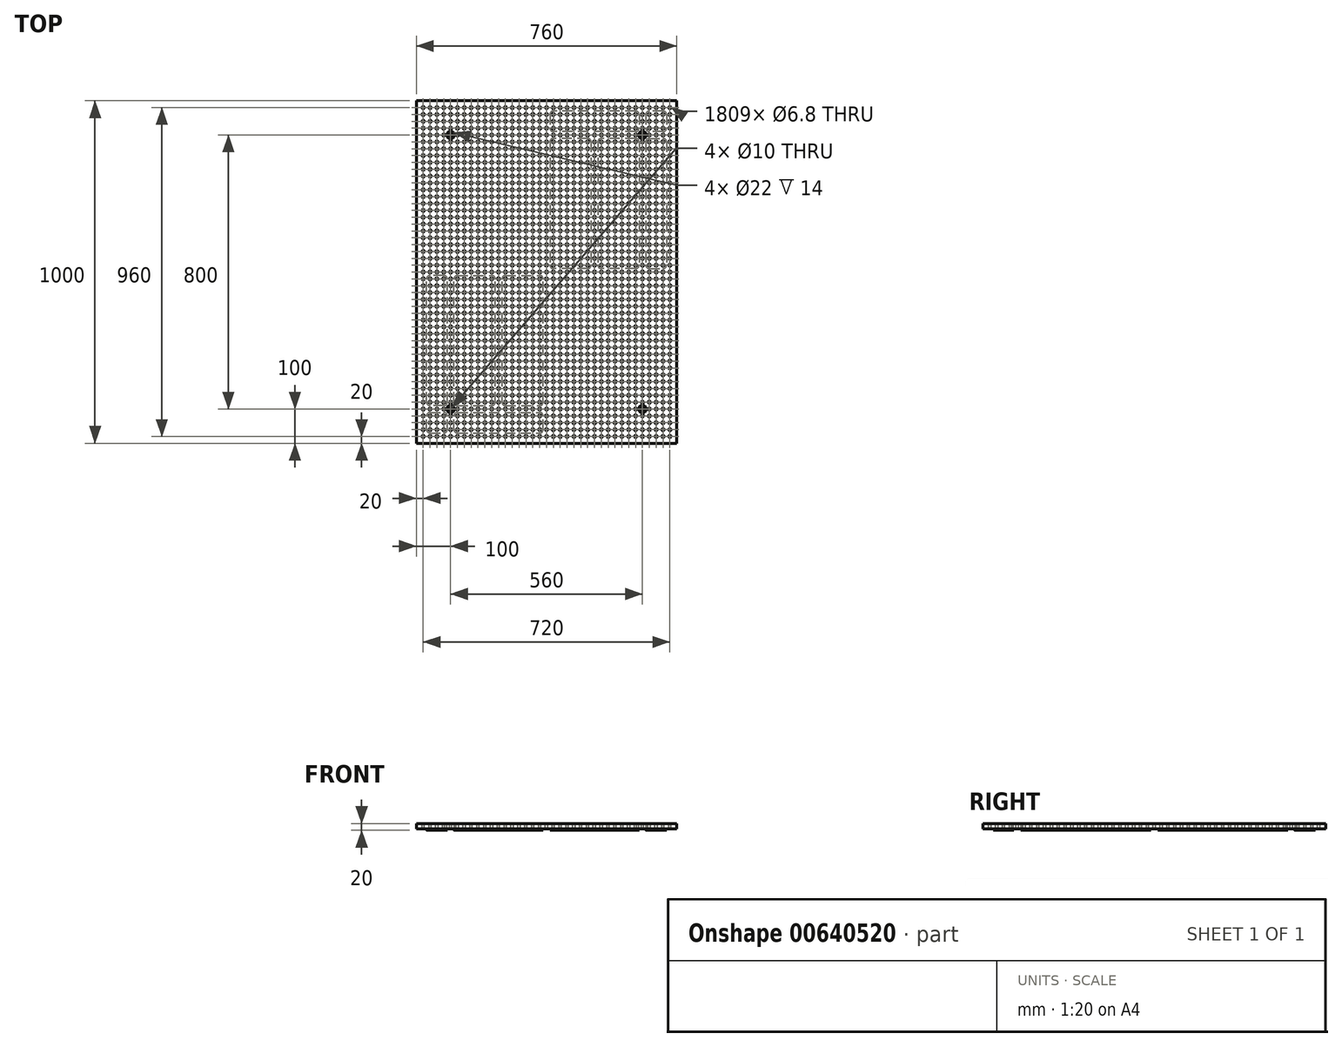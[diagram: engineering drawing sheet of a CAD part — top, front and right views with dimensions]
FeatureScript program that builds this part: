
annotation { "Feature Type Name" : "Feature", "Feature Type Description" : "" }
export const myFeature = defineFeature(function(context is Context, id is Id, definition is map)
    precondition{}
    {
        {
            var Q0;
            Q0=qCreatedBy(makeId("Top.planeOp"),FACE);
            var sketch = newSketch(context, id + "F0", { "sketchPlane" : qUnion([Q0])});
            skLineSegment(sketch, "E0.bottom", {"start": v(0, 0) * mm, "end": v(760, 0) * mm});
            skLineSegment(sketch, "E0.top", {"start": v(0, 1000) * mm, "end": v(760, 1000) * mm});
            skLineSegment(sketch, "E0.left", {"start": v(0, 0) * mm, "end": v(0, 1000) * mm});
            skLineSegment(sketch, "E0.right", {"start": v(760, 0) * mm, "end": v(760, 1000) * mm});
            skSolve(sketch);
        }
        {
            var Q0;
            Q0=qSketchRegion(id+"F0",true);
            extrude(context, id + "F1", {"entities" : qUnion([Q0]), "depth" : 20 * mm});
        }
        {
            var Q0;
            Q0=makeQuery(id+"F1.opExtrude","SWEPT_FACE",FACE,{"disambiguationData":[OSD([sQuery(id+"F0.wireOp",EDGE,"E0.left")])]});
            cPlane(context, id + "F2", {"entities" : qUnion([Q0]), "cplaneType" : CPlaneType.OFFSET, "offset" : 380 * mm, "oppositeDirection" : true, "width" : 150 * mm, "height" : 150 * mm});
        }
        {
            var Q0;
            Q0=makeQuery(id+"F1.opExtrude","SWEPT_FACE",FACE,{"disambiguationData":[OSD([sQuery(id+"F0.wireOp",EDGE,"E0.bottom")])]});
            cPlane(context, id + "F3", {"entities" : qUnion([Q0]), "cplaneType" : CPlaneType.OFFSET, "offset" : 500 * mm, "oppositeDirection" : true, "width" : 150 * mm, "height" : 150 * mm});
        }
        {
            var Q0;
            Q0=makeQuery(id+"F1.opExtrude","CAP_FACE",FACE,{"disambiguationData":[OSD([sQuery(id+"F0.wireOp",EDGE,"E0.bottom"),sQuery(id+"F0.wireOp",EDGE,"E0.top"),sQuery(id+"F0.wireOp",EDGE,"E0.left"),sQuery(id+"F0.wireOp",EDGE,"E0.right")])],"isStart":false});
            var sketch = newSketch(context, id + "F4", { "sketchPlane" : qUnion([Q0])});
            skCircle(sketch, "E1", {"center": v(20, 20) * mm, "radius": 3.4 * mm});
            skCircle(sketch, "E2.0.1.0", {"center": v(20, 40) * mm, "radius": 3.4 * mm});
            skCircle(sketch, "E2.0.2.0", {"center": v(20, 60) * mm, "radius": 3.4 * mm});
            skCircle(sketch, "E2.0.3.0", {"center": v(20, 80) * mm, "radius": 3.4 * mm});
            skCircle(sketch, "E2.0.4.0", {"center": v(20, 100) * mm, "radius": 3.4 * mm});
            skCircle(sketch, "E2.0.5.0", {"center": v(20, 120) * mm, "radius": 3.4 * mm});
            skCircle(sketch, "E2.0.6.0", {"center": v(20, 140) * mm, "radius": 3.4 * mm});
            skCircle(sketch, "E2.0.7.0", {"center": v(20, 160) * mm, "radius": 3.4 * mm});
            skCircle(sketch, "E2.0.8.0", {"center": v(20, 180) * mm, "radius": 3.4 * mm});
            skCircle(sketch, "E2.0.9.0", {"center": v(20, 200) * mm, "radius": 3.4 * mm});
            skCircle(sketch, "E2.0.10.0", {"center": v(20, 220) * mm, "radius": 3.4 * mm});
            skCircle(sketch, "E2.0.11.0", {"center": v(20, 240) * mm, "radius": 3.4 * mm});
            skCircle(sketch, "E2.0.12.0", {"center": v(20, 260) * mm, "radius": 3.4 * mm});
            skCircle(sketch, "E2.0.13.0", {"center": v(20, 280) * mm, "radius": 3.4 * mm});
            skCircle(sketch, "E2.0.14.0", {"center": v(20, 300) * mm, "radius": 3.4 * mm});
            skCircle(sketch, "E2.0.15.0", {"center": v(20, 320) * mm, "radius": 3.4 * mm});
            skCircle(sketch, "E2.0.16.0", {"center": v(20, 340) * mm, "radius": 3.4 * mm});
            skCircle(sketch, "E2.0.17.0", {"center": v(20, 360) * mm, "radius": 3.4 * mm});
            skCircle(sketch, "E2.0.18.0", {"center": v(20, 380) * mm, "radius": 3.4 * mm});
            skCircle(sketch, "E2.0.19.0", {"center": v(20, 400) * mm, "radius": 3.4 * mm});
            skCircle(sketch, "E2.0.20.0", {"center": v(20, 420) * mm, "radius": 3.4 * mm});
            skCircle(sketch, "E2.0.21.0", {"center": v(20, 440) * mm, "radius": 3.4 * mm});
            skCircle(sketch, "E2.0.22.0", {"center": v(20, 460) * mm, "radius": 3.4 * mm});
            skCircle(sketch, "E2.0.23.0", {"center": v(20, 480) * mm, "radius": 3.4 * mm});
            skCircle(sketch, "E2.0.24.0", {"center": v(20, 500) * mm, "radius": 3.4 * mm});
            skCircle(sketch, "E2.0.25.0", {"center": v(20, 520) * mm, "radius": 3.4 * mm});
            skCircle(sketch, "E2.0.26.0", {"center": v(20, 540) * mm, "radius": 3.4 * mm});
            skCircle(sketch, "E2.0.27.0", {"center": v(20, 560) * mm, "radius": 3.4 * mm});
            skCircle(sketch, "E2.0.28.0", {"center": v(20, 580) * mm, "radius": 3.4 * mm});
            skCircle(sketch, "E2.0.29.0", {"center": v(20, 600) * mm, "radius": 3.4 * mm});
            skCircle(sketch, "E2.0.30.0", {"center": v(20, 620) * mm, "radius": 3.4 * mm});
            skCircle(sketch, "E2.0.31.0", {"center": v(20, 640) * mm, "radius": 3.4 * mm});
            skCircle(sketch, "E2.0.32.0", {"center": v(20, 660) * mm, "radius": 3.4 * mm});
            skCircle(sketch, "E2.0.33.0", {"center": v(20, 680) * mm, "radius": 3.4 * mm});
            skCircle(sketch, "E2.0.34.0", {"center": v(20, 700) * mm, "radius": 3.4 * mm});
            skCircle(sketch, "E2.0.35.0", {"center": v(20, 720) * mm, "radius": 3.4 * mm});
            skCircle(sketch, "E2.0.36.0", {"center": v(20, 740) * mm, "radius": 3.4 * mm});
            skCircle(sketch, "E2.0.37.0", {"center": v(20, 760) * mm, "radius": 3.4 * mm});
            skCircle(sketch, "E2.0.38.0", {"center": v(20, 780) * mm, "radius": 3.4 * mm});
            skCircle(sketch, "E2.0.39.0", {"center": v(20, 800) * mm, "radius": 3.4 * mm});
            skCircle(sketch, "E2.0.40.0", {"center": v(20, 820) * mm, "radius": 3.4 * mm});
            skCircle(sketch, "E2.0.41.0", {"center": v(20, 840) * mm, "radius": 3.4 * mm});
            skCircle(sketch, "E2.0.42.0", {"center": v(20, 860) * mm, "radius": 3.4 * mm});
            skCircle(sketch, "E2.0.43.0", {"center": v(20, 880) * mm, "radius": 3.4 * mm});
            skCircle(sketch, "E2.0.44.0", {"center": v(20, 900) * mm, "radius": 3.4 * mm});
            skCircle(sketch, "E2.0.45.0", {"center": v(20, 920) * mm, "radius": 3.4 * mm});
            skCircle(sketch, "E2.0.46.0", {"center": v(20, 940) * mm, "radius": 3.4 * mm});
            skCircle(sketch, "E2.0.47.0", {"center": v(20, 960) * mm, "radius": 3.4 * mm});
            skCircle(sketch, "E2.0.48.0", {"center": v(20, 980) * mm, "radius": 3.4 * mm});
            skCircle(sketch, "E2.1.0.0", {"center": v(40, 20) * mm, "radius": 3.4 * mm});
            skCircle(sketch, "E2.1.1.0", {"center": v(40, 40) * mm, "radius": 3.4 * mm});
            skCircle(sketch, "E2.1.2.0", {"center": v(40, 60) * mm, "radius": 3.4 * mm});
            skCircle(sketch, "E2.1.3.0", {"center": v(40, 80) * mm, "radius": 3.4 * mm});
            skCircle(sketch, "E2.1.4.0", {"center": v(40, 100) * mm, "radius": 3.4 * mm});
            skCircle(sketch, "E2.1.5.0", {"center": v(40, 120) * mm, "radius": 3.4 * mm});
            skCircle(sketch, "E2.1.6.0", {"center": v(40, 140) * mm, "radius": 3.4 * mm});
            skCircle(sketch, "E2.1.7.0", {"center": v(40, 160) * mm, "radius": 3.4 * mm});
            skCircle(sketch, "E2.1.8.0", {"center": v(40, 180) * mm, "radius": 3.4 * mm});
            skCircle(sketch, "E2.1.9.0", {"center": v(40, 200) * mm, "radius": 3.4 * mm});
            skCircle(sketch, "E2.1.10.0", {"center": v(40, 220) * mm, "radius": 3.4 * mm});
            skCircle(sketch, "E2.1.11.0", {"center": v(40, 240) * mm, "radius": 3.4 * mm});
            skCircle(sketch, "E2.1.12.0", {"center": v(40, 260) * mm, "radius": 3.4 * mm});
            skCircle(sketch, "E2.1.13.0", {"center": v(40, 280) * mm, "radius": 3.4 * mm});
            skCircle(sketch, "E2.1.14.0", {"center": v(40, 300) * mm, "radius": 3.4 * mm});
            skCircle(sketch, "E2.1.15.0", {"center": v(40, 320) * mm, "radius": 3.4 * mm});
            skCircle(sketch, "E2.1.16.0", {"center": v(40, 340) * mm, "radius": 3.4 * mm});
            skCircle(sketch, "E2.1.17.0", {"center": v(40, 360) * mm, "radius": 3.4 * mm});
            skCircle(sketch, "E2.1.18.0", {"center": v(40, 380) * mm, "radius": 3.4 * mm});
            skCircle(sketch, "E2.1.19.0", {"center": v(40, 400) * mm, "radius": 3.4 * mm});
            skCircle(sketch, "E2.1.20.0", {"center": v(40, 420) * mm, "radius": 3.4 * mm});
            skCircle(sketch, "E2.1.21.0", {"center": v(40, 440) * mm, "radius": 3.4 * mm});
            skCircle(sketch, "E2.1.22.0", {"center": v(40, 460) * mm, "radius": 3.4 * mm});
            skCircle(sketch, "E2.1.23.0", {"center": v(40, 480) * mm, "radius": 3.4 * mm});
            skCircle(sketch, "E2.1.24.0", {"center": v(40, 500) * mm, "radius": 3.4 * mm});
            skCircle(sketch, "E2.1.25.0", {"center": v(40, 520) * mm, "radius": 3.4 * mm});
            skCircle(sketch, "E2.1.26.0", {"center": v(40, 540) * mm, "radius": 3.4 * mm});
            skCircle(sketch, "E2.1.27.0", {"center": v(40, 560) * mm, "radius": 3.4 * mm});
            skCircle(sketch, "E2.1.28.0", {"center": v(40, 580) * mm, "radius": 3.4 * mm});
            skCircle(sketch, "E2.1.29.0", {"center": v(40, 600) * mm, "radius": 3.4 * mm});
            skCircle(sketch, "E2.1.30.0", {"center": v(40, 620) * mm, "radius": 3.4 * mm});
            skCircle(sketch, "E2.1.31.0", {"center": v(40, 640) * mm, "radius": 3.4 * mm});
            skCircle(sketch, "E2.1.32.0", {"center": v(40, 660) * mm, "radius": 3.4 * mm});
            skCircle(sketch, "E2.1.33.0", {"center": v(40, 680) * mm, "radius": 3.4 * mm});
            skCircle(sketch, "E2.1.34.0", {"center": v(40, 700) * mm, "radius": 3.4 * mm});
            skCircle(sketch, "E2.1.35.0", {"center": v(40, 720) * mm, "radius": 3.4 * mm});
            skCircle(sketch, "E2.1.36.0", {"center": v(40, 740) * mm, "radius": 3.4 * mm});
            skCircle(sketch, "E2.1.37.0", {"center": v(40, 760) * mm, "radius": 3.4 * mm});
            skCircle(sketch, "E2.1.38.0", {"center": v(40, 780) * mm, "radius": 3.4 * mm});
            skCircle(sketch, "E2.1.39.0", {"center": v(40, 800) * mm, "radius": 3.4 * mm});
            skCircle(sketch, "E2.1.40.0", {"center": v(40, 820) * mm, "radius": 3.4 * mm});
            skCircle(sketch, "E2.1.41.0", {"center": v(40, 840) * mm, "radius": 3.4 * mm});
            skCircle(sketch, "E2.1.42.0", {"center": v(40, 860) * mm, "radius": 3.4 * mm});
            skCircle(sketch, "E2.1.43.0", {"center": v(40, 880) * mm, "radius": 3.4 * mm});
            skCircle(sketch, "E2.1.44.0", {"center": v(40, 900) * mm, "radius": 3.4 * mm});
            skCircle(sketch, "E2.1.45.0", {"center": v(40, 920) * mm, "radius": 3.4 * mm});
            skCircle(sketch, "E2.1.46.0", {"center": v(40, 940) * mm, "radius": 3.4 * mm});
            skCircle(sketch, "E2.1.47.0", {"center": v(40, 960) * mm, "radius": 3.4 * mm});
            skCircle(sketch, "E2.1.48.0", {"center": v(40, 980) * mm, "radius": 3.4 * mm});
            skCircle(sketch, "E2.2.0.0", {"center": v(60, 20) * mm, "radius": 3.4 * mm});
            skCircle(sketch, "E2.2.1.0", {"center": v(60, 40) * mm, "radius": 3.4 * mm});
            skCircle(sketch, "E2.2.2.0", {"center": v(60, 60) * mm, "radius": 3.4 * mm});
            skCircle(sketch, "E2.2.3.0", {"center": v(60, 80) * mm, "radius": 3.4 * mm});
            skCircle(sketch, "E2.2.4.0", {"center": v(60, 100) * mm, "radius": 3.4 * mm});
            skCircle(sketch, "E2.2.5.0", {"center": v(60, 120) * mm, "radius": 3.4 * mm});
            skCircle(sketch, "E2.2.6.0", {"center": v(60, 140) * mm, "radius": 3.4 * mm});
            skCircle(sketch, "E2.2.7.0", {"center": v(60, 160) * mm, "radius": 3.4 * mm});
            skCircle(sketch, "E2.2.8.0", {"center": v(60, 180) * mm, "radius": 3.4 * mm});
            skCircle(sketch, "E2.2.9.0", {"center": v(60, 200) * mm, "radius": 3.4 * mm});
            skCircle(sketch, "E2.2.10.0", {"center": v(60, 220) * mm, "radius": 3.4 * mm});
            skCircle(sketch, "E2.2.11.0", {"center": v(60, 240) * mm, "radius": 3.4 * mm});
            skCircle(sketch, "E2.2.12.0", {"center": v(60, 260) * mm, "radius": 3.4 * mm});
            skCircle(sketch, "E2.2.13.0", {"center": v(60, 280) * mm, "radius": 3.4 * mm});
            skCircle(sketch, "E2.2.14.0", {"center": v(60, 300) * mm, "radius": 3.4 * mm});
            skCircle(sketch, "E2.2.15.0", {"center": v(60, 320) * mm, "radius": 3.4 * mm});
            skCircle(sketch, "E2.2.16.0", {"center": v(60, 340) * mm, "radius": 3.4 * mm});
            skCircle(sketch, "E2.2.17.0", {"center": v(60, 360) * mm, "radius": 3.4 * mm});
            skCircle(sketch, "E2.2.18.0", {"center": v(60, 380) * mm, "radius": 3.4 * mm});
            skCircle(sketch, "E2.2.19.0", {"center": v(60, 400) * mm, "radius": 3.4 * mm});
            skCircle(sketch, "E2.2.20.0", {"center": v(60, 420) * mm, "radius": 3.4 * mm});
            skCircle(sketch, "E2.2.21.0", {"center": v(60, 440) * mm, "radius": 3.4 * mm});
            skCircle(sketch, "E2.2.22.0", {"center": v(60, 460) * mm, "radius": 3.4 * mm});
            skCircle(sketch, "E2.2.23.0", {"center": v(60, 480) * mm, "radius": 3.4 * mm});
            skCircle(sketch, "E2.2.24.0", {"center": v(60, 500) * mm, "radius": 3.4 * mm});
            skCircle(sketch, "E2.2.25.0", {"center": v(60, 520) * mm, "radius": 3.4 * mm});
            skCircle(sketch, "E2.2.26.0", {"center": v(60, 540) * mm, "radius": 3.4 * mm});
            skCircle(sketch, "E2.2.27.0", {"center": v(60, 560) * mm, "radius": 3.4 * mm});
            skCircle(sketch, "E2.2.28.0", {"center": v(60, 580) * mm, "radius": 3.4 * mm});
            skCircle(sketch, "E2.2.29.0", {"center": v(60, 600) * mm, "radius": 3.4 * mm});
            skCircle(sketch, "E2.2.30.0", {"center": v(60, 620) * mm, "radius": 3.4 * mm});
            skCircle(sketch, "E2.2.31.0", {"center": v(60, 640) * mm, "radius": 3.4 * mm});
            skCircle(sketch, "E2.2.32.0", {"center": v(60, 660) * mm, "radius": 3.4 * mm});
            skCircle(sketch, "E2.2.33.0", {"center": v(60, 680) * mm, "radius": 3.4 * mm});
            skCircle(sketch, "E2.2.34.0", {"center": v(60, 700) * mm, "radius": 3.4 * mm});
            skCircle(sketch, "E2.2.35.0", {"center": v(60, 720) * mm, "radius": 3.4 * mm});
            skCircle(sketch, "E2.2.36.0", {"center": v(60, 740) * mm, "radius": 3.4 * mm});
            skCircle(sketch, "E2.2.37.0", {"center": v(60, 760) * mm, "radius": 3.4 * mm});
            skCircle(sketch, "E2.2.38.0", {"center": v(60, 780) * mm, "radius": 3.4 * mm});
            skCircle(sketch, "E2.2.39.0", {"center": v(60, 800) * mm, "radius": 3.4 * mm});
            skCircle(sketch, "E2.2.40.0", {"center": v(60, 820) * mm, "radius": 3.4 * mm});
            skCircle(sketch, "E2.2.41.0", {"center": v(60, 840) * mm, "radius": 3.4 * mm});
            skCircle(sketch, "E2.2.42.0", {"center": v(60, 860) * mm, "radius": 3.4 * mm});
            skCircle(sketch, "E2.2.43.0", {"center": v(60, 880) * mm, "radius": 3.4 * mm});
            skCircle(sketch, "E2.2.44.0", {"center": v(60, 900) * mm, "radius": 3.4 * mm});
            skCircle(sketch, "E2.2.45.0", {"center": v(60, 920) * mm, "radius": 3.4 * mm});
            skCircle(sketch, "E2.2.46.0", {"center": v(60, 940) * mm, "radius": 3.4 * mm});
            skCircle(sketch, "E2.2.47.0", {"center": v(60, 960) * mm, "radius": 3.4 * mm});
            skCircle(sketch, "E2.2.48.0", {"center": v(60, 980) * mm, "radius": 3.4 * mm});
            skCircle(sketch, "E2.3.0.0", {"center": v(80, 20) * mm, "radius": 3.4 * mm});
            skCircle(sketch, "E2.3.1.0", {"center": v(80, 40) * mm, "radius": 3.4 * mm});
            skCircle(sketch, "E2.3.2.0", {"center": v(80, 60) * mm, "radius": 3.4 * mm});
            skCircle(sketch, "E2.3.3.0", {"center": v(80, 80) * mm, "radius": 3.4 * mm});
            skCircle(sketch, "E2.3.4.0", {"center": v(80, 100) * mm, "radius": 3.4 * mm});
            skCircle(sketch, "E2.3.5.0", {"center": v(80, 120) * mm, "radius": 3.4 * mm});
            skCircle(sketch, "E2.3.6.0", {"center": v(80, 140) * mm, "radius": 3.4 * mm});
            skCircle(sketch, "E2.3.7.0", {"center": v(80, 160) * mm, "radius": 3.4 * mm});
            skCircle(sketch, "E2.3.8.0", {"center": v(80, 180) * mm, "radius": 3.4 * mm});
            skCircle(sketch, "E2.3.9.0", {"center": v(80, 200) * mm, "radius": 3.4 * mm});
            skCircle(sketch, "E2.3.10.0", {"center": v(80, 220) * mm, "radius": 3.4 * mm});
            skCircle(sketch, "E2.3.11.0", {"center": v(80, 240) * mm, "radius": 3.4 * mm});
            skCircle(sketch, "E2.3.12.0", {"center": v(80, 260) * mm, "radius": 3.4 * mm});
            skCircle(sketch, "E2.3.13.0", {"center": v(80, 280) * mm, "radius": 3.4 * mm});
            skCircle(sketch, "E2.3.14.0", {"center": v(80, 300) * mm, "radius": 3.4 * mm});
            skCircle(sketch, "E2.3.15.0", {"center": v(80, 320) * mm, "radius": 3.4 * mm});
            skCircle(sketch, "E2.3.16.0", {"center": v(80, 340) * mm, "radius": 3.4 * mm});
            skCircle(sketch, "E2.3.17.0", {"center": v(80, 360) * mm, "radius": 3.4 * mm});
            skCircle(sketch, "E2.3.18.0", {"center": v(80, 380) * mm, "radius": 3.4 * mm});
            skCircle(sketch, "E2.3.19.0", {"center": v(80, 400) * mm, "radius": 3.4 * mm});
            skCircle(sketch, "E2.3.20.0", {"center": v(80, 420) * mm, "radius": 3.4 * mm});
            skCircle(sketch, "E2.3.21.0", {"center": v(80, 440) * mm, "radius": 3.4 * mm});
            skCircle(sketch, "E2.3.22.0", {"center": v(80, 460) * mm, "radius": 3.4 * mm});
            skCircle(sketch, "E2.3.23.0", {"center": v(80, 480) * mm, "radius": 3.4 * mm});
            skCircle(sketch, "E2.3.24.0", {"center": v(80, 500) * mm, "radius": 3.4 * mm});
            skCircle(sketch, "E2.3.25.0", {"center": v(80, 520) * mm, "radius": 3.4 * mm});
            skCircle(sketch, "E2.3.26.0", {"center": v(80, 540) * mm, "radius": 3.4 * mm});
            skCircle(sketch, "E2.3.27.0", {"center": v(80, 560) * mm, "radius": 3.4 * mm});
            skCircle(sketch, "E2.3.28.0", {"center": v(80, 580) * mm, "radius": 3.4 * mm});
            skCircle(sketch, "E2.3.29.0", {"center": v(80, 600) * mm, "radius": 3.4 * mm});
            skCircle(sketch, "E2.3.30.0", {"center": v(80, 620) * mm, "radius": 3.4 * mm});
            skCircle(sketch, "E2.3.31.0", {"center": v(80, 640) * mm, "radius": 3.4 * mm});
            skCircle(sketch, "E2.3.32.0", {"center": v(80, 660) * mm, "radius": 3.4 * mm});
            skCircle(sketch, "E2.3.33.0", {"center": v(80, 680) * mm, "radius": 3.4 * mm});
            skCircle(sketch, "E2.3.34.0", {"center": v(80, 700) * mm, "radius": 3.4 * mm});
            skCircle(sketch, "E2.3.35.0", {"center": v(80, 720) * mm, "radius": 3.4 * mm});
            skCircle(sketch, "E2.3.36.0", {"center": v(80, 740) * mm, "radius": 3.4 * mm});
            skCircle(sketch, "E2.3.37.0", {"center": v(80, 760) * mm, "radius": 3.4 * mm});
            skCircle(sketch, "E2.3.38.0", {"center": v(80, 780) * mm, "radius": 3.4 * mm});
            skCircle(sketch, "E2.3.39.0", {"center": v(80, 800) * mm, "radius": 3.4 * mm});
            skCircle(sketch, "E2.3.40.0", {"center": v(80, 820) * mm, "radius": 3.4 * mm});
            skCircle(sketch, "E2.3.41.0", {"center": v(80, 840) * mm, "radius": 3.4 * mm});
            skCircle(sketch, "E2.3.42.0", {"center": v(80, 860) * mm, "radius": 3.4 * mm});
            skCircle(sketch, "E2.3.43.0", {"center": v(80, 880) * mm, "radius": 3.4 * mm});
            skCircle(sketch, "E2.3.44.0", {"center": v(80, 900) * mm, "radius": 3.4 * mm});
            skCircle(sketch, "E2.3.45.0", {"center": v(80, 920) * mm, "radius": 3.4 * mm});
            skCircle(sketch, "E2.3.46.0", {"center": v(80, 940) * mm, "radius": 3.4 * mm});
            skCircle(sketch, "E2.3.47.0", {"center": v(80, 960) * mm, "radius": 3.4 * mm});
            skCircle(sketch, "E2.3.48.0", {"center": v(80, 980) * mm, "radius": 3.4 * mm});
            skCircle(sketch, "E2.4.0.0", {"center": v(100, 20) * mm, "radius": 3.4 * mm});
            skCircle(sketch, "E2.4.1.0", {"center": v(100, 40) * mm, "radius": 3.4 * mm});
            skCircle(sketch, "E2.4.2.0", {"center": v(100, 60) * mm, "radius": 3.4 * mm});
            skCircle(sketch, "E2.4.3.0", {"center": v(100, 80) * mm, "radius": 3.4 * mm});
            skCircle(sketch, "E2.4.4.0", {"center": v(100, 100) * mm, "radius": 3.4 * mm});
            skCircle(sketch, "E2.4.5.0", {"center": v(100, 120) * mm, "radius": 3.4 * mm});
            skCircle(sketch, "E2.4.6.0", {"center": v(100, 140) * mm, "radius": 3.4 * mm});
            skCircle(sketch, "E2.4.7.0", {"center": v(100, 160) * mm, "radius": 3.4 * mm});
            skCircle(sketch, "E2.4.8.0", {"center": v(100, 180) * mm, "radius": 3.4 * mm});
            skCircle(sketch, "E2.4.9.0", {"center": v(100, 200) * mm, "radius": 3.4 * mm});
            skCircle(sketch, "E2.4.10.0", {"center": v(100, 220) * mm, "radius": 3.4 * mm});
            skCircle(sketch, "E2.4.11.0", {"center": v(100, 240) * mm, "radius": 3.4 * mm});
            skCircle(sketch, "E2.4.12.0", {"center": v(100, 260) * mm, "radius": 3.4 * mm});
            skCircle(sketch, "E2.4.13.0", {"center": v(100, 280) * mm, "radius": 3.4 * mm});
            skCircle(sketch, "E2.4.14.0", {"center": v(100, 300) * mm, "radius": 3.4 * mm});
            skCircle(sketch, "E2.4.15.0", {"center": v(100, 320) * mm, "radius": 3.4 * mm});
            skCircle(sketch, "E2.4.16.0", {"center": v(100, 340) * mm, "radius": 3.4 * mm});
            skCircle(sketch, "E2.4.17.0", {"center": v(100, 360) * mm, "radius": 3.4 * mm});
            skCircle(sketch, "E2.4.18.0", {"center": v(100, 380) * mm, "radius": 3.4 * mm});
            skCircle(sketch, "E2.4.19.0", {"center": v(100, 400) * mm, "radius": 3.4 * mm});
            skCircle(sketch, "E2.4.20.0", {"center": v(100, 420) * mm, "radius": 3.4 * mm});
            skCircle(sketch, "E2.4.21.0", {"center": v(100, 440) * mm, "radius": 3.4 * mm});
            skCircle(sketch, "E2.4.22.0", {"center": v(100, 460) * mm, "radius": 3.4 * mm});
            skCircle(sketch, "E2.4.23.0", {"center": v(100, 480) * mm, "radius": 3.4 * mm});
            skCircle(sketch, "E2.4.24.0", {"center": v(100, 500) * mm, "radius": 3.4 * mm});
            skCircle(sketch, "E2.4.25.0", {"center": v(100, 520) * mm, "radius": 3.4 * mm});
            skCircle(sketch, "E2.4.26.0", {"center": v(100, 540) * mm, "radius": 3.4 * mm});
            skCircle(sketch, "E2.4.27.0", {"center": v(100, 560) * mm, "radius": 3.4 * mm});
            skCircle(sketch, "E2.4.28.0", {"center": v(100, 580) * mm, "radius": 3.4 * mm});
            skCircle(sketch, "E2.4.29.0", {"center": v(100, 600) * mm, "radius": 3.4 * mm});
            skCircle(sketch, "E2.4.30.0", {"center": v(100, 620) * mm, "radius": 3.4 * mm});
            skCircle(sketch, "E2.4.31.0", {"center": v(100, 640) * mm, "radius": 3.4 * mm});
            skCircle(sketch, "E2.4.32.0", {"center": v(100, 660) * mm, "radius": 3.4 * mm});
            skCircle(sketch, "E2.4.33.0", {"center": v(100, 680) * mm, "radius": 3.4 * mm});
            skCircle(sketch, "E2.4.34.0", {"center": v(100, 700) * mm, "radius": 3.4 * mm});
            skCircle(sketch, "E2.4.35.0", {"center": v(100, 720) * mm, "radius": 3.4 * mm});
            skCircle(sketch, "E2.4.36.0", {"center": v(100, 740) * mm, "radius": 3.4 * mm});
            skCircle(sketch, "E2.4.37.0", {"center": v(100, 760) * mm, "radius": 3.4 * mm});
            skCircle(sketch, "E2.4.38.0", {"center": v(100, 780) * mm, "radius": 3.4 * mm});
            skCircle(sketch, "E2.4.39.0", {"center": v(100, 800) * mm, "radius": 3.4 * mm});
            skCircle(sketch, "E2.4.40.0", {"center": v(100, 820) * mm, "radius": 3.4 * mm});
            skCircle(sketch, "E2.4.41.0", {"center": v(100, 840) * mm, "radius": 3.4 * mm});
            skCircle(sketch, "E2.4.42.0", {"center": v(100, 860) * mm, "radius": 3.4 * mm});
            skCircle(sketch, "E2.4.43.0", {"center": v(100, 880) * mm, "radius": 3.4 * mm});
            skCircle(sketch, "E2.4.44.0", {"center": v(100, 900) * mm, "radius": 3.4 * mm});
            skCircle(sketch, "E2.4.45.0", {"center": v(100, 920) * mm, "radius": 3.4 * mm});
            skCircle(sketch, "E2.4.46.0", {"center": v(100, 940) * mm, "radius": 3.4 * mm});
            skCircle(sketch, "E2.4.47.0", {"center": v(100, 960) * mm, "radius": 3.4 * mm});
            skCircle(sketch, "E2.4.48.0", {"center": v(100, 980) * mm, "radius": 3.4 * mm});
            skCircle(sketch, "E2.5.0.0", {"center": v(120, 20) * mm, "radius": 3.4 * mm});
            skCircle(sketch, "E2.5.1.0", {"center": v(120, 40) * mm, "radius": 3.4 * mm});
            skCircle(sketch, "E2.5.2.0", {"center": v(120, 60) * mm, "radius": 3.4 * mm});
            skCircle(sketch, "E2.5.3.0", {"center": v(120, 80) * mm, "radius": 3.4 * mm});
            skCircle(sketch, "E2.5.4.0", {"center": v(120, 100) * mm, "radius": 3.4 * mm});
            skCircle(sketch, "E2.5.5.0", {"center": v(120, 120) * mm, "radius": 3.4 * mm});
            skCircle(sketch, "E2.5.6.0", {"center": v(120, 140) * mm, "radius": 3.4 * mm});
            skCircle(sketch, "E2.5.7.0", {"center": v(120, 160) * mm, "radius": 3.4 * mm});
            skCircle(sketch, "E2.5.8.0", {"center": v(120, 180) * mm, "radius": 3.4 * mm});
            skCircle(sketch, "E2.5.9.0", {"center": v(120, 200) * mm, "radius": 3.4 * mm});
            skCircle(sketch, "E2.5.10.0", {"center": v(120, 220) * mm, "radius": 3.4 * mm});
            skCircle(sketch, "E2.5.11.0", {"center": v(120, 240) * mm, "radius": 3.4 * mm});
            skCircle(sketch, "E2.5.12.0", {"center": v(120, 260) * mm, "radius": 3.4 * mm});
            skCircle(sketch, "E2.5.13.0", {"center": v(120, 280) * mm, "radius": 3.4 * mm});
            skCircle(sketch, "E2.5.14.0", {"center": v(120, 300) * mm, "radius": 3.4 * mm});
            skCircle(sketch, "E2.5.15.0", {"center": v(120, 320) * mm, "radius": 3.4 * mm});
            skCircle(sketch, "E2.5.16.0", {"center": v(120, 340) * mm, "radius": 3.4 * mm});
            skCircle(sketch, "E2.5.17.0", {"center": v(120, 360) * mm, "radius": 3.4 * mm});
            skCircle(sketch, "E2.5.18.0", {"center": v(120, 380) * mm, "radius": 3.4 * mm});
            skCircle(sketch, "E2.5.19.0", {"center": v(120, 400) * mm, "radius": 3.4 * mm});
            skCircle(sketch, "E2.5.20.0", {"center": v(120, 420) * mm, "radius": 3.4 * mm});
            skCircle(sketch, "E2.5.21.0", {"center": v(120, 440) * mm, "radius": 3.4 * mm});
            skCircle(sketch, "E2.5.22.0", {"center": v(120, 460) * mm, "radius": 3.4 * mm});
            skCircle(sketch, "E2.5.23.0", {"center": v(120, 480) * mm, "radius": 3.4 * mm});
            skCircle(sketch, "E2.5.24.0", {"center": v(120, 500) * mm, "radius": 3.4 * mm});
            skCircle(sketch, "E2.5.25.0", {"center": v(120, 520) * mm, "radius": 3.4 * mm});
            skCircle(sketch, "E2.5.26.0", {"center": v(120, 540) * mm, "radius": 3.4 * mm});
            skCircle(sketch, "E2.5.27.0", {"center": v(120, 560) * mm, "radius": 3.4 * mm});
            skCircle(sketch, "E2.5.28.0", {"center": v(120, 580) * mm, "radius": 3.4 * mm});
            skCircle(sketch, "E2.5.29.0", {"center": v(120, 600) * mm, "radius": 3.4 * mm});
            skCircle(sketch, "E2.5.30.0", {"center": v(120, 620) * mm, "radius": 3.4 * mm});
            skCircle(sketch, "E2.5.31.0", {"center": v(120, 640) * mm, "radius": 3.4 * mm});
            skCircle(sketch, "E2.5.32.0", {"center": v(120, 660) * mm, "radius": 3.4 * mm});
            skCircle(sketch, "E2.5.33.0", {"center": v(120, 680) * mm, "radius": 3.4 * mm});
            skCircle(sketch, "E2.5.34.0", {"center": v(120, 700) * mm, "radius": 3.4 * mm});
            skCircle(sketch, "E2.5.35.0", {"center": v(120, 720) * mm, "radius": 3.4 * mm});
            skCircle(sketch, "E2.5.36.0", {"center": v(120, 740) * mm, "radius": 3.4 * mm});
            skCircle(sketch, "E2.5.37.0", {"center": v(120, 760) * mm, "radius": 3.4 * mm});
            skCircle(sketch, "E2.5.38.0", {"center": v(120, 780) * mm, "radius": 3.4 * mm});
            skCircle(sketch, "E2.5.39.0", {"center": v(120, 800) * mm, "radius": 3.4 * mm});
            skCircle(sketch, "E2.5.40.0", {"center": v(120, 820) * mm, "radius": 3.4 * mm});
            skCircle(sketch, "E2.5.41.0", {"center": v(120, 840) * mm, "radius": 3.4 * mm});
            skCircle(sketch, "E2.5.42.0", {"center": v(120, 860) * mm, "radius": 3.4 * mm});
            skCircle(sketch, "E2.5.43.0", {"center": v(120, 880) * mm, "radius": 3.4 * mm});
            skCircle(sketch, "E2.5.44.0", {"center": v(120, 900) * mm, "radius": 3.4 * mm});
            skCircle(sketch, "E2.5.45.0", {"center": v(120, 920) * mm, "radius": 3.4 * mm});
            skCircle(sketch, "E2.5.46.0", {"center": v(120, 940) * mm, "radius": 3.4 * mm});
            skCircle(sketch, "E2.5.47.0", {"center": v(120, 960) * mm, "radius": 3.4 * mm});
            skCircle(sketch, "E2.5.48.0", {"center": v(120, 980) * mm, "radius": 3.4 * mm});
            skCircle(sketch, "E2.6.0.0", {"center": v(140, 20) * mm, "radius": 3.4 * mm});
            skCircle(sketch, "E2.6.1.0", {"center": v(140, 40) * mm, "radius": 3.4 * mm});
            skCircle(sketch, "E2.6.2.0", {"center": v(140, 60) * mm, "radius": 3.4 * mm});
            skCircle(sketch, "E2.6.3.0", {"center": v(140, 80) * mm, "radius": 3.4 * mm});
            skCircle(sketch, "E2.6.4.0", {"center": v(140, 100) * mm, "radius": 3.4 * mm});
            skCircle(sketch, "E2.6.5.0", {"center": v(140, 120) * mm, "radius": 3.4 * mm});
            skCircle(sketch, "E2.6.6.0", {"center": v(140, 140) * mm, "radius": 3.4 * mm});
            skCircle(sketch, "E2.6.7.0", {"center": v(140, 160) * mm, "radius": 3.4 * mm});
            skCircle(sketch, "E2.6.8.0", {"center": v(140, 180) * mm, "radius": 3.4 * mm});
            skCircle(sketch, "E2.6.9.0", {"center": v(140, 200) * mm, "radius": 3.4 * mm});
            skCircle(sketch, "E2.6.10.0", {"center": v(140, 220) * mm, "radius": 3.4 * mm});
            skCircle(sketch, "E2.6.11.0", {"center": v(140, 240) * mm, "radius": 3.4 * mm});
            skCircle(sketch, "E2.6.12.0", {"center": v(140, 260) * mm, "radius": 3.4 * mm});
            skCircle(sketch, "E2.6.13.0", {"center": v(140, 280) * mm, "radius": 3.4 * mm});
            skCircle(sketch, "E2.6.14.0", {"center": v(140, 300) * mm, "radius": 3.4 * mm});
            skCircle(sketch, "E2.6.15.0", {"center": v(140, 320) * mm, "radius": 3.4 * mm});
            skCircle(sketch, "E2.6.16.0", {"center": v(140, 340) * mm, "radius": 3.4 * mm});
            skCircle(sketch, "E2.6.17.0", {"center": v(140, 360) * mm, "radius": 3.4 * mm});
            skCircle(sketch, "E2.6.18.0", {"center": v(140, 380) * mm, "radius": 3.4 * mm});
            skCircle(sketch, "E2.6.19.0", {"center": v(140, 400) * mm, "radius": 3.4 * mm});
            skCircle(sketch, "E2.6.20.0", {"center": v(140, 420) * mm, "radius": 3.4 * mm});
            skCircle(sketch, "E2.6.21.0", {"center": v(140, 440) * mm, "radius": 3.4 * mm});
            skCircle(sketch, "E2.6.22.0", {"center": v(140, 460) * mm, "radius": 3.4 * mm});
            skCircle(sketch, "E2.6.23.0", {"center": v(140, 480) * mm, "radius": 3.4 * mm});
            skCircle(sketch, "E2.6.24.0", {"center": v(140, 500) * mm, "radius": 3.4 * mm});
            skCircle(sketch, "E2.6.25.0", {"center": v(140, 520) * mm, "radius": 3.4 * mm});
            skCircle(sketch, "E2.6.26.0", {"center": v(140, 540) * mm, "radius": 3.4 * mm});
            skCircle(sketch, "E2.6.27.0", {"center": v(140, 560) * mm, "radius": 3.4 * mm});
            skCircle(sketch, "E2.6.28.0", {"center": v(140, 580) * mm, "radius": 3.4 * mm});
            skCircle(sketch, "E2.6.29.0", {"center": v(140, 600) * mm, "radius": 3.4 * mm});
            skCircle(sketch, "E2.6.30.0", {"center": v(140, 620) * mm, "radius": 3.4 * mm});
            skCircle(sketch, "E2.6.31.0", {"center": v(140, 640) * mm, "radius": 3.4 * mm});
            skCircle(sketch, "E2.6.32.0", {"center": v(140, 660) * mm, "radius": 3.4 * mm});
            skCircle(sketch, "E2.6.33.0", {"center": v(140, 680) * mm, "radius": 3.4 * mm});
            skCircle(sketch, "E2.6.34.0", {"center": v(140, 700) * mm, "radius": 3.4 * mm});
            skCircle(sketch, "E2.6.35.0", {"center": v(140, 720) * mm, "radius": 3.4 * mm});
            skCircle(sketch, "E2.6.36.0", {"center": v(140, 740) * mm, "radius": 3.4 * mm});
            skCircle(sketch, "E2.6.37.0", {"center": v(140, 760) * mm, "radius": 3.4 * mm});
            skCircle(sketch, "E2.6.38.0", {"center": v(140, 780) * mm, "radius": 3.4 * mm});
            skCircle(sketch, "E2.6.39.0", {"center": v(140, 800) * mm, "radius": 3.4 * mm});
            skCircle(sketch, "E2.6.40.0", {"center": v(140, 820) * mm, "radius": 3.4 * mm});
            skCircle(sketch, "E2.6.41.0", {"center": v(140, 840) * mm, "radius": 3.4 * mm});
            skCircle(sketch, "E2.6.42.0", {"center": v(140, 860) * mm, "radius": 3.4 * mm});
            skCircle(sketch, "E2.6.43.0", {"center": v(140, 880) * mm, "radius": 3.4 * mm});
            skCircle(sketch, "E2.6.44.0", {"center": v(140, 900) * mm, "radius": 3.4 * mm});
            skCircle(sketch, "E2.6.45.0", {"center": v(140, 920) * mm, "radius": 3.4 * mm});
            skCircle(sketch, "E2.6.46.0", {"center": v(140, 940) * mm, "radius": 3.4 * mm});
            skCircle(sketch, "E2.6.47.0", {"center": v(140, 960) * mm, "radius": 3.4 * mm});
            skCircle(sketch, "E2.6.48.0", {"center": v(140, 980) * mm, "radius": 3.4 * mm});
            skCircle(sketch, "E2.7.0.0", {"center": v(160, 20) * mm, "radius": 3.4 * mm});
            skCircle(sketch, "E2.7.1.0", {"center": v(160, 40) * mm, "radius": 3.4 * mm});
            skCircle(sketch, "E2.7.2.0", {"center": v(160, 60) * mm, "radius": 3.4 * mm});
            skCircle(sketch, "E2.7.3.0", {"center": v(160, 80) * mm, "radius": 3.4 * mm});
            skCircle(sketch, "E2.7.4.0", {"center": v(160, 100) * mm, "radius": 3.4 * mm});
            skCircle(sketch, "E2.7.5.0", {"center": v(160, 120) * mm, "radius": 3.4 * mm});
            skCircle(sketch, "E2.7.6.0", {"center": v(160, 140) * mm, "radius": 3.4 * mm});
            skCircle(sketch, "E2.7.7.0", {"center": v(160, 160) * mm, "radius": 3.4 * mm});
            skCircle(sketch, "E2.7.8.0", {"center": v(160, 180) * mm, "radius": 3.4 * mm});
            skCircle(sketch, "E2.7.9.0", {"center": v(160, 200) * mm, "radius": 3.4 * mm});
            skCircle(sketch, "E2.7.10.0", {"center": v(160, 220) * mm, "radius": 3.4 * mm});
            skCircle(sketch, "E2.7.11.0", {"center": v(160, 240) * mm, "radius": 3.4 * mm});
            skCircle(sketch, "E2.7.12.0", {"center": v(160, 260) * mm, "radius": 3.4 * mm});
            skCircle(sketch, "E2.7.13.0", {"center": v(160, 280) * mm, "radius": 3.4 * mm});
            skCircle(sketch, "E2.7.14.0", {"center": v(160, 300) * mm, "radius": 3.4 * mm});
            skCircle(sketch, "E2.7.15.0", {"center": v(160, 320) * mm, "radius": 3.4 * mm});
            skCircle(sketch, "E2.7.16.0", {"center": v(160, 340) * mm, "radius": 3.4 * mm});
            skCircle(sketch, "E2.7.17.0", {"center": v(160, 360) * mm, "radius": 3.4 * mm});
            skCircle(sketch, "E2.7.18.0", {"center": v(160, 380) * mm, "radius": 3.4 * mm});
            skCircle(sketch, "E2.7.19.0", {"center": v(160, 400) * mm, "radius": 3.4 * mm});
            skCircle(sketch, "E2.7.20.0", {"center": v(160, 420) * mm, "radius": 3.4 * mm});
            skCircle(sketch, "E2.7.21.0", {"center": v(160, 440) * mm, "radius": 3.4 * mm});
            skCircle(sketch, "E2.7.22.0", {"center": v(160, 460) * mm, "radius": 3.4 * mm});
            skCircle(sketch, "E2.7.23.0", {"center": v(160, 480) * mm, "radius": 3.4 * mm});
            skCircle(sketch, "E2.7.24.0", {"center": v(160, 500) * mm, "radius": 3.4 * mm});
            skCircle(sketch, "E2.7.25.0", {"center": v(160, 520) * mm, "radius": 3.4 * mm});
            skCircle(sketch, "E2.7.26.0", {"center": v(160, 540) * mm, "radius": 3.4 * mm});
            skCircle(sketch, "E2.7.27.0", {"center": v(160, 560) * mm, "radius": 3.4 * mm});
            skCircle(sketch, "E2.7.28.0", {"center": v(160, 580) * mm, "radius": 3.4 * mm});
            skCircle(sketch, "E2.7.29.0", {"center": v(160, 600) * mm, "radius": 3.4 * mm});
            skCircle(sketch, "E2.7.30.0", {"center": v(160, 620) * mm, "radius": 3.4 * mm});
            skCircle(sketch, "E2.7.31.0", {"center": v(160, 640) * mm, "radius": 3.4 * mm});
            skCircle(sketch, "E2.7.32.0", {"center": v(160, 660) * mm, "radius": 3.4 * mm});
            skCircle(sketch, "E2.7.33.0", {"center": v(160, 680) * mm, "radius": 3.4 * mm});
            skCircle(sketch, "E2.7.34.0", {"center": v(160, 700) * mm, "radius": 3.4 * mm});
            skCircle(sketch, "E2.7.35.0", {"center": v(160, 720) * mm, "radius": 3.4 * mm});
            skCircle(sketch, "E2.7.36.0", {"center": v(160, 740) * mm, "radius": 3.4 * mm});
            skCircle(sketch, "E2.7.37.0", {"center": v(160, 760) * mm, "radius": 3.4 * mm});
            skCircle(sketch, "E2.7.38.0", {"center": v(160, 780) * mm, "radius": 3.4 * mm});
            skCircle(sketch, "E2.7.39.0", {"center": v(160, 800) * mm, "radius": 3.4 * mm});
            skCircle(sketch, "E2.7.40.0", {"center": v(160, 820) * mm, "radius": 3.4 * mm});
            skCircle(sketch, "E2.7.41.0", {"center": v(160, 840) * mm, "radius": 3.4 * mm});
            skCircle(sketch, "E2.7.42.0", {"center": v(160, 860) * mm, "radius": 3.4 * mm});
            skCircle(sketch, "E2.7.43.0", {"center": v(160, 880) * mm, "radius": 3.4 * mm});
            skCircle(sketch, "E2.7.44.0", {"center": v(160, 900) * mm, "radius": 3.4 * mm});
            skCircle(sketch, "E2.7.45.0", {"center": v(160, 920) * mm, "radius": 3.4 * mm});
            skCircle(sketch, "E2.7.46.0", {"center": v(160, 940) * mm, "radius": 3.4 * mm});
            skCircle(sketch, "E2.7.47.0", {"center": v(160, 960) * mm, "radius": 3.4 * mm});
            skCircle(sketch, "E2.7.48.0", {"center": v(160, 980) * mm, "radius": 3.4 * mm});
            skCircle(sketch, "E2.8.0.0", {"center": v(180, 20) * mm, "radius": 3.4 * mm});
            skCircle(sketch, "E2.8.1.0", {"center": v(180, 40) * mm, "radius": 3.4 * mm});
            skCircle(sketch, "E2.8.2.0", {"center": v(180, 60) * mm, "radius": 3.4 * mm});
            skCircle(sketch, "E2.8.3.0", {"center": v(180, 80) * mm, "radius": 3.4 * mm});
            skCircle(sketch, "E2.8.4.0", {"center": v(180, 100) * mm, "radius": 3.4 * mm});
            skCircle(sketch, "E2.8.5.0", {"center": v(180, 120) * mm, "radius": 3.4 * mm});
            skCircle(sketch, "E2.8.6.0", {"center": v(180, 140) * mm, "radius": 3.4 * mm});
            skCircle(sketch, "E2.8.7.0", {"center": v(180, 160) * mm, "radius": 3.4 * mm});
            skCircle(sketch, "E2.8.8.0", {"center": v(180, 180) * mm, "radius": 3.4 * mm});
            skCircle(sketch, "E2.8.9.0", {"center": v(180, 200) * mm, "radius": 3.4 * mm});
            skCircle(sketch, "E2.8.10.0", {"center": v(180, 220) * mm, "radius": 3.4 * mm});
            skCircle(sketch, "E2.8.11.0", {"center": v(180, 240) * mm, "radius": 3.4 * mm});
            skCircle(sketch, "E2.8.12.0", {"center": v(180, 260) * mm, "radius": 3.4 * mm});
            skCircle(sketch, "E2.8.13.0", {"center": v(180, 280) * mm, "radius": 3.4 * mm});
            skCircle(sketch, "E2.8.14.0", {"center": v(180, 300) * mm, "radius": 3.4 * mm});
            skCircle(sketch, "E2.8.15.0", {"center": v(180, 320) * mm, "radius": 3.4 * mm});
            skCircle(sketch, "E2.8.16.0", {"center": v(180, 340) * mm, "radius": 3.4 * mm});
            skCircle(sketch, "E2.8.17.0", {"center": v(180, 360) * mm, "radius": 3.4 * mm});
            skCircle(sketch, "E2.8.18.0", {"center": v(180, 380) * mm, "radius": 3.4 * mm});
            skCircle(sketch, "E2.8.19.0", {"center": v(180, 400) * mm, "radius": 3.4 * mm});
            skCircle(sketch, "E2.8.20.0", {"center": v(180, 420) * mm, "radius": 3.4 * mm});
            skCircle(sketch, "E2.8.21.0", {"center": v(180, 440) * mm, "radius": 3.4 * mm});
            skCircle(sketch, "E2.8.22.0", {"center": v(180, 460) * mm, "radius": 3.4 * mm});
            skCircle(sketch, "E2.8.23.0", {"center": v(180, 480) * mm, "radius": 3.4 * mm});
            skCircle(sketch, "E2.8.24.0", {"center": v(180, 500) * mm, "radius": 3.4 * mm});
            skCircle(sketch, "E2.8.25.0", {"center": v(180, 520) * mm, "radius": 3.4 * mm});
            skCircle(sketch, "E2.8.26.0", {"center": v(180, 540) * mm, "radius": 3.4 * mm});
            skCircle(sketch, "E2.8.27.0", {"center": v(180, 560) * mm, "radius": 3.4 * mm});
            skCircle(sketch, "E2.8.28.0", {"center": v(180, 580) * mm, "radius": 3.4 * mm});
            skCircle(sketch, "E2.8.29.0", {"center": v(180, 600) * mm, "radius": 3.4 * mm});
            skCircle(sketch, "E2.8.30.0", {"center": v(180, 620) * mm, "radius": 3.4 * mm});
            skCircle(sketch, "E2.8.31.0", {"center": v(180, 640) * mm, "radius": 3.4 * mm});
            skCircle(sketch, "E2.8.32.0", {"center": v(180, 660) * mm, "radius": 3.4 * mm});
            skCircle(sketch, "E2.8.33.0", {"center": v(180, 680) * mm, "radius": 3.4 * mm});
            skCircle(sketch, "E2.8.34.0", {"center": v(180, 700) * mm, "radius": 3.4 * mm});
            skCircle(sketch, "E2.8.35.0", {"center": v(180, 720) * mm, "radius": 3.4 * mm});
            skCircle(sketch, "E2.8.36.0", {"center": v(180, 740) * mm, "radius": 3.4 * mm});
            skCircle(sketch, "E2.8.37.0", {"center": v(180, 760) * mm, "radius": 3.4 * mm});
            skCircle(sketch, "E2.8.38.0", {"center": v(180, 780) * mm, "radius": 3.4 * mm});
            skCircle(sketch, "E2.8.39.0", {"center": v(180, 800) * mm, "radius": 3.4 * mm});
            skCircle(sketch, "E2.8.40.0", {"center": v(180, 820) * mm, "radius": 3.4 * mm});
            skCircle(sketch, "E2.8.41.0", {"center": v(180, 840) * mm, "radius": 3.4 * mm});
            skCircle(sketch, "E2.8.42.0", {"center": v(180, 860) * mm, "radius": 3.4 * mm});
            skCircle(sketch, "E2.8.43.0", {"center": v(180, 880) * mm, "radius": 3.4 * mm});
            skCircle(sketch, "E2.8.44.0", {"center": v(180, 900) * mm, "radius": 3.4 * mm});
            skCircle(sketch, "E2.8.45.0", {"center": v(180, 920) * mm, "radius": 3.4 * mm});
            skCircle(sketch, "E2.8.46.0", {"center": v(180, 940) * mm, "radius": 3.4 * mm});
            skCircle(sketch, "E2.8.47.0", {"center": v(180, 960) * mm, "radius": 3.4 * mm});
            skCircle(sketch, "E2.8.48.0", {"center": v(180, 980) * mm, "radius": 3.4 * mm});
            skCircle(sketch, "E2.9.0.0", {"center": v(200, 20) * mm, "radius": 3.4 * mm});
            skCircle(sketch, "E2.9.1.0", {"center": v(200, 40) * mm, "radius": 3.4 * mm});
            skCircle(sketch, "E2.9.2.0", {"center": v(200, 60) * mm, "radius": 3.4 * mm});
            skCircle(sketch, "E2.9.3.0", {"center": v(200, 80) * mm, "radius": 3.4 * mm});
            skCircle(sketch, "E2.9.4.0", {"center": v(200, 100) * mm, "radius": 3.4 * mm});
            skCircle(sketch, "E2.9.5.0", {"center": v(200, 120) * mm, "radius": 3.4 * mm});
            skCircle(sketch, "E2.9.6.0", {"center": v(200, 140) * mm, "radius": 3.4 * mm});
            skCircle(sketch, "E2.9.7.0", {"center": v(200, 160) * mm, "radius": 3.4 * mm});
            skCircle(sketch, "E2.9.8.0", {"center": v(200, 180) * mm, "radius": 3.4 * mm});
            skCircle(sketch, "E2.9.9.0", {"center": v(200, 200) * mm, "radius": 3.4 * mm});
            skCircle(sketch, "E2.9.10.0", {"center": v(200, 220) * mm, "radius": 3.4 * mm});
            skCircle(sketch, "E2.9.11.0", {"center": v(200, 240) * mm, "radius": 3.4 * mm});
            skCircle(sketch, "E2.9.12.0", {"center": v(200, 260) * mm, "radius": 3.4 * mm});
            skCircle(sketch, "E2.9.13.0", {"center": v(200, 280) * mm, "radius": 3.4 * mm});
            skCircle(sketch, "E2.9.14.0", {"center": v(200, 300) * mm, "radius": 3.4 * mm});
            skCircle(sketch, "E2.9.15.0", {"center": v(200, 320) * mm, "radius": 3.4 * mm});
            skCircle(sketch, "E2.9.16.0", {"center": v(200, 340) * mm, "radius": 3.4 * mm});
            skCircle(sketch, "E2.9.17.0", {"center": v(200, 360) * mm, "radius": 3.4 * mm});
            skCircle(sketch, "E2.9.18.0", {"center": v(200, 380) * mm, "radius": 3.4 * mm});
            skCircle(sketch, "E2.9.19.0", {"center": v(200, 400) * mm, "radius": 3.4 * mm});
            skCircle(sketch, "E2.9.20.0", {"center": v(200, 420) * mm, "radius": 3.4 * mm});
            skCircle(sketch, "E2.9.21.0", {"center": v(200, 440) * mm, "radius": 3.4 * mm});
            skCircle(sketch, "E2.9.22.0", {"center": v(200, 460) * mm, "radius": 3.4 * mm});
            skCircle(sketch, "E2.9.23.0", {"center": v(200, 480) * mm, "radius": 3.4 * mm});
            skCircle(sketch, "E2.9.24.0", {"center": v(200, 500) * mm, "radius": 3.4 * mm});
            skCircle(sketch, "E2.9.25.0", {"center": v(200, 520) * mm, "radius": 3.4 * mm});
            skCircle(sketch, "E2.9.26.0", {"center": v(200, 540) * mm, "radius": 3.4 * mm});
            skCircle(sketch, "E2.9.27.0", {"center": v(200, 560) * mm, "radius": 3.4 * mm});
            skCircle(sketch, "E2.9.28.0", {"center": v(200, 580) * mm, "radius": 3.4 * mm});
            skCircle(sketch, "E2.9.29.0", {"center": v(200, 600) * mm, "radius": 3.4 * mm});
            skCircle(sketch, "E2.9.30.0", {"center": v(200, 620) * mm, "radius": 3.4 * mm});
            skCircle(sketch, "E2.9.31.0", {"center": v(200, 640) * mm, "radius": 3.4 * mm});
            skCircle(sketch, "E2.9.32.0", {"center": v(200, 660) * mm, "radius": 3.4 * mm});
            skCircle(sketch, "E2.9.33.0", {"center": v(200, 680) * mm, "radius": 3.4 * mm});
            skCircle(sketch, "E2.9.34.0", {"center": v(200, 700) * mm, "radius": 3.4 * mm});
            skCircle(sketch, "E2.9.35.0", {"center": v(200, 720) * mm, "radius": 3.4 * mm});
            skCircle(sketch, "E2.9.36.0", {"center": v(200, 740) * mm, "radius": 3.4 * mm});
            skCircle(sketch, "E2.9.37.0", {"center": v(200, 760) * mm, "radius": 3.4 * mm});
            skCircle(sketch, "E2.9.38.0", {"center": v(200, 780) * mm, "radius": 3.4 * mm});
            skCircle(sketch, "E2.9.39.0", {"center": v(200, 800) * mm, "radius": 3.4 * mm});
            skCircle(sketch, "E2.9.40.0", {"center": v(200, 820) * mm, "radius": 3.4 * mm});
            skCircle(sketch, "E2.9.41.0", {"center": v(200, 840) * mm, "radius": 3.4 * mm});
            skCircle(sketch, "E2.9.42.0", {"center": v(200, 860) * mm, "radius": 3.4 * mm});
            skCircle(sketch, "E2.9.43.0", {"center": v(200, 880) * mm, "radius": 3.4 * mm});
            skCircle(sketch, "E2.9.44.0", {"center": v(200, 900) * mm, "radius": 3.4 * mm});
            skCircle(sketch, "E2.9.45.0", {"center": v(200, 920) * mm, "radius": 3.4 * mm});
            skCircle(sketch, "E2.9.46.0", {"center": v(200, 940) * mm, "radius": 3.4 * mm});
            skCircle(sketch, "E2.9.47.0", {"center": v(200, 960) * mm, "radius": 3.4 * mm});
            skCircle(sketch, "E2.9.48.0", {"center": v(200, 980) * mm, "radius": 3.4 * mm});
            skCircle(sketch, "E2.10.0.0", {"center": v(220, 20) * mm, "radius": 3.4 * mm});
            skCircle(sketch, "E2.10.1.0", {"center": v(220, 40) * mm, "radius": 3.4 * mm});
            skCircle(sketch, "E2.10.2.0", {"center": v(220, 60) * mm, "radius": 3.4 * mm});
            skCircle(sketch, "E2.10.3.0", {"center": v(220, 80) * mm, "radius": 3.4 * mm});
            skCircle(sketch, "E2.10.4.0", {"center": v(220, 100) * mm, "radius": 3.4 * mm});
            skCircle(sketch, "E2.10.5.0", {"center": v(220, 120) * mm, "radius": 3.4 * mm});
            skCircle(sketch, "E2.10.6.0", {"center": v(220, 140) * mm, "radius": 3.4 * mm});
            skCircle(sketch, "E2.10.7.0", {"center": v(220, 160) * mm, "radius": 3.4 * mm});
            skCircle(sketch, "E2.10.8.0", {"center": v(220, 180) * mm, "radius": 3.4 * mm});
            skCircle(sketch, "E2.10.9.0", {"center": v(220, 200) * mm, "radius": 3.4 * mm});
            skCircle(sketch, "E2.10.10.0", {"center": v(220, 220) * mm, "radius": 3.4 * mm});
            skCircle(sketch, "E2.10.11.0", {"center": v(220, 240) * mm, "radius": 3.4 * mm});
            skCircle(sketch, "E2.10.12.0", {"center": v(220, 260) * mm, "radius": 3.4 * mm});
            skCircle(sketch, "E2.10.13.0", {"center": v(220, 280) * mm, "radius": 3.4 * mm});
            skCircle(sketch, "E2.10.14.0", {"center": v(220, 300) * mm, "radius": 3.4 * mm});
            skCircle(sketch, "E2.10.15.0", {"center": v(220, 320) * mm, "radius": 3.4 * mm});
            skCircle(sketch, "E2.10.16.0", {"center": v(220, 340) * mm, "radius": 3.4 * mm});
            skCircle(sketch, "E2.10.17.0", {"center": v(220, 360) * mm, "radius": 3.4 * mm});
            skCircle(sketch, "E2.10.18.0", {"center": v(220, 380) * mm, "radius": 3.4 * mm});
            skCircle(sketch, "E2.10.19.0", {"center": v(220, 400) * mm, "radius": 3.4 * mm});
            skCircle(sketch, "E2.10.20.0", {"center": v(220, 420) * mm, "radius": 3.4 * mm});
            skCircle(sketch, "E2.10.21.0", {"center": v(220, 440) * mm, "radius": 3.4 * mm});
            skCircle(sketch, "E2.10.22.0", {"center": v(220, 460) * mm, "radius": 3.4 * mm});
            skCircle(sketch, "E2.10.23.0", {"center": v(220, 480) * mm, "radius": 3.4 * mm});
            skCircle(sketch, "E2.10.24.0", {"center": v(220, 500) * mm, "radius": 3.4 * mm});
            skCircle(sketch, "E2.10.25.0", {"center": v(220, 520) * mm, "radius": 3.4 * mm});
            skCircle(sketch, "E2.10.26.0", {"center": v(220, 540) * mm, "radius": 3.4 * mm});
            skCircle(sketch, "E2.10.27.0", {"center": v(220, 560) * mm, "radius": 3.4 * mm});
            skCircle(sketch, "E2.10.28.0", {"center": v(220, 580) * mm, "radius": 3.4 * mm});
            skCircle(sketch, "E2.10.29.0", {"center": v(220, 600) * mm, "radius": 3.4 * mm});
            skCircle(sketch, "E2.10.30.0", {"center": v(220, 620) * mm, "radius": 3.4 * mm});
            skCircle(sketch, "E2.10.31.0", {"center": v(220, 640) * mm, "radius": 3.4 * mm});
            skCircle(sketch, "E2.10.32.0", {"center": v(220, 660) * mm, "radius": 3.4 * mm});
            skCircle(sketch, "E2.10.33.0", {"center": v(220, 680) * mm, "radius": 3.4 * mm});
            skCircle(sketch, "E2.10.34.0", {"center": v(220, 700) * mm, "radius": 3.4 * mm});
            skCircle(sketch, "E2.10.35.0", {"center": v(220, 720) * mm, "radius": 3.4 * mm});
            skCircle(sketch, "E2.10.36.0", {"center": v(220, 740) * mm, "radius": 3.4 * mm});
            skCircle(sketch, "E2.10.37.0", {"center": v(220, 760) * mm, "radius": 3.4 * mm});
            skCircle(sketch, "E2.10.38.0", {"center": v(220, 780) * mm, "radius": 3.4 * mm});
            skCircle(sketch, "E2.10.39.0", {"center": v(220, 800) * mm, "radius": 3.4 * mm});
            skCircle(sketch, "E2.10.40.0", {"center": v(220, 820) * mm, "radius": 3.4 * mm});
            skCircle(sketch, "E2.10.41.0", {"center": v(220, 840) * mm, "radius": 3.4 * mm});
            skCircle(sketch, "E2.10.42.0", {"center": v(220, 860) * mm, "radius": 3.4 * mm});
            skCircle(sketch, "E2.10.43.0", {"center": v(220, 880) * mm, "radius": 3.4 * mm});
            skCircle(sketch, "E2.10.44.0", {"center": v(220, 900) * mm, "radius": 3.4 * mm});
            skCircle(sketch, "E2.10.45.0", {"center": v(220, 920) * mm, "radius": 3.4 * mm});
            skCircle(sketch, "E2.10.46.0", {"center": v(220, 940) * mm, "radius": 3.4 * mm});
            skCircle(sketch, "E2.10.47.0", {"center": v(220, 960) * mm, "radius": 3.4 * mm});
            skCircle(sketch, "E2.10.48.0", {"center": v(220, 980) * mm, "radius": 3.4 * mm});
            skCircle(sketch, "E2.11.0.0", {"center": v(240, 20) * mm, "radius": 3.4 * mm});
            skCircle(sketch, "E2.11.1.0", {"center": v(240, 40) * mm, "radius": 3.4 * mm});
            skCircle(sketch, "E2.11.2.0", {"center": v(240, 60) * mm, "radius": 3.4 * mm});
            skCircle(sketch, "E2.11.3.0", {"center": v(240, 80) * mm, "radius": 3.4 * mm});
            skCircle(sketch, "E2.11.4.0", {"center": v(240, 100) * mm, "radius": 3.4 * mm});
            skCircle(sketch, "E2.11.5.0", {"center": v(240, 120) * mm, "radius": 3.4 * mm});
            skCircle(sketch, "E2.11.6.0", {"center": v(240, 140) * mm, "radius": 3.4 * mm});
            skCircle(sketch, "E2.11.7.0", {"center": v(240, 160) * mm, "radius": 3.4 * mm});
            skCircle(sketch, "E2.11.8.0", {"center": v(240, 180) * mm, "radius": 3.4 * mm});
            skCircle(sketch, "E2.11.9.0", {"center": v(240, 200) * mm, "radius": 3.4 * mm});
            skCircle(sketch, "E2.11.10.0", {"center": v(240, 220) * mm, "radius": 3.4 * mm});
            skCircle(sketch, "E2.11.11.0", {"center": v(240, 240) * mm, "radius": 3.4 * mm});
            skCircle(sketch, "E2.11.12.0", {"center": v(240, 260) * mm, "radius": 3.4 * mm});
            skCircle(sketch, "E2.11.13.0", {"center": v(240, 280) * mm, "radius": 3.4 * mm});
            skCircle(sketch, "E2.11.14.0", {"center": v(240, 300) * mm, "radius": 3.4 * mm});
            skCircle(sketch, "E2.11.15.0", {"center": v(240, 320) * mm, "radius": 3.4 * mm});
            skCircle(sketch, "E2.11.16.0", {"center": v(240, 340) * mm, "radius": 3.4 * mm});
            skCircle(sketch, "E2.11.17.0", {"center": v(240, 360) * mm, "radius": 3.4 * mm});
            skCircle(sketch, "E2.11.18.0", {"center": v(240, 380) * mm, "radius": 3.4 * mm});
            skCircle(sketch, "E2.11.19.0", {"center": v(240, 400) * mm, "radius": 3.4 * mm});
            skCircle(sketch, "E2.11.20.0", {"center": v(240, 420) * mm, "radius": 3.4 * mm});
            skCircle(sketch, "E2.11.21.0", {"center": v(240, 440) * mm, "radius": 3.4 * mm});
            skCircle(sketch, "E2.11.22.0", {"center": v(240, 460) * mm, "radius": 3.4 * mm});
            skCircle(sketch, "E2.11.23.0", {"center": v(240, 480) * mm, "radius": 3.4 * mm});
            skCircle(sketch, "E2.11.24.0", {"center": v(240, 500) * mm, "radius": 3.4 * mm});
            skCircle(sketch, "E2.11.25.0", {"center": v(240, 520) * mm, "radius": 3.4 * mm});
            skCircle(sketch, "E2.11.26.0", {"center": v(240, 540) * mm, "radius": 3.4 * mm});
            skCircle(sketch, "E2.11.27.0", {"center": v(240, 560) * mm, "radius": 3.4 * mm});
            skCircle(sketch, "E2.11.28.0", {"center": v(240, 580) * mm, "radius": 3.4 * mm});
            skCircle(sketch, "E2.11.29.0", {"center": v(240, 600) * mm, "radius": 3.4 * mm});
            skCircle(sketch, "E2.11.30.0", {"center": v(240, 620) * mm, "radius": 3.4 * mm});
            skCircle(sketch, "E2.11.31.0", {"center": v(240, 640) * mm, "radius": 3.4 * mm});
            skCircle(sketch, "E2.11.32.0", {"center": v(240, 660) * mm, "radius": 3.4 * mm});
            skCircle(sketch, "E2.11.33.0", {"center": v(240, 680) * mm, "radius": 3.4 * mm});
            skCircle(sketch, "E2.11.34.0", {"center": v(240, 700) * mm, "radius": 3.4 * mm});
            skCircle(sketch, "E2.11.35.0", {"center": v(240, 720) * mm, "radius": 3.4 * mm});
            skCircle(sketch, "E2.11.36.0", {"center": v(240, 740) * mm, "radius": 3.4 * mm});
            skCircle(sketch, "E2.11.37.0", {"center": v(240, 760) * mm, "radius": 3.4 * mm});
            skCircle(sketch, "E2.11.38.0", {"center": v(240, 780) * mm, "radius": 3.4 * mm});
            skCircle(sketch, "E2.11.39.0", {"center": v(240, 800) * mm, "radius": 3.4 * mm});
            skCircle(sketch, "E2.11.40.0", {"center": v(240, 820) * mm, "radius": 3.4 * mm});
            skCircle(sketch, "E2.11.41.0", {"center": v(240, 840) * mm, "radius": 3.4 * mm});
            skCircle(sketch, "E2.11.42.0", {"center": v(240, 860) * mm, "radius": 3.4 * mm});
            skCircle(sketch, "E2.11.43.0", {"center": v(240, 880) * mm, "radius": 3.4 * mm});
            skCircle(sketch, "E2.11.44.0", {"center": v(240, 900) * mm, "radius": 3.4 * mm});
            skCircle(sketch, "E2.11.45.0", {"center": v(240, 920) * mm, "radius": 3.4 * mm});
            skCircle(sketch, "E2.11.46.0", {"center": v(240, 940) * mm, "radius": 3.4 * mm});
            skCircle(sketch, "E2.11.47.0", {"center": v(240, 960) * mm, "radius": 3.4 * mm});
            skCircle(sketch, "E2.11.48.0", {"center": v(240, 980) * mm, "radius": 3.4 * mm});
            skCircle(sketch, "E2.12.0.0", {"center": v(260, 20) * mm, "radius": 3.4 * mm});
            skCircle(sketch, "E2.12.1.0", {"center": v(260, 40) * mm, "radius": 3.4 * mm});
            skCircle(sketch, "E2.12.2.0", {"center": v(260, 60) * mm, "radius": 3.4 * mm});
            skCircle(sketch, "E2.12.3.0", {"center": v(260, 80) * mm, "radius": 3.4 * mm});
            skCircle(sketch, "E2.12.4.0", {"center": v(260, 100) * mm, "radius": 3.4 * mm});
            skCircle(sketch, "E2.12.5.0", {"center": v(260, 120) * mm, "radius": 3.4 * mm});
            skCircle(sketch, "E2.12.6.0", {"center": v(260, 140) * mm, "radius": 3.4 * mm});
            skCircle(sketch, "E2.12.7.0", {"center": v(260, 160) * mm, "radius": 3.4 * mm});
            skCircle(sketch, "E2.12.8.0", {"center": v(260, 180) * mm, "radius": 3.4 * mm});
            skCircle(sketch, "E2.12.9.0", {"center": v(260, 200) * mm, "radius": 3.4 * mm});
            skCircle(sketch, "E2.12.10.0", {"center": v(260, 220) * mm, "radius": 3.4 * mm});
            skCircle(sketch, "E2.12.11.0", {"center": v(260, 240) * mm, "radius": 3.4 * mm});
            skCircle(sketch, "E2.12.12.0", {"center": v(260, 260) * mm, "radius": 3.4 * mm});
            skCircle(sketch, "E2.12.13.0", {"center": v(260, 280) * mm, "radius": 3.4 * mm});
            skCircle(sketch, "E2.12.14.0", {"center": v(260, 300) * mm, "radius": 3.4 * mm});
            skCircle(sketch, "E2.12.15.0", {"center": v(260, 320) * mm, "radius": 3.4 * mm});
            skCircle(sketch, "E2.12.16.0", {"center": v(260, 340) * mm, "radius": 3.4 * mm});
            skCircle(sketch, "E2.12.17.0", {"center": v(260, 360) * mm, "radius": 3.4 * mm});
            skCircle(sketch, "E2.12.18.0", {"center": v(260, 380) * mm, "radius": 3.4 * mm});
            skCircle(sketch, "E2.12.19.0", {"center": v(260, 400) * mm, "radius": 3.4 * mm});
            skCircle(sketch, "E2.12.20.0", {"center": v(260, 420) * mm, "radius": 3.4 * mm});
            skCircle(sketch, "E2.12.21.0", {"center": v(260, 440) * mm, "radius": 3.4 * mm});
            skCircle(sketch, "E2.12.22.0", {"center": v(260, 460) * mm, "radius": 3.4 * mm});
            skCircle(sketch, "E2.12.23.0", {"center": v(260, 480) * mm, "radius": 3.4 * mm});
            skCircle(sketch, "E2.12.24.0", {"center": v(260, 500) * mm, "radius": 3.4 * mm});
            skCircle(sketch, "E2.12.25.0", {"center": v(260, 520) * mm, "radius": 3.4 * mm});
            skCircle(sketch, "E2.12.26.0", {"center": v(260, 540) * mm, "radius": 3.4 * mm});
            skCircle(sketch, "E2.12.27.0", {"center": v(260, 560) * mm, "radius": 3.4 * mm});
            skCircle(sketch, "E2.12.28.0", {"center": v(260, 580) * mm, "radius": 3.4 * mm});
            skCircle(sketch, "E2.12.29.0", {"center": v(260, 600) * mm, "radius": 3.4 * mm});
            skCircle(sketch, "E2.12.30.0", {"center": v(260, 620) * mm, "radius": 3.4 * mm});
            skCircle(sketch, "E2.12.31.0", {"center": v(260, 640) * mm, "radius": 3.4 * mm});
            skCircle(sketch, "E2.12.32.0", {"center": v(260, 660) * mm, "radius": 3.4 * mm});
            skCircle(sketch, "E2.12.33.0", {"center": v(260, 680) * mm, "radius": 3.4 * mm});
            skCircle(sketch, "E2.12.34.0", {"center": v(260, 700) * mm, "radius": 3.4 * mm});
            skCircle(sketch, "E2.12.35.0", {"center": v(260, 720) * mm, "radius": 3.4 * mm});
            skCircle(sketch, "E2.12.36.0", {"center": v(260, 740) * mm, "radius": 3.4 * mm});
            skCircle(sketch, "E2.12.37.0", {"center": v(260, 760) * mm, "radius": 3.4 * mm});
            skCircle(sketch, "E2.12.38.0", {"center": v(260, 780) * mm, "radius": 3.4 * mm});
            skCircle(sketch, "E2.12.39.0", {"center": v(260, 800) * mm, "radius": 3.4 * mm});
            skCircle(sketch, "E2.12.40.0", {"center": v(260, 820) * mm, "radius": 3.4 * mm});
            skCircle(sketch, "E2.12.41.0", {"center": v(260, 840) * mm, "radius": 3.4 * mm});
            skCircle(sketch, "E2.12.42.0", {"center": v(260, 860) * mm, "radius": 3.4 * mm});
            skCircle(sketch, "E2.12.43.0", {"center": v(260, 880) * mm, "radius": 3.4 * mm});
            skCircle(sketch, "E2.12.44.0", {"center": v(260, 900) * mm, "radius": 3.4 * mm});
            skCircle(sketch, "E2.12.45.0", {"center": v(260, 920) * mm, "radius": 3.4 * mm});
            skCircle(sketch, "E2.12.46.0", {"center": v(260, 940) * mm, "radius": 3.4 * mm});
            skCircle(sketch, "E2.12.47.0", {"center": v(260, 960) * mm, "radius": 3.4 * mm});
            skCircle(sketch, "E2.12.48.0", {"center": v(260, 980) * mm, "radius": 3.4 * mm});
            skCircle(sketch, "E2.13.0.0", {"center": v(280, 20) * mm, "radius": 3.4 * mm});
            skCircle(sketch, "E2.13.1.0", {"center": v(280, 40) * mm, "radius": 3.4 * mm});
            skCircle(sketch, "E2.13.2.0", {"center": v(280, 60) * mm, "radius": 3.4 * mm});
            skCircle(sketch, "E2.13.3.0", {"center": v(280, 80) * mm, "radius": 3.4 * mm});
            skCircle(sketch, "E2.13.4.0", {"center": v(280, 100) * mm, "radius": 3.4 * mm});
            skCircle(sketch, "E2.13.5.0", {"center": v(280, 120) * mm, "radius": 3.4 * mm});
            skCircle(sketch, "E2.13.6.0", {"center": v(280, 140) * mm, "radius": 3.4 * mm});
            skCircle(sketch, "E2.13.7.0", {"center": v(280, 160) * mm, "radius": 3.4 * mm});
            skCircle(sketch, "E2.13.8.0", {"center": v(280, 180) * mm, "radius": 3.4 * mm});
            skCircle(sketch, "E2.13.9.0", {"center": v(280, 200) * mm, "radius": 3.4 * mm});
            skCircle(sketch, "E2.13.10.0", {"center": v(280, 220) * mm, "radius": 3.4 * mm});
            skCircle(sketch, "E2.13.11.0", {"center": v(280, 240) * mm, "radius": 3.4 * mm});
            skCircle(sketch, "E2.13.12.0", {"center": v(280, 260) * mm, "radius": 3.4 * mm});
            skCircle(sketch, "E2.13.13.0", {"center": v(280, 280) * mm, "radius": 3.4 * mm});
            skCircle(sketch, "E2.13.14.0", {"center": v(280, 300) * mm, "radius": 3.4 * mm});
            skCircle(sketch, "E2.13.15.0", {"center": v(280, 320) * mm, "radius": 3.4 * mm});
            skCircle(sketch, "E2.13.16.0", {"center": v(280, 340) * mm, "radius": 3.4 * mm});
            skCircle(sketch, "E2.13.17.0", {"center": v(280, 360) * mm, "radius": 3.4 * mm});
            skCircle(sketch, "E2.13.18.0", {"center": v(280, 380) * mm, "radius": 3.4 * mm});
            skCircle(sketch, "E2.13.19.0", {"center": v(280, 400) * mm, "radius": 3.4 * mm});
            skCircle(sketch, "E2.13.20.0", {"center": v(280, 420) * mm, "radius": 3.4 * mm});
            skCircle(sketch, "E2.13.21.0", {"center": v(280, 440) * mm, "radius": 3.4 * mm});
            skCircle(sketch, "E2.13.22.0", {"center": v(280, 460) * mm, "radius": 3.4 * mm});
            skCircle(sketch, "E2.13.23.0", {"center": v(280, 480) * mm, "radius": 3.4 * mm});
            skCircle(sketch, "E2.13.24.0", {"center": v(280, 500) * mm, "radius": 3.4 * mm});
            skCircle(sketch, "E2.13.25.0", {"center": v(280, 520) * mm, "radius": 3.4 * mm});
            skCircle(sketch, "E2.13.26.0", {"center": v(280, 540) * mm, "radius": 3.4 * mm});
            skCircle(sketch, "E2.13.27.0", {"center": v(280, 560) * mm, "radius": 3.4 * mm});
            skCircle(sketch, "E2.13.28.0", {"center": v(280, 580) * mm, "radius": 3.4 * mm});
            skCircle(sketch, "E2.13.29.0", {"center": v(280, 600) * mm, "radius": 3.4 * mm});
            skCircle(sketch, "E2.13.30.0", {"center": v(280, 620) * mm, "radius": 3.4 * mm});
            skCircle(sketch, "E2.13.31.0", {"center": v(280, 640) * mm, "radius": 3.4 * mm});
            skCircle(sketch, "E2.13.32.0", {"center": v(280, 660) * mm, "radius": 3.4 * mm});
            skCircle(sketch, "E2.13.33.0", {"center": v(280, 680) * mm, "radius": 3.4 * mm});
            skCircle(sketch, "E2.13.34.0", {"center": v(280, 700) * mm, "radius": 3.4 * mm});
            skCircle(sketch, "E2.13.35.0", {"center": v(280, 720) * mm, "radius": 3.4 * mm});
            skCircle(sketch, "E2.13.36.0", {"center": v(280, 740) * mm, "radius": 3.4 * mm});
            skCircle(sketch, "E2.13.37.0", {"center": v(280, 760) * mm, "radius": 3.4 * mm});
            skCircle(sketch, "E2.13.38.0", {"center": v(280, 780) * mm, "radius": 3.4 * mm});
            skCircle(sketch, "E2.13.39.0", {"center": v(280, 800) * mm, "radius": 3.4 * mm});
            skCircle(sketch, "E2.13.40.0", {"center": v(280, 820) * mm, "radius": 3.4 * mm});
            skCircle(sketch, "E2.13.41.0", {"center": v(280, 840) * mm, "radius": 3.4 * mm});
            skCircle(sketch, "E2.13.42.0", {"center": v(280, 860) * mm, "radius": 3.4 * mm});
            skCircle(sketch, "E2.13.43.0", {"center": v(280, 880) * mm, "radius": 3.4 * mm});
            skCircle(sketch, "E2.13.44.0", {"center": v(280, 900) * mm, "radius": 3.4 * mm});
            skCircle(sketch, "E2.13.45.0", {"center": v(280, 920) * mm, "radius": 3.4 * mm});
            skCircle(sketch, "E2.13.46.0", {"center": v(280, 940) * mm, "radius": 3.4 * mm});
            skCircle(sketch, "E2.13.47.0", {"center": v(280, 960) * mm, "radius": 3.4 * mm});
            skCircle(sketch, "E2.13.48.0", {"center": v(280, 980) * mm, "radius": 3.4 * mm});
            skCircle(sketch, "E2.14.0.0", {"center": v(300, 20) * mm, "radius": 3.4 * mm});
            skCircle(sketch, "E2.14.1.0", {"center": v(300, 40) * mm, "radius": 3.4 * mm});
            skCircle(sketch, "E2.14.2.0", {"center": v(300, 60) * mm, "radius": 3.4 * mm});
            skCircle(sketch, "E2.14.3.0", {"center": v(300, 80) * mm, "radius": 3.4 * mm});
            skCircle(sketch, "E2.14.4.0", {"center": v(300, 100) * mm, "radius": 3.4 * mm});
            skCircle(sketch, "E2.14.5.0", {"center": v(300, 120) * mm, "radius": 3.4 * mm});
            skCircle(sketch, "E2.14.6.0", {"center": v(300, 140) * mm, "radius": 3.4 * mm});
            skCircle(sketch, "E2.14.7.0", {"center": v(300, 160) * mm, "radius": 3.4 * mm});
            skCircle(sketch, "E2.14.8.0", {"center": v(300, 180) * mm, "radius": 3.4 * mm});
            skCircle(sketch, "E2.14.9.0", {"center": v(300, 200) * mm, "radius": 3.4 * mm});
            skCircle(sketch, "E2.14.10.0", {"center": v(300, 220) * mm, "radius": 3.4 * mm});
            skCircle(sketch, "E2.14.11.0", {"center": v(300, 240) * mm, "radius": 3.4 * mm});
            skCircle(sketch, "E2.14.12.0", {"center": v(300, 260) * mm, "radius": 3.4 * mm});
            skCircle(sketch, "E2.14.13.0", {"center": v(300, 280) * mm, "radius": 3.4 * mm});
            skCircle(sketch, "E2.14.14.0", {"center": v(300, 300) * mm, "radius": 3.4 * mm});
            skCircle(sketch, "E2.14.15.0", {"center": v(300, 320) * mm, "radius": 3.4 * mm});
            skCircle(sketch, "E2.14.16.0", {"center": v(300, 340) * mm, "radius": 3.4 * mm});
            skCircle(sketch, "E2.14.17.0", {"center": v(300, 360) * mm, "radius": 3.4 * mm});
            skCircle(sketch, "E2.14.18.0", {"center": v(300, 380) * mm, "radius": 3.4 * mm});
            skCircle(sketch, "E2.14.19.0", {"center": v(300, 400) * mm, "radius": 3.4 * mm});
            skCircle(sketch, "E2.14.20.0", {"center": v(300, 420) * mm, "radius": 3.4 * mm});
            skCircle(sketch, "E2.14.21.0", {"center": v(300, 440) * mm, "radius": 3.4 * mm});
            skCircle(sketch, "E2.14.22.0", {"center": v(300, 460) * mm, "radius": 3.4 * mm});
            skCircle(sketch, "E2.14.23.0", {"center": v(300, 480) * mm, "radius": 3.4 * mm});
            skCircle(sketch, "E2.14.24.0", {"center": v(300, 500) * mm, "radius": 3.4 * mm});
            skCircle(sketch, "E2.14.25.0", {"center": v(300, 520) * mm, "radius": 3.4 * mm});
            skCircle(sketch, "E2.14.26.0", {"center": v(300, 540) * mm, "radius": 3.4 * mm});
            skCircle(sketch, "E2.14.27.0", {"center": v(300, 560) * mm, "radius": 3.4 * mm});
            skCircle(sketch, "E2.14.28.0", {"center": v(300, 580) * mm, "radius": 3.4 * mm});
            skCircle(sketch, "E2.14.29.0", {"center": v(300, 600) * mm, "radius": 3.4 * mm});
            skCircle(sketch, "E2.14.30.0", {"center": v(300, 620) * mm, "radius": 3.4 * mm});
            skCircle(sketch, "E2.14.31.0", {"center": v(300, 640) * mm, "radius": 3.4 * mm});
            skCircle(sketch, "E2.14.32.0", {"center": v(300, 660) * mm, "radius": 3.4 * mm});
            skCircle(sketch, "E2.14.33.0", {"center": v(300, 680) * mm, "radius": 3.4 * mm});
            skCircle(sketch, "E2.14.34.0", {"center": v(300, 700) * mm, "radius": 3.4 * mm});
            skCircle(sketch, "E2.14.35.0", {"center": v(300, 720) * mm, "radius": 3.4 * mm});
            skCircle(sketch, "E2.14.36.0", {"center": v(300, 740) * mm, "radius": 3.4 * mm});
            skCircle(sketch, "E2.14.37.0", {"center": v(300, 760) * mm, "radius": 3.4 * mm});
            skCircle(sketch, "E2.14.38.0", {"center": v(300, 780) * mm, "radius": 3.4 * mm});
            skCircle(sketch, "E2.14.39.0", {"center": v(300, 800) * mm, "radius": 3.4 * mm});
            skCircle(sketch, "E2.14.40.0", {"center": v(300, 820) * mm, "radius": 3.4 * mm});
            skCircle(sketch, "E2.14.41.0", {"center": v(300, 840) * mm, "radius": 3.4 * mm});
            skCircle(sketch, "E2.14.42.0", {"center": v(300, 860) * mm, "radius": 3.4 * mm});
            skCircle(sketch, "E2.14.43.0", {"center": v(300, 880) * mm, "radius": 3.4 * mm});
            skCircle(sketch, "E2.14.44.0", {"center": v(300, 900) * mm, "radius": 3.4 * mm});
            skCircle(sketch, "E2.14.45.0", {"center": v(300, 920) * mm, "radius": 3.4 * mm});
            skCircle(sketch, "E2.14.46.0", {"center": v(300, 940) * mm, "radius": 3.4 * mm});
            skCircle(sketch, "E2.14.47.0", {"center": v(300, 960) * mm, "radius": 3.4 * mm});
            skCircle(sketch, "E2.14.48.0", {"center": v(300, 980) * mm, "radius": 3.4 * mm});
            skCircle(sketch, "E2.15.0.0", {"center": v(320, 20) * mm, "radius": 3.4 * mm});
            skCircle(sketch, "E2.15.1.0", {"center": v(320, 40) * mm, "radius": 3.4 * mm});
            skCircle(sketch, "E2.15.2.0", {"center": v(320, 60) * mm, "radius": 3.4 * mm});
            skCircle(sketch, "E2.15.3.0", {"center": v(320, 80) * mm, "radius": 3.4 * mm});
            skCircle(sketch, "E2.15.4.0", {"center": v(320, 100) * mm, "radius": 3.4 * mm});
            skCircle(sketch, "E2.15.5.0", {"center": v(320, 120) * mm, "radius": 3.4 * mm});
            skCircle(sketch, "E2.15.6.0", {"center": v(320, 140) * mm, "radius": 3.4 * mm});
            skCircle(sketch, "E2.15.7.0", {"center": v(320, 160) * mm, "radius": 3.4 * mm});
            skCircle(sketch, "E2.15.8.0", {"center": v(320, 180) * mm, "radius": 3.4 * mm});
            skCircle(sketch, "E2.15.9.0", {"center": v(320, 200) * mm, "radius": 3.4 * mm});
            skCircle(sketch, "E2.15.10.0", {"center": v(320, 220) * mm, "radius": 3.4 * mm});
            skCircle(sketch, "E2.15.11.0", {"center": v(320, 240) * mm, "radius": 3.4 * mm});
            skCircle(sketch, "E2.15.12.0", {"center": v(320, 260) * mm, "radius": 3.4 * mm});
            skCircle(sketch, "E2.15.13.0", {"center": v(320, 280) * mm, "radius": 3.4 * mm});
            skCircle(sketch, "E2.15.14.0", {"center": v(320, 300) * mm, "radius": 3.4 * mm});
            skCircle(sketch, "E2.15.15.0", {"center": v(320, 320) * mm, "radius": 3.4 * mm});
            skCircle(sketch, "E2.15.16.0", {"center": v(320, 340) * mm, "radius": 3.4 * mm});
            skCircle(sketch, "E2.15.17.0", {"center": v(320, 360) * mm, "radius": 3.4 * mm});
            skCircle(sketch, "E2.15.18.0", {"center": v(320, 380) * mm, "radius": 3.4 * mm});
            skCircle(sketch, "E2.15.19.0", {"center": v(320, 400) * mm, "radius": 3.4 * mm});
            skCircle(sketch, "E2.15.20.0", {"center": v(320, 420) * mm, "radius": 3.4 * mm});
            skCircle(sketch, "E2.15.21.0", {"center": v(320, 440) * mm, "radius": 3.4 * mm});
            skCircle(sketch, "E2.15.22.0", {"center": v(320, 460) * mm, "radius": 3.4 * mm});
            skCircle(sketch, "E2.15.23.0", {"center": v(320, 480) * mm, "radius": 3.4 * mm});
            skCircle(sketch, "E2.15.24.0", {"center": v(320, 500) * mm, "radius": 3.4 * mm});
            skCircle(sketch, "E2.15.25.0", {"center": v(320, 520) * mm, "radius": 3.4 * mm});
            skCircle(sketch, "E2.15.26.0", {"center": v(320, 540) * mm, "radius": 3.4 * mm});
            skCircle(sketch, "E2.15.27.0", {"center": v(320, 560) * mm, "radius": 3.4 * mm});
            skCircle(sketch, "E2.15.28.0", {"center": v(320, 580) * mm, "radius": 3.4 * mm});
            skCircle(sketch, "E2.15.29.0", {"center": v(320, 600) * mm, "radius": 3.4 * mm});
            skCircle(sketch, "E2.15.30.0", {"center": v(320, 620) * mm, "radius": 3.4 * mm});
            skCircle(sketch, "E2.15.31.0", {"center": v(320, 640) * mm, "radius": 3.4 * mm});
            skCircle(sketch, "E2.15.32.0", {"center": v(320, 660) * mm, "radius": 3.4 * mm});
            skCircle(sketch, "E2.15.33.0", {"center": v(320, 680) * mm, "radius": 3.4 * mm});
            skCircle(sketch, "E2.15.34.0", {"center": v(320, 700) * mm, "radius": 3.4 * mm});
            skCircle(sketch, "E2.15.35.0", {"center": v(320, 720) * mm, "radius": 3.4 * mm});
            skCircle(sketch, "E2.15.36.0", {"center": v(320, 740) * mm, "radius": 3.4 * mm});
            skCircle(sketch, "E2.15.37.0", {"center": v(320, 760) * mm, "radius": 3.4 * mm});
            skCircle(sketch, "E2.15.38.0", {"center": v(320, 780) * mm, "radius": 3.4 * mm});
            skCircle(sketch, "E2.15.39.0", {"center": v(320, 800) * mm, "radius": 3.4 * mm});
            skCircle(sketch, "E2.15.40.0", {"center": v(320, 820) * mm, "radius": 3.4 * mm});
            skCircle(sketch, "E2.15.41.0", {"center": v(320, 840) * mm, "radius": 3.4 * mm});
            skCircle(sketch, "E2.15.42.0", {"center": v(320, 860) * mm, "radius": 3.4 * mm});
            skCircle(sketch, "E2.15.43.0", {"center": v(320, 880) * mm, "radius": 3.4 * mm});
            skCircle(sketch, "E2.15.44.0", {"center": v(320, 900) * mm, "radius": 3.4 * mm});
            skCircle(sketch, "E2.15.45.0", {"center": v(320, 920) * mm, "radius": 3.4 * mm});
            skCircle(sketch, "E2.15.46.0", {"center": v(320, 940) * mm, "radius": 3.4 * mm});
            skCircle(sketch, "E2.15.47.0", {"center": v(320, 960) * mm, "radius": 3.4 * mm});
            skCircle(sketch, "E2.15.48.0", {"center": v(320, 980) * mm, "radius": 3.4 * mm});
            skCircle(sketch, "E2.16.0.0", {"center": v(340, 20) * mm, "radius": 3.4 * mm});
            skCircle(sketch, "E2.16.1.0", {"center": v(340, 40) * mm, "radius": 3.4 * mm});
            skCircle(sketch, "E2.16.2.0", {"center": v(340, 60) * mm, "radius": 3.4 * mm});
            skCircle(sketch, "E2.16.3.0", {"center": v(340, 80) * mm, "radius": 3.4 * mm});
            skCircle(sketch, "E2.16.4.0", {"center": v(340, 100) * mm, "radius": 3.4 * mm});
            skCircle(sketch, "E2.16.5.0", {"center": v(340, 120) * mm, "radius": 3.4 * mm});
            skCircle(sketch, "E2.16.6.0", {"center": v(340, 140) * mm, "radius": 3.4 * mm});
            skCircle(sketch, "E2.16.7.0", {"center": v(340, 160) * mm, "radius": 3.4 * mm});
            skCircle(sketch, "E2.16.8.0", {"center": v(340, 180) * mm, "radius": 3.4 * mm});
            skCircle(sketch, "E2.16.9.0", {"center": v(340, 200) * mm, "radius": 3.4 * mm});
            skCircle(sketch, "E2.16.10.0", {"center": v(340, 220) * mm, "radius": 3.4 * mm});
            skCircle(sketch, "E2.16.11.0", {"center": v(340, 240) * mm, "radius": 3.4 * mm});
            skCircle(sketch, "E2.16.12.0", {"center": v(340, 260) * mm, "radius": 3.4 * mm});
            skCircle(sketch, "E2.16.13.0", {"center": v(340, 280) * mm, "radius": 3.4 * mm});
            skCircle(sketch, "E2.16.14.0", {"center": v(340, 300) * mm, "radius": 3.4 * mm});
            skCircle(sketch, "E2.16.15.0", {"center": v(340, 320) * mm, "radius": 3.4 * mm});
            skCircle(sketch, "E2.16.16.0", {"center": v(340, 340) * mm, "radius": 3.4 * mm});
            skCircle(sketch, "E2.16.17.0", {"center": v(340, 360) * mm, "radius": 3.4 * mm});
            skCircle(sketch, "E2.16.18.0", {"center": v(340, 380) * mm, "radius": 3.4 * mm});
            skCircle(sketch, "E2.16.19.0", {"center": v(340, 400) * mm, "radius": 3.4 * mm});
            skCircle(sketch, "E2.16.20.0", {"center": v(340, 420) * mm, "radius": 3.4 * mm});
            skCircle(sketch, "E2.16.21.0", {"center": v(340, 440) * mm, "radius": 3.4 * mm});
            skCircle(sketch, "E2.16.22.0", {"center": v(340, 460) * mm, "radius": 3.4 * mm});
            skCircle(sketch, "E2.16.23.0", {"center": v(340, 480) * mm, "radius": 3.4 * mm});
            skCircle(sketch, "E2.16.24.0", {"center": v(340, 500) * mm, "radius": 3.4 * mm});
            skCircle(sketch, "E2.16.25.0", {"center": v(340, 520) * mm, "radius": 3.4 * mm});
            skCircle(sketch, "E2.16.26.0", {"center": v(340, 540) * mm, "radius": 3.4 * mm});
            skCircle(sketch, "E2.16.27.0", {"center": v(340, 560) * mm, "radius": 3.4 * mm});
            skCircle(sketch, "E2.16.28.0", {"center": v(340, 580) * mm, "radius": 3.4 * mm});
            skCircle(sketch, "E2.16.29.0", {"center": v(340, 600) * mm, "radius": 3.4 * mm});
            skCircle(sketch, "E2.16.30.0", {"center": v(340, 620) * mm, "radius": 3.4 * mm});
            skCircle(sketch, "E2.16.31.0", {"center": v(340, 640) * mm, "radius": 3.4 * mm});
            skCircle(sketch, "E2.16.32.0", {"center": v(340, 660) * mm, "radius": 3.4 * mm});
            skCircle(sketch, "E2.16.33.0", {"center": v(340, 680) * mm, "radius": 3.4 * mm});
            skCircle(sketch, "E2.16.34.0", {"center": v(340, 700) * mm, "radius": 3.4 * mm});
            skCircle(sketch, "E2.16.35.0", {"center": v(340, 720) * mm, "radius": 3.4 * mm});
            skCircle(sketch, "E2.16.36.0", {"center": v(340, 740) * mm, "radius": 3.4 * mm});
            skCircle(sketch, "E2.16.37.0", {"center": v(340, 760) * mm, "radius": 3.4 * mm});
            skCircle(sketch, "E2.16.38.0", {"center": v(340, 780) * mm, "radius": 3.4 * mm});
            skCircle(sketch, "E2.16.39.0", {"center": v(340, 800) * mm, "radius": 3.4 * mm});
            skCircle(sketch, "E2.16.40.0", {"center": v(340, 820) * mm, "radius": 3.4 * mm});
            skCircle(sketch, "E2.16.41.0", {"center": v(340, 840) * mm, "radius": 3.4 * mm});
            skCircle(sketch, "E2.16.42.0", {"center": v(340, 860) * mm, "radius": 3.4 * mm});
            skCircle(sketch, "E2.16.43.0", {"center": v(340, 880) * mm, "radius": 3.4 * mm});
            skCircle(sketch, "E2.16.44.0", {"center": v(340, 900) * mm, "radius": 3.4 * mm});
            skCircle(sketch, "E2.16.45.0", {"center": v(340, 920) * mm, "radius": 3.4 * mm});
            skCircle(sketch, "E2.16.46.0", {"center": v(340, 940) * mm, "radius": 3.4 * mm});
            skCircle(sketch, "E2.16.47.0", {"center": v(340, 960) * mm, "radius": 3.4 * mm});
            skCircle(sketch, "E2.16.48.0", {"center": v(340, 980) * mm, "radius": 3.4 * mm});
            skCircle(sketch, "E2.17.0.0", {"center": v(360, 20) * mm, "radius": 3.4 * mm});
            skCircle(sketch, "E2.17.1.0", {"center": v(360, 40) * mm, "radius": 3.4 * mm});
            skCircle(sketch, "E2.17.2.0", {"center": v(360, 60) * mm, "radius": 3.4 * mm});
            skCircle(sketch, "E2.17.3.0", {"center": v(360, 80) * mm, "radius": 3.4 * mm});
            skCircle(sketch, "E2.17.4.0", {"center": v(360, 100) * mm, "radius": 3.4 * mm});
            skCircle(sketch, "E2.17.5.0", {"center": v(360, 120) * mm, "radius": 3.4 * mm});
            skCircle(sketch, "E2.17.6.0", {"center": v(360, 140) * mm, "radius": 3.4 * mm});
            skCircle(sketch, "E2.17.7.0", {"center": v(360, 160) * mm, "radius": 3.4 * mm});
            skCircle(sketch, "E2.17.8.0", {"center": v(360, 180) * mm, "radius": 3.4 * mm});
            skCircle(sketch, "E2.17.9.0", {"center": v(360, 200) * mm, "radius": 3.4 * mm});
            skCircle(sketch, "E2.17.10.0", {"center": v(360, 220) * mm, "radius": 3.4 * mm});
            skCircle(sketch, "E2.17.11.0", {"center": v(360, 240) * mm, "radius": 3.4 * mm});
            skCircle(sketch, "E2.17.12.0", {"center": v(360, 260) * mm, "radius": 3.4 * mm});
            skCircle(sketch, "E2.17.13.0", {"center": v(360, 280) * mm, "radius": 3.4 * mm});
            skCircle(sketch, "E2.17.14.0", {"center": v(360, 300) * mm, "radius": 3.4 * mm});
            skCircle(sketch, "E2.17.15.0", {"center": v(360, 320) * mm, "radius": 3.4 * mm});
            skCircle(sketch, "E2.17.16.0", {"center": v(360, 340) * mm, "radius": 3.4 * mm});
            skCircle(sketch, "E2.17.17.0", {"center": v(360, 360) * mm, "radius": 3.4 * mm});
            skCircle(sketch, "E2.17.18.0", {"center": v(360, 380) * mm, "radius": 3.4 * mm});
            skCircle(sketch, "E2.17.19.0", {"center": v(360, 400) * mm, "radius": 3.4 * mm});
            skCircle(sketch, "E2.17.20.0", {"center": v(360, 420) * mm, "radius": 3.4 * mm});
            skCircle(sketch, "E2.17.21.0", {"center": v(360, 440) * mm, "radius": 3.4 * mm});
            skCircle(sketch, "E2.17.22.0", {"center": v(360, 460) * mm, "radius": 3.4 * mm});
            skCircle(sketch, "E2.17.23.0", {"center": v(360, 480) * mm, "radius": 3.4 * mm});
            skCircle(sketch, "E2.17.24.0", {"center": v(360, 500) * mm, "radius": 3.4 * mm});
            skCircle(sketch, "E2.17.25.0", {"center": v(360, 520) * mm, "radius": 3.4 * mm});
            skCircle(sketch, "E2.17.26.0", {"center": v(360, 540) * mm, "radius": 3.4 * mm});
            skCircle(sketch, "E2.17.27.0", {"center": v(360, 560) * mm, "radius": 3.4 * mm});
            skCircle(sketch, "E2.17.28.0", {"center": v(360, 580) * mm, "radius": 3.4 * mm});
            skCircle(sketch, "E2.17.29.0", {"center": v(360, 600) * mm, "radius": 3.4 * mm});
            skCircle(sketch, "E2.17.30.0", {"center": v(360, 620) * mm, "radius": 3.4 * mm});
            skCircle(sketch, "E2.17.31.0", {"center": v(360, 640) * mm, "radius": 3.4 * mm});
            skCircle(sketch, "E2.17.32.0", {"center": v(360, 660) * mm, "radius": 3.4 * mm});
            skCircle(sketch, "E2.17.33.0", {"center": v(360, 680) * mm, "radius": 3.4 * mm});
            skCircle(sketch, "E2.17.34.0", {"center": v(360, 700) * mm, "radius": 3.4 * mm});
            skCircle(sketch, "E2.17.35.0", {"center": v(360, 720) * mm, "radius": 3.4 * mm});
            skCircle(sketch, "E2.17.36.0", {"center": v(360, 740) * mm, "radius": 3.4 * mm});
            skCircle(sketch, "E2.17.37.0", {"center": v(360, 760) * mm, "radius": 3.4 * mm});
            skCircle(sketch, "E2.17.38.0", {"center": v(360, 780) * mm, "radius": 3.4 * mm});
            skCircle(sketch, "E2.17.39.0", {"center": v(360, 800) * mm, "radius": 3.4 * mm});
            skCircle(sketch, "E2.17.40.0", {"center": v(360, 820) * mm, "radius": 3.4 * mm});
            skCircle(sketch, "E2.17.41.0", {"center": v(360, 840) * mm, "radius": 3.4 * mm});
            skCircle(sketch, "E2.17.42.0", {"center": v(360, 860) * mm, "radius": 3.4 * mm});
            skCircle(sketch, "E2.17.43.0", {"center": v(360, 880) * mm, "radius": 3.4 * mm});
            skCircle(sketch, "E2.17.44.0", {"center": v(360, 900) * mm, "radius": 3.4 * mm});
            skCircle(sketch, "E2.17.45.0", {"center": v(360, 920) * mm, "radius": 3.4 * mm});
            skCircle(sketch, "E2.17.46.0", {"center": v(360, 940) * mm, "radius": 3.4 * mm});
            skCircle(sketch, "E2.17.47.0", {"center": v(360, 960) * mm, "radius": 3.4 * mm});
            skCircle(sketch, "E2.17.48.0", {"center": v(360, 980) * mm, "radius": 3.4 * mm});
            skCircle(sketch, "E2.18.0.0", {"center": v(380, 20) * mm, "radius": 3.4 * mm});
            skCircle(sketch, "E2.18.1.0", {"center": v(380, 40) * mm, "radius": 3.4 * mm});
            skCircle(sketch, "E2.18.2.0", {"center": v(380, 60) * mm, "radius": 3.4 * mm});
            skCircle(sketch, "E2.18.3.0", {"center": v(380, 80) * mm, "radius": 3.4 * mm});
            skCircle(sketch, "E2.18.4.0", {"center": v(380, 100) * mm, "radius": 3.4 * mm});
            skCircle(sketch, "E2.18.5.0", {"center": v(380, 120) * mm, "radius": 3.4 * mm});
            skCircle(sketch, "E2.18.6.0", {"center": v(380, 140) * mm, "radius": 3.4 * mm});
            skCircle(sketch, "E2.18.7.0", {"center": v(380, 160) * mm, "radius": 3.4 * mm});
            skCircle(sketch, "E2.18.8.0", {"center": v(380, 180) * mm, "radius": 3.4 * mm});
            skCircle(sketch, "E2.18.9.0", {"center": v(380, 200) * mm, "radius": 3.4 * mm});
            skCircle(sketch, "E2.18.10.0", {"center": v(380, 220) * mm, "radius": 3.4 * mm});
            skCircle(sketch, "E2.18.11.0", {"center": v(380, 240) * mm, "radius": 3.4 * mm});
            skCircle(sketch, "E2.18.12.0", {"center": v(380, 260) * mm, "radius": 3.4 * mm});
            skCircle(sketch, "E2.18.13.0", {"center": v(380, 280) * mm, "radius": 3.4 * mm});
            skCircle(sketch, "E2.18.14.0", {"center": v(380, 300) * mm, "radius": 3.4 * mm});
            skCircle(sketch, "E2.18.15.0", {"center": v(380, 320) * mm, "radius": 3.4 * mm});
            skCircle(sketch, "E2.18.16.0", {"center": v(380, 340) * mm, "radius": 3.4 * mm});
            skCircle(sketch, "E2.18.17.0", {"center": v(380, 360) * mm, "radius": 3.4 * mm});
            skCircle(sketch, "E2.18.18.0", {"center": v(380, 380) * mm, "radius": 3.4 * mm});
            skCircle(sketch, "E2.18.19.0", {"center": v(380, 400) * mm, "radius": 3.4 * mm});
            skCircle(sketch, "E2.18.20.0", {"center": v(380, 420) * mm, "radius": 3.4 * mm});
            skCircle(sketch, "E2.18.21.0", {"center": v(380, 440) * mm, "radius": 3.4 * mm});
            skCircle(sketch, "E2.18.22.0", {"center": v(380, 460) * mm, "radius": 3.4 * mm});
            skCircle(sketch, "E2.18.23.0", {"center": v(380, 480) * mm, "radius": 3.4 * mm});
            skCircle(sketch, "E2.18.24.0", {"center": v(380, 500) * mm, "radius": 3.4 * mm});
            skCircle(sketch, "E2.18.25.0", {"center": v(380, 520) * mm, "radius": 3.4 * mm});
            skCircle(sketch, "E2.18.26.0", {"center": v(380, 540) * mm, "radius": 3.4 * mm});
            skCircle(sketch, "E2.18.27.0", {"center": v(380, 560) * mm, "radius": 3.4 * mm});
            skCircle(sketch, "E2.18.28.0", {"center": v(380, 580) * mm, "radius": 3.4 * mm});
            skCircle(sketch, "E2.18.29.0", {"center": v(380, 600) * mm, "radius": 3.4 * mm});
            skCircle(sketch, "E2.18.30.0", {"center": v(380, 620) * mm, "radius": 3.4 * mm});
            skCircle(sketch, "E2.18.31.0", {"center": v(380, 640) * mm, "radius": 3.4 * mm});
            skCircle(sketch, "E2.18.32.0", {"center": v(380, 660) * mm, "radius": 3.4 * mm});
            skCircle(sketch, "E2.18.33.0", {"center": v(380, 680) * mm, "radius": 3.4 * mm});
            skCircle(sketch, "E2.18.34.0", {"center": v(380, 700) * mm, "radius": 3.4 * mm});
            skCircle(sketch, "E2.18.35.0", {"center": v(380, 720) * mm, "radius": 3.4 * mm});
            skCircle(sketch, "E2.18.36.0", {"center": v(380, 740) * mm, "radius": 3.4 * mm});
            skCircle(sketch, "E2.18.37.0", {"center": v(380, 760) * mm, "radius": 3.4 * mm});
            skCircle(sketch, "E2.18.38.0", {"center": v(380, 780) * mm, "radius": 3.4 * mm});
            skCircle(sketch, "E2.18.39.0", {"center": v(380, 800) * mm, "radius": 3.4 * mm});
            skCircle(sketch, "E2.18.40.0", {"center": v(380, 820) * mm, "radius": 3.4 * mm});
            skCircle(sketch, "E2.18.41.0", {"center": v(380, 840) * mm, "radius": 3.4 * mm});
            skCircle(sketch, "E2.18.42.0", {"center": v(380, 860) * mm, "radius": 3.4 * mm});
            skCircle(sketch, "E2.18.43.0", {"center": v(380, 880) * mm, "radius": 3.4 * mm});
            skCircle(sketch, "E2.18.44.0", {"center": v(380, 900) * mm, "radius": 3.4 * mm});
            skCircle(sketch, "E2.18.45.0", {"center": v(380, 920) * mm, "radius": 3.4 * mm});
            skCircle(sketch, "E2.18.46.0", {"center": v(380, 940) * mm, "radius": 3.4 * mm});
            skCircle(sketch, "E2.18.47.0", {"center": v(380, 960) * mm, "radius": 3.4 * mm});
            skCircle(sketch, "E2.18.48.0", {"center": v(380, 980) * mm, "radius": 3.4 * mm});
            skCircle(sketch, "E2.19.0.0", {"center": v(400, 20) * mm, "radius": 3.4 * mm});
            skCircle(sketch, "E2.19.1.0", {"center": v(400, 40) * mm, "radius": 3.4 * mm});
            skCircle(sketch, "E2.19.2.0", {"center": v(400, 60) * mm, "radius": 3.4 * mm});
            skCircle(sketch, "E2.19.3.0", {"center": v(400, 80) * mm, "radius": 3.4 * mm});
            skCircle(sketch, "E2.19.4.0", {"center": v(400, 100) * mm, "radius": 3.4 * mm});
            skCircle(sketch, "E2.19.5.0", {"center": v(400, 120) * mm, "radius": 3.4 * mm});
            skCircle(sketch, "E2.19.6.0", {"center": v(400, 140) * mm, "radius": 3.4 * mm});
            skCircle(sketch, "E2.19.7.0", {"center": v(400, 160) * mm, "radius": 3.4 * mm});
            skCircle(sketch, "E2.19.8.0", {"center": v(400, 180) * mm, "radius": 3.4 * mm});
            skCircle(sketch, "E2.19.9.0", {"center": v(400, 200) * mm, "radius": 3.4 * mm});
            skCircle(sketch, "E2.19.10.0", {"center": v(400, 220) * mm, "radius": 3.4 * mm});
            skCircle(sketch, "E2.19.11.0", {"center": v(400, 240) * mm, "radius": 3.4 * mm});
            skCircle(sketch, "E2.19.12.0", {"center": v(400, 260) * mm, "radius": 3.4 * mm});
            skCircle(sketch, "E2.19.13.0", {"center": v(400, 280) * mm, "radius": 3.4 * mm});
            skCircle(sketch, "E2.19.14.0", {"center": v(400, 300) * mm, "radius": 3.4 * mm});
            skCircle(sketch, "E2.19.15.0", {"center": v(400, 320) * mm, "radius": 3.4 * mm});
            skCircle(sketch, "E2.19.16.0", {"center": v(400, 340) * mm, "radius": 3.4 * mm});
            skCircle(sketch, "E2.19.17.0", {"center": v(400, 360) * mm, "radius": 3.4 * mm});
            skCircle(sketch, "E2.19.18.0", {"center": v(400, 380) * mm, "radius": 3.4 * mm});
            skCircle(sketch, "E2.19.19.0", {"center": v(400, 400) * mm, "radius": 3.4 * mm});
            skCircle(sketch, "E2.19.20.0", {"center": v(400, 420) * mm, "radius": 3.4 * mm});
            skCircle(sketch, "E2.19.21.0", {"center": v(400, 440) * mm, "radius": 3.4 * mm});
            skCircle(sketch, "E2.19.22.0", {"center": v(400, 460) * mm, "radius": 3.4 * mm});
            skCircle(sketch, "E2.19.23.0", {"center": v(400, 480) * mm, "radius": 3.4 * mm});
            skCircle(sketch, "E2.19.24.0", {"center": v(400, 500) * mm, "radius": 3.4 * mm});
            skCircle(sketch, "E2.19.25.0", {"center": v(400, 520) * mm, "radius": 3.4 * mm});
            skCircle(sketch, "E2.19.26.0", {"center": v(400, 540) * mm, "radius": 3.4 * mm});
            skCircle(sketch, "E2.19.27.0", {"center": v(400, 560) * mm, "radius": 3.4 * mm});
            skCircle(sketch, "E2.19.28.0", {"center": v(400, 580) * mm, "radius": 3.4 * mm});
            skCircle(sketch, "E2.19.29.0", {"center": v(400, 600) * mm, "radius": 3.4 * mm});
            skCircle(sketch, "E2.19.30.0", {"center": v(400, 620) * mm, "radius": 3.4 * mm});
            skCircle(sketch, "E2.19.31.0", {"center": v(400, 640) * mm, "radius": 3.4 * mm});
            skCircle(sketch, "E2.19.32.0", {"center": v(400, 660) * mm, "radius": 3.4 * mm});
            skCircle(sketch, "E2.19.33.0", {"center": v(400, 680) * mm, "radius": 3.4 * mm});
            skCircle(sketch, "E2.19.34.0", {"center": v(400, 700) * mm, "radius": 3.4 * mm});
            skCircle(sketch, "E2.19.35.0", {"center": v(400, 720) * mm, "radius": 3.4 * mm});
            skCircle(sketch, "E2.19.36.0", {"center": v(400, 740) * mm, "radius": 3.4 * mm});
            skCircle(sketch, "E2.19.37.0", {"center": v(400, 760) * mm, "radius": 3.4 * mm});
            skCircle(sketch, "E2.19.38.0", {"center": v(400, 780) * mm, "radius": 3.4 * mm});
            skCircle(sketch, "E2.19.39.0", {"center": v(400, 800) * mm, "radius": 3.4 * mm});
            skCircle(sketch, "E2.19.40.0", {"center": v(400, 820) * mm, "radius": 3.4 * mm});
            skCircle(sketch, "E2.19.41.0", {"center": v(400, 840) * mm, "radius": 3.4 * mm});
            skCircle(sketch, "E2.19.42.0", {"center": v(400, 860) * mm, "radius": 3.4 * mm});
            skCircle(sketch, "E2.19.43.0", {"center": v(400, 880) * mm, "radius": 3.4 * mm});
            skCircle(sketch, "E2.19.44.0", {"center": v(400, 900) * mm, "radius": 3.4 * mm});
            skCircle(sketch, "E2.19.45.0", {"center": v(400, 920) * mm, "radius": 3.4 * mm});
            skCircle(sketch, "E2.19.46.0", {"center": v(400, 940) * mm, "radius": 3.4 * mm});
            skCircle(sketch, "E2.19.47.0", {"center": v(400, 960) * mm, "radius": 3.4 * mm});
            skCircle(sketch, "E2.19.48.0", {"center": v(400, 980) * mm, "radius": 3.4 * mm});
            skCircle(sketch, "E2.20.0.0", {"center": v(420, 20) * mm, "radius": 3.4 * mm});
            skCircle(sketch, "E2.20.1.0", {"center": v(420, 40) * mm, "radius": 3.4 * mm});
            skCircle(sketch, "E2.20.2.0", {"center": v(420, 60) * mm, "radius": 3.4 * mm});
            skCircle(sketch, "E2.20.3.0", {"center": v(420, 80) * mm, "radius": 3.4 * mm});
            skCircle(sketch, "E2.20.4.0", {"center": v(420, 100) * mm, "radius": 3.4 * mm});
            skCircle(sketch, "E2.20.5.0", {"center": v(420, 120) * mm, "radius": 3.4 * mm});
            skCircle(sketch, "E2.20.6.0", {"center": v(420, 140) * mm, "radius": 3.4 * mm});
            skCircle(sketch, "E2.20.7.0", {"center": v(420, 160) * mm, "radius": 3.4 * mm});
            skCircle(sketch, "E2.20.8.0", {"center": v(420, 180) * mm, "radius": 3.4 * mm});
            skCircle(sketch, "E2.20.9.0", {"center": v(420, 200) * mm, "radius": 3.4 * mm});
            skCircle(sketch, "E2.20.10.0", {"center": v(420, 220) * mm, "radius": 3.4 * mm});
            skCircle(sketch, "E2.20.11.0", {"center": v(420, 240) * mm, "radius": 3.4 * mm});
            skCircle(sketch, "E2.20.12.0", {"center": v(420, 260) * mm, "radius": 3.4 * mm});
            skCircle(sketch, "E2.20.13.0", {"center": v(420, 280) * mm, "radius": 3.4 * mm});
            skCircle(sketch, "E2.20.14.0", {"center": v(420, 300) * mm, "radius": 3.4 * mm});
            skCircle(sketch, "E2.20.15.0", {"center": v(420, 320) * mm, "radius": 3.4 * mm});
            skCircle(sketch, "E2.20.16.0", {"center": v(420, 340) * mm, "radius": 3.4 * mm});
            skCircle(sketch, "E2.20.17.0", {"center": v(420, 360) * mm, "radius": 3.4 * mm});
            skCircle(sketch, "E2.20.18.0", {"center": v(420, 380) * mm, "radius": 3.4 * mm});
            skCircle(sketch, "E2.20.19.0", {"center": v(420, 400) * mm, "radius": 3.4 * mm});
            skCircle(sketch, "E2.20.20.0", {"center": v(420, 420) * mm, "radius": 3.4 * mm});
            skCircle(sketch, "E2.20.21.0", {"center": v(420, 440) * mm, "radius": 3.4 * mm});
            skCircle(sketch, "E2.20.22.0", {"center": v(420, 460) * mm, "radius": 3.4 * mm});
            skCircle(sketch, "E2.20.23.0", {"center": v(420, 480) * mm, "radius": 3.4 * mm});
            skCircle(sketch, "E2.20.24.0", {"center": v(420, 500) * mm, "radius": 3.4 * mm});
            skCircle(sketch, "E2.20.25.0", {"center": v(420, 520) * mm, "radius": 3.4 * mm});
            skCircle(sketch, "E2.20.26.0", {"center": v(420, 540) * mm, "radius": 3.4 * mm});
            skCircle(sketch, "E2.20.27.0", {"center": v(420, 560) * mm, "radius": 3.4 * mm});
            skCircle(sketch, "E2.20.28.0", {"center": v(420, 580) * mm, "radius": 3.4 * mm});
            skCircle(sketch, "E2.20.29.0", {"center": v(420, 600) * mm, "radius": 3.4 * mm});
            skCircle(sketch, "E2.20.30.0", {"center": v(420, 620) * mm, "radius": 3.4 * mm});
            skCircle(sketch, "E2.20.31.0", {"center": v(420, 640) * mm, "radius": 3.4 * mm});
            skCircle(sketch, "E2.20.32.0", {"center": v(420, 660) * mm, "radius": 3.4 * mm});
            skCircle(sketch, "E2.20.33.0", {"center": v(420, 680) * mm, "radius": 3.4 * mm});
            skCircle(sketch, "E2.20.34.0", {"center": v(420, 700) * mm, "radius": 3.4 * mm});
            skCircle(sketch, "E2.20.35.0", {"center": v(420, 720) * mm, "radius": 3.4 * mm});
            skCircle(sketch, "E2.20.36.0", {"center": v(420, 740) * mm, "radius": 3.4 * mm});
            skCircle(sketch, "E2.20.37.0", {"center": v(420, 760) * mm, "radius": 3.4 * mm});
            skCircle(sketch, "E2.20.38.0", {"center": v(420, 780) * mm, "radius": 3.4 * mm});
            skCircle(sketch, "E2.20.39.0", {"center": v(420, 800) * mm, "radius": 3.4 * mm});
            skCircle(sketch, "E2.20.40.0", {"center": v(420, 820) * mm, "radius": 3.4 * mm});
            skCircle(sketch, "E2.20.41.0", {"center": v(420, 840) * mm, "radius": 3.4 * mm});
            skCircle(sketch, "E2.20.42.0", {"center": v(420, 860) * mm, "radius": 3.4 * mm});
            skCircle(sketch, "E2.20.43.0", {"center": v(420, 880) * mm, "radius": 3.4 * mm});
            skCircle(sketch, "E2.20.44.0", {"center": v(420, 900) * mm, "radius": 3.4 * mm});
            skCircle(sketch, "E2.20.45.0", {"center": v(420, 920) * mm, "radius": 3.4 * mm});
            skCircle(sketch, "E2.20.46.0", {"center": v(420, 940) * mm, "radius": 3.4 * mm});
            skCircle(sketch, "E2.20.47.0", {"center": v(420, 960) * mm, "radius": 3.4 * mm});
            skCircle(sketch, "E2.20.48.0", {"center": v(420, 980) * mm, "radius": 3.4 * mm});
            skCircle(sketch, "E2.21.0.0", {"center": v(440, 20) * mm, "radius": 3.4 * mm});
            skCircle(sketch, "E2.21.1.0", {"center": v(440, 40) * mm, "radius": 3.4 * mm});
            skCircle(sketch, "E2.21.2.0", {"center": v(440, 60) * mm, "radius": 3.4 * mm});
            skCircle(sketch, "E2.21.3.0", {"center": v(440, 80) * mm, "radius": 3.4 * mm});
            skCircle(sketch, "E2.21.4.0", {"center": v(440, 100) * mm, "radius": 3.4 * mm});
            skCircle(sketch, "E2.21.5.0", {"center": v(440, 120) * mm, "radius": 3.4 * mm});
            skCircle(sketch, "E2.21.6.0", {"center": v(440, 140) * mm, "radius": 3.4 * mm});
            skCircle(sketch, "E2.21.7.0", {"center": v(440, 160) * mm, "radius": 3.4 * mm});
            skCircle(sketch, "E2.21.8.0", {"center": v(440, 180) * mm, "radius": 3.4 * mm});
            skCircle(sketch, "E2.21.9.0", {"center": v(440, 200) * mm, "radius": 3.4 * mm});
            skCircle(sketch, "E2.21.10.0", {"center": v(440, 220) * mm, "radius": 3.4 * mm});
            skCircle(sketch, "E2.21.11.0", {"center": v(440, 240) * mm, "radius": 3.4 * mm});
            skCircle(sketch, "E2.21.12.0", {"center": v(440, 260) * mm, "radius": 3.4 * mm});
            skCircle(sketch, "E2.21.13.0", {"center": v(440, 280) * mm, "radius": 3.4 * mm});
            skCircle(sketch, "E2.21.14.0", {"center": v(440, 300) * mm, "radius": 3.4 * mm});
            skCircle(sketch, "E2.21.15.0", {"center": v(440, 320) * mm, "radius": 3.4 * mm});
            skCircle(sketch, "E2.21.16.0", {"center": v(440, 340) * mm, "radius": 3.4 * mm});
            skCircle(sketch, "E2.21.17.0", {"center": v(440, 360) * mm, "radius": 3.4 * mm});
            skCircle(sketch, "E2.21.18.0", {"center": v(440, 380) * mm, "radius": 3.4 * mm});
            skCircle(sketch, "E2.21.19.0", {"center": v(440, 400) * mm, "radius": 3.4 * mm});
            skCircle(sketch, "E2.21.20.0", {"center": v(440, 420) * mm, "radius": 3.4 * mm});
            skCircle(sketch, "E2.21.21.0", {"center": v(440, 440) * mm, "radius": 3.4 * mm});
            skCircle(sketch, "E2.21.22.0", {"center": v(440, 460) * mm, "radius": 3.4 * mm});
            skCircle(sketch, "E2.21.23.0", {"center": v(440, 480) * mm, "radius": 3.4 * mm});
            skCircle(sketch, "E2.21.24.0", {"center": v(440, 500) * mm, "radius": 3.4 * mm});
            skCircle(sketch, "E2.21.25.0", {"center": v(440, 520) * mm, "radius": 3.4 * mm});
            skCircle(sketch, "E2.21.26.0", {"center": v(440, 540) * mm, "radius": 3.4 * mm});
            skCircle(sketch, "E2.21.27.0", {"center": v(440, 560) * mm, "radius": 3.4 * mm});
            skCircle(sketch, "E2.21.28.0", {"center": v(440, 580) * mm, "radius": 3.4 * mm});
            skCircle(sketch, "E2.21.29.0", {"center": v(440, 600) * mm, "radius": 3.4 * mm});
            skCircle(sketch, "E2.21.30.0", {"center": v(440, 620) * mm, "radius": 3.4 * mm});
            skCircle(sketch, "E2.21.31.0", {"center": v(440, 640) * mm, "radius": 3.4 * mm});
            skCircle(sketch, "E2.21.32.0", {"center": v(440, 660) * mm, "radius": 3.4 * mm});
            skCircle(sketch, "E2.21.33.0", {"center": v(440, 680) * mm, "radius": 3.4 * mm});
            skCircle(sketch, "E2.21.34.0", {"center": v(440, 700) * mm, "radius": 3.4 * mm});
            skCircle(sketch, "E2.21.35.0", {"center": v(440, 720) * mm, "radius": 3.4 * mm});
            skCircle(sketch, "E2.21.36.0", {"center": v(440, 740) * mm, "radius": 3.4 * mm});
            skCircle(sketch, "E2.21.37.0", {"center": v(440, 760) * mm, "radius": 3.4 * mm});
            skCircle(sketch, "E2.21.38.0", {"center": v(440, 780) * mm, "radius": 3.4 * mm});
            skCircle(sketch, "E2.21.39.0", {"center": v(440, 800) * mm, "radius": 3.4 * mm});
            skCircle(sketch, "E2.21.40.0", {"center": v(440, 820) * mm, "radius": 3.4 * mm});
            skCircle(sketch, "E2.21.41.0", {"center": v(440, 840) * mm, "radius": 3.4 * mm});
            skCircle(sketch, "E2.21.42.0", {"center": v(440, 860) * mm, "radius": 3.4 * mm});
            skCircle(sketch, "E2.21.43.0", {"center": v(440, 880) * mm, "radius": 3.4 * mm});
            skCircle(sketch, "E2.21.44.0", {"center": v(440, 900) * mm, "radius": 3.4 * mm});
            skCircle(sketch, "E2.21.45.0", {"center": v(440, 920) * mm, "radius": 3.4 * mm});
            skCircle(sketch, "E2.21.46.0", {"center": v(440, 940) * mm, "radius": 3.4 * mm});
            skCircle(sketch, "E2.21.47.0", {"center": v(440, 960) * mm, "radius": 3.4 * mm});
            skCircle(sketch, "E2.21.48.0", {"center": v(440, 980) * mm, "radius": 3.4 * mm});
            skCircle(sketch, "E2.22.0.0", {"center": v(460, 20) * mm, "radius": 3.4 * mm});
            skCircle(sketch, "E2.22.1.0", {"center": v(460, 40) * mm, "radius": 3.4 * mm});
            skCircle(sketch, "E2.22.2.0", {"center": v(460, 60) * mm, "radius": 3.4 * mm});
            skCircle(sketch, "E2.22.3.0", {"center": v(460, 80) * mm, "radius": 3.4 * mm});
            skCircle(sketch, "E2.22.4.0", {"center": v(460, 100) * mm, "radius": 3.4 * mm});
            skCircle(sketch, "E2.22.5.0", {"center": v(460, 120) * mm, "radius": 3.4 * mm});
            skCircle(sketch, "E2.22.6.0", {"center": v(460, 140) * mm, "radius": 3.4 * mm});
            skCircle(sketch, "E2.22.7.0", {"center": v(460, 160) * mm, "radius": 3.4 * mm});
            skCircle(sketch, "E2.22.8.0", {"center": v(460, 180) * mm, "radius": 3.4 * mm});
            skCircle(sketch, "E2.22.9.0", {"center": v(460, 200) * mm, "radius": 3.4 * mm});
            skCircle(sketch, "E2.22.10.0", {"center": v(460, 220) * mm, "radius": 3.4 * mm});
            skCircle(sketch, "E2.22.11.0", {"center": v(460, 240) * mm, "radius": 3.4 * mm});
            skCircle(sketch, "E2.22.12.0", {"center": v(460, 260) * mm, "radius": 3.4 * mm});
            skCircle(sketch, "E2.22.13.0", {"center": v(460, 280) * mm, "radius": 3.4 * mm});
            skCircle(sketch, "E2.22.14.0", {"center": v(460, 300) * mm, "radius": 3.4 * mm});
            skCircle(sketch, "E2.22.15.0", {"center": v(460, 320) * mm, "radius": 3.4 * mm});
            skCircle(sketch, "E2.22.16.0", {"center": v(460, 340) * mm, "radius": 3.4 * mm});
            skCircle(sketch, "E2.22.17.0", {"center": v(460, 360) * mm, "radius": 3.4 * mm});
            skCircle(sketch, "E2.22.18.0", {"center": v(460, 380) * mm, "radius": 3.4 * mm});
            skCircle(sketch, "E2.22.19.0", {"center": v(460, 400) * mm, "radius": 3.4 * mm});
            skCircle(sketch, "E2.22.20.0", {"center": v(460, 420) * mm, "radius": 3.4 * mm});
            skCircle(sketch, "E2.22.21.0", {"center": v(460, 440) * mm, "radius": 3.4 * mm});
            skCircle(sketch, "E2.22.22.0", {"center": v(460, 460) * mm, "radius": 3.4 * mm});
            skCircle(sketch, "E2.22.23.0", {"center": v(460, 480) * mm, "radius": 3.4 * mm});
            skCircle(sketch, "E2.22.24.0", {"center": v(460, 500) * mm, "radius": 3.4 * mm});
            skCircle(sketch, "E2.22.25.0", {"center": v(460, 520) * mm, "radius": 3.4 * mm});
            skCircle(sketch, "E2.22.26.0", {"center": v(460, 540) * mm, "radius": 3.4 * mm});
            skCircle(sketch, "E2.22.27.0", {"center": v(460, 560) * mm, "radius": 3.4 * mm});
            skCircle(sketch, "E2.22.28.0", {"center": v(460, 580) * mm, "radius": 3.4 * mm});
            skCircle(sketch, "E2.22.29.0", {"center": v(460, 600) * mm, "radius": 3.4 * mm});
            skCircle(sketch, "E2.22.30.0", {"center": v(460, 620) * mm, "radius": 3.4 * mm});
            skCircle(sketch, "E2.22.31.0", {"center": v(460, 640) * mm, "radius": 3.4 * mm});
            skCircle(sketch, "E2.22.32.0", {"center": v(460, 660) * mm, "radius": 3.4 * mm});
            skCircle(sketch, "E2.22.33.0", {"center": v(460, 680) * mm, "radius": 3.4 * mm});
            skCircle(sketch, "E2.22.34.0", {"center": v(460, 700) * mm, "radius": 3.4 * mm});
            skCircle(sketch, "E2.22.35.0", {"center": v(460, 720) * mm, "radius": 3.4 * mm});
            skCircle(sketch, "E2.22.36.0", {"center": v(460, 740) * mm, "radius": 3.4 * mm});
            skCircle(sketch, "E2.22.37.0", {"center": v(460, 760) * mm, "radius": 3.4 * mm});
            skCircle(sketch, "E2.22.38.0", {"center": v(460, 780) * mm, "radius": 3.4 * mm});
            skCircle(sketch, "E2.22.39.0", {"center": v(460, 800) * mm, "radius": 3.4 * mm});
            skCircle(sketch, "E2.22.40.0", {"center": v(460, 820) * mm, "radius": 3.4 * mm});
            skCircle(sketch, "E2.22.41.0", {"center": v(460, 840) * mm, "radius": 3.4 * mm});
            skCircle(sketch, "E2.22.42.0", {"center": v(460, 860) * mm, "radius": 3.4 * mm});
            skCircle(sketch, "E2.22.43.0", {"center": v(460, 880) * mm, "radius": 3.4 * mm});
            skCircle(sketch, "E2.22.44.0", {"center": v(460, 900) * mm, "radius": 3.4 * mm});
            skCircle(sketch, "E2.22.45.0", {"center": v(460, 920) * mm, "radius": 3.4 * mm});
            skCircle(sketch, "E2.22.46.0", {"center": v(460, 940) * mm, "radius": 3.4 * mm});
            skCircle(sketch, "E2.22.47.0", {"center": v(460, 960) * mm, "radius": 3.4 * mm});
            skCircle(sketch, "E2.22.48.0", {"center": v(460, 980) * mm, "radius": 3.4 * mm});
            skCircle(sketch, "E2.23.0.0", {"center": v(480, 20) * mm, "radius": 3.4 * mm});
            skCircle(sketch, "E2.23.1.0", {"center": v(480, 40) * mm, "radius": 3.4 * mm});
            skCircle(sketch, "E2.23.2.0", {"center": v(480, 60) * mm, "radius": 3.4 * mm});
            skCircle(sketch, "E2.23.3.0", {"center": v(480, 80) * mm, "radius": 3.4 * mm});
            skCircle(sketch, "E2.23.4.0", {"center": v(480, 100) * mm, "radius": 3.4 * mm});
            skCircle(sketch, "E2.23.5.0", {"center": v(480, 120) * mm, "radius": 3.4 * mm});
            skCircle(sketch, "E2.23.6.0", {"center": v(480, 140) * mm, "radius": 3.4 * mm});
            skCircle(sketch, "E2.23.7.0", {"center": v(480, 160) * mm, "radius": 3.4 * mm});
            skCircle(sketch, "E2.23.8.0", {"center": v(480, 180) * mm, "radius": 3.4 * mm});
            skCircle(sketch, "E2.23.9.0", {"center": v(480, 200) * mm, "radius": 3.4 * mm});
            skCircle(sketch, "E2.23.10.0", {"center": v(480, 220) * mm, "radius": 3.4 * mm});
            skCircle(sketch, "E2.23.11.0", {"center": v(480, 240) * mm, "radius": 3.4 * mm});
            skCircle(sketch, "E2.23.12.0", {"center": v(480, 260) * mm, "radius": 3.4 * mm});
            skCircle(sketch, "E2.23.13.0", {"center": v(480, 280) * mm, "radius": 3.4 * mm});
            skCircle(sketch, "E2.23.14.0", {"center": v(480, 300) * mm, "radius": 3.4 * mm});
            skCircle(sketch, "E2.23.15.0", {"center": v(480, 320) * mm, "radius": 3.4 * mm});
            skCircle(sketch, "E2.23.16.0", {"center": v(480, 340) * mm, "radius": 3.4 * mm});
            skCircle(sketch, "E2.23.17.0", {"center": v(480, 360) * mm, "radius": 3.4 * mm});
            skCircle(sketch, "E2.23.18.0", {"center": v(480, 380) * mm, "radius": 3.4 * mm});
            skCircle(sketch, "E2.23.19.0", {"center": v(480, 400) * mm, "radius": 3.4 * mm});
            skCircle(sketch, "E2.23.20.0", {"center": v(480, 420) * mm, "radius": 3.4 * mm});
            skCircle(sketch, "E2.23.21.0", {"center": v(480, 440) * mm, "radius": 3.4 * mm});
            skCircle(sketch, "E2.23.22.0", {"center": v(480, 460) * mm, "radius": 3.4 * mm});
            skCircle(sketch, "E2.23.23.0", {"center": v(480, 480) * mm, "radius": 3.4 * mm});
            skCircle(sketch, "E2.23.24.0", {"center": v(480, 500) * mm, "radius": 3.4 * mm});
            skCircle(sketch, "E2.23.25.0", {"center": v(480, 520) * mm, "radius": 3.4 * mm});
            skCircle(sketch, "E2.23.26.0", {"center": v(480, 540) * mm, "radius": 3.4 * mm});
            skCircle(sketch, "E2.23.27.0", {"center": v(480, 560) * mm, "radius": 3.4 * mm});
            skCircle(sketch, "E2.23.28.0", {"center": v(480, 580) * mm, "radius": 3.4 * mm});
            skCircle(sketch, "E2.23.29.0", {"center": v(480, 600) * mm, "radius": 3.4 * mm});
            skCircle(sketch, "E2.23.30.0", {"center": v(480, 620) * mm, "radius": 3.4 * mm});
            skCircle(sketch, "E2.23.31.0", {"center": v(480, 640) * mm, "radius": 3.4 * mm});
            skCircle(sketch, "E2.23.32.0", {"center": v(480, 660) * mm, "radius": 3.4 * mm});
            skCircle(sketch, "E2.23.33.0", {"center": v(480, 680) * mm, "radius": 3.4 * mm});
            skCircle(sketch, "E2.23.34.0", {"center": v(480, 700) * mm, "radius": 3.4 * mm});
            skCircle(sketch, "E2.23.35.0", {"center": v(480, 720) * mm, "radius": 3.4 * mm});
            skCircle(sketch, "E2.23.36.0", {"center": v(480, 740) * mm, "radius": 3.4 * mm});
            skCircle(sketch, "E2.23.37.0", {"center": v(480, 760) * mm, "radius": 3.4 * mm});
            skCircle(sketch, "E2.23.38.0", {"center": v(480, 780) * mm, "radius": 3.4 * mm});
            skCircle(sketch, "E2.23.39.0", {"center": v(480, 800) * mm, "radius": 3.4 * mm});
            skCircle(sketch, "E2.23.40.0", {"center": v(480, 820) * mm, "radius": 3.4 * mm});
            skCircle(sketch, "E2.23.41.0", {"center": v(480, 840) * mm, "radius": 3.4 * mm});
            skCircle(sketch, "E2.23.42.0", {"center": v(480, 860) * mm, "radius": 3.4 * mm});
            skCircle(sketch, "E2.23.43.0", {"center": v(480, 880) * mm, "radius": 3.4 * mm});
            skCircle(sketch, "E2.23.44.0", {"center": v(480, 900) * mm, "radius": 3.4 * mm});
            skCircle(sketch, "E2.23.45.0", {"center": v(480, 920) * mm, "radius": 3.4 * mm});
            skCircle(sketch, "E2.23.46.0", {"center": v(480, 940) * mm, "radius": 3.4 * mm});
            skCircle(sketch, "E2.23.47.0", {"center": v(480, 960) * mm, "radius": 3.4 * mm});
            skCircle(sketch, "E2.23.48.0", {"center": v(480, 980) * mm, "radius": 3.4 * mm});
            skCircle(sketch, "E2.24.0.0", {"center": v(500, 20) * mm, "radius": 3.4 * mm});
            skCircle(sketch, "E2.24.1.0", {"center": v(500, 40) * mm, "radius": 3.4 * mm});
            skCircle(sketch, "E2.24.2.0", {"center": v(500, 60) * mm, "radius": 3.4 * mm});
            skCircle(sketch, "E2.24.3.0", {"center": v(500, 80) * mm, "radius": 3.4 * mm});
            skCircle(sketch, "E2.24.4.0", {"center": v(500, 100) * mm, "radius": 3.4 * mm});
            skCircle(sketch, "E2.24.5.0", {"center": v(500, 120) * mm, "radius": 3.4 * mm});
            skCircle(sketch, "E2.24.6.0", {"center": v(500, 140) * mm, "radius": 3.4 * mm});
            skCircle(sketch, "E2.24.7.0", {"center": v(500, 160) * mm, "radius": 3.4 * mm});
            skCircle(sketch, "E2.24.8.0", {"center": v(500, 180) * mm, "radius": 3.4 * mm});
            skCircle(sketch, "E2.24.9.0", {"center": v(500, 200) * mm, "radius": 3.4 * mm});
            skCircle(sketch, "E2.24.10.0", {"center": v(500, 220) * mm, "radius": 3.4 * mm});
            skCircle(sketch, "E2.24.11.0", {"center": v(500, 240) * mm, "radius": 3.4 * mm});
            skCircle(sketch, "E2.24.12.0", {"center": v(500, 260) * mm, "radius": 3.4 * mm});
            skCircle(sketch, "E2.24.13.0", {"center": v(500, 280) * mm, "radius": 3.4 * mm});
            skCircle(sketch, "E2.24.14.0", {"center": v(500, 300) * mm, "radius": 3.4 * mm});
            skCircle(sketch, "E2.24.15.0", {"center": v(500, 320) * mm, "radius": 3.4 * mm});
            skCircle(sketch, "E2.24.16.0", {"center": v(500, 340) * mm, "radius": 3.4 * mm});
            skCircle(sketch, "E2.24.17.0", {"center": v(500, 360) * mm, "radius": 3.4 * mm});
            skCircle(sketch, "E2.24.18.0", {"center": v(500, 380) * mm, "radius": 3.4 * mm});
            skCircle(sketch, "E2.24.19.0", {"center": v(500, 400) * mm, "radius": 3.4 * mm});
            skCircle(sketch, "E2.24.20.0", {"center": v(500, 420) * mm, "radius": 3.4 * mm});
            skCircle(sketch, "E2.24.21.0", {"center": v(500, 440) * mm, "radius": 3.4 * mm});
            skCircle(sketch, "E2.24.22.0", {"center": v(500, 460) * mm, "radius": 3.4 * mm});
            skCircle(sketch, "E2.24.23.0", {"center": v(500, 480) * mm, "radius": 3.4 * mm});
            skCircle(sketch, "E2.24.24.0", {"center": v(500, 500) * mm, "radius": 3.4 * mm});
            skCircle(sketch, "E2.24.25.0", {"center": v(500, 520) * mm, "radius": 3.4 * mm});
            skCircle(sketch, "E2.24.26.0", {"center": v(500, 540) * mm, "radius": 3.4 * mm});
            skCircle(sketch, "E2.24.27.0", {"center": v(500, 560) * mm, "radius": 3.4 * mm});
            skCircle(sketch, "E2.24.28.0", {"center": v(500, 580) * mm, "radius": 3.4 * mm});
            skCircle(sketch, "E2.24.29.0", {"center": v(500, 600) * mm, "radius": 3.4 * mm});
            skCircle(sketch, "E2.24.30.0", {"center": v(500, 620) * mm, "radius": 3.4 * mm});
            skCircle(sketch, "E2.24.31.0", {"center": v(500, 640) * mm, "radius": 3.4 * mm});
            skCircle(sketch, "E2.24.32.0", {"center": v(500, 660) * mm, "radius": 3.4 * mm});
            skCircle(sketch, "E2.24.33.0", {"center": v(500, 680) * mm, "radius": 3.4 * mm});
            skCircle(sketch, "E2.24.34.0", {"center": v(500, 700) * mm, "radius": 3.4 * mm});
            skCircle(sketch, "E2.24.35.0", {"center": v(500, 720) * mm, "radius": 3.4 * mm});
            skCircle(sketch, "E2.24.36.0", {"center": v(500, 740) * mm, "radius": 3.4 * mm});
            skCircle(sketch, "E2.24.37.0", {"center": v(500, 760) * mm, "radius": 3.4 * mm});
            skCircle(sketch, "E2.24.38.0", {"center": v(500, 780) * mm, "radius": 3.4 * mm});
            skCircle(sketch, "E2.24.39.0", {"center": v(500, 800) * mm, "radius": 3.4 * mm});
            skCircle(sketch, "E2.24.40.0", {"center": v(500, 820) * mm, "radius": 3.4 * mm});
            skCircle(sketch, "E2.24.41.0", {"center": v(500, 840) * mm, "radius": 3.4 * mm});
            skCircle(sketch, "E2.24.42.0", {"center": v(500, 860) * mm, "radius": 3.4 * mm});
            skCircle(sketch, "E2.24.43.0", {"center": v(500, 880) * mm, "radius": 3.4 * mm});
            skCircle(sketch, "E2.24.44.0", {"center": v(500, 900) * mm, "radius": 3.4 * mm});
            skCircle(sketch, "E2.24.45.0", {"center": v(500, 920) * mm, "radius": 3.4 * mm});
            skCircle(sketch, "E2.24.46.0", {"center": v(500, 940) * mm, "radius": 3.4 * mm});
            skCircle(sketch, "E2.24.47.0", {"center": v(500, 960) * mm, "radius": 3.4 * mm});
            skCircle(sketch, "E2.24.48.0", {"center": v(500, 980) * mm, "radius": 3.4 * mm});
            skCircle(sketch, "E2.25.0.0", {"center": v(520, 20) * mm, "radius": 3.4 * mm});
            skCircle(sketch, "E2.25.1.0", {"center": v(520, 40) * mm, "radius": 3.4 * mm});
            skCircle(sketch, "E2.25.2.0", {"center": v(520, 60) * mm, "radius": 3.4 * mm});
            skCircle(sketch, "E2.25.3.0", {"center": v(520, 80) * mm, "radius": 3.4 * mm});
            skCircle(sketch, "E2.25.4.0", {"center": v(520, 100) * mm, "radius": 3.4 * mm});
            skCircle(sketch, "E2.25.5.0", {"center": v(520, 120) * mm, "radius": 3.4 * mm});
            skCircle(sketch, "E2.25.6.0", {"center": v(520, 140) * mm, "radius": 3.4 * mm});
            skCircle(sketch, "E2.25.7.0", {"center": v(520, 160) * mm, "radius": 3.4 * mm});
            skCircle(sketch, "E2.25.8.0", {"center": v(520, 180) * mm, "radius": 3.4 * mm});
            skCircle(sketch, "E2.25.9.0", {"center": v(520, 200) * mm, "radius": 3.4 * mm});
            skCircle(sketch, "E2.25.10.0", {"center": v(520, 220) * mm, "radius": 3.4 * mm});
            skCircle(sketch, "E2.25.11.0", {"center": v(520, 240) * mm, "radius": 3.4 * mm});
            skCircle(sketch, "E2.25.12.0", {"center": v(520, 260) * mm, "radius": 3.4 * mm});
            skCircle(sketch, "E2.25.13.0", {"center": v(520, 280) * mm, "radius": 3.4 * mm});
            skCircle(sketch, "E2.25.14.0", {"center": v(520, 300) * mm, "radius": 3.4 * mm});
            skCircle(sketch, "E2.25.15.0", {"center": v(520, 320) * mm, "radius": 3.4 * mm});
            skCircle(sketch, "E2.25.16.0", {"center": v(520, 340) * mm, "radius": 3.4 * mm});
            skCircle(sketch, "E2.25.17.0", {"center": v(520, 360) * mm, "radius": 3.4 * mm});
            skCircle(sketch, "E2.25.18.0", {"center": v(520, 380) * mm, "radius": 3.4 * mm});
            skCircle(sketch, "E2.25.19.0", {"center": v(520, 400) * mm, "radius": 3.4 * mm});
            skCircle(sketch, "E2.25.20.0", {"center": v(520, 420) * mm, "radius": 3.4 * mm});
            skCircle(sketch, "E2.25.21.0", {"center": v(520, 440) * mm, "radius": 3.4 * mm});
            skCircle(sketch, "E2.25.22.0", {"center": v(520, 460) * mm, "radius": 3.4 * mm});
            skCircle(sketch, "E2.25.23.0", {"center": v(520, 480) * mm, "radius": 3.4 * mm});
            skCircle(sketch, "E2.25.24.0", {"center": v(520, 500) * mm, "radius": 3.4 * mm});
            skCircle(sketch, "E2.25.25.0", {"center": v(520, 520) * mm, "radius": 3.4 * mm});
            skCircle(sketch, "E2.25.26.0", {"center": v(520, 540) * mm, "radius": 3.4 * mm});
            skCircle(sketch, "E2.25.27.0", {"center": v(520, 560) * mm, "radius": 3.4 * mm});
            skCircle(sketch, "E2.25.28.0", {"center": v(520, 580) * mm, "radius": 3.4 * mm});
            skCircle(sketch, "E2.25.29.0", {"center": v(520, 600) * mm, "radius": 3.4 * mm});
            skCircle(sketch, "E2.25.30.0", {"center": v(520, 620) * mm, "radius": 3.4 * mm});
            skCircle(sketch, "E2.25.31.0", {"center": v(520, 640) * mm, "radius": 3.4 * mm});
            skCircle(sketch, "E2.25.32.0", {"center": v(520, 660) * mm, "radius": 3.4 * mm});
            skCircle(sketch, "E2.25.33.0", {"center": v(520, 680) * mm, "radius": 3.4 * mm});
            skCircle(sketch, "E2.25.34.0", {"center": v(520, 700) * mm, "radius": 3.4 * mm});
            skCircle(sketch, "E2.25.35.0", {"center": v(520, 720) * mm, "radius": 3.4 * mm});
            skCircle(sketch, "E2.25.36.0", {"center": v(520, 740) * mm, "radius": 3.4 * mm});
            skCircle(sketch, "E2.25.37.0", {"center": v(520, 760) * mm, "radius": 3.4 * mm});
            skCircle(sketch, "E2.25.38.0", {"center": v(520, 780) * mm, "radius": 3.4 * mm});
            skCircle(sketch, "E2.25.39.0", {"center": v(520, 800) * mm, "radius": 3.4 * mm});
            skCircle(sketch, "E2.25.40.0", {"center": v(520, 820) * mm, "radius": 3.4 * mm});
            skCircle(sketch, "E2.25.41.0", {"center": v(520, 840) * mm, "radius": 3.4 * mm});
            skCircle(sketch, "E2.25.42.0", {"center": v(520, 860) * mm, "radius": 3.4 * mm});
            skCircle(sketch, "E2.25.43.0", {"center": v(520, 880) * mm, "radius": 3.4 * mm});
            skCircle(sketch, "E2.25.44.0", {"center": v(520, 900) * mm, "radius": 3.4 * mm});
            skCircle(sketch, "E2.25.45.0", {"center": v(520, 920) * mm, "radius": 3.4 * mm});
            skCircle(sketch, "E2.25.46.0", {"center": v(520, 940) * mm, "radius": 3.4 * mm});
            skCircle(sketch, "E2.25.47.0", {"center": v(520, 960) * mm, "radius": 3.4 * mm});
            skCircle(sketch, "E2.25.48.0", {"center": v(520, 980) * mm, "radius": 3.4 * mm});
            skCircle(sketch, "E2.26.0.0", {"center": v(540, 20) * mm, "radius": 3.4 * mm});
            skCircle(sketch, "E2.26.1.0", {"center": v(540, 40) * mm, "radius": 3.4 * mm});
            skCircle(sketch, "E2.26.2.0", {"center": v(540, 60) * mm, "radius": 3.4 * mm});
            skCircle(sketch, "E2.26.3.0", {"center": v(540, 80) * mm, "radius": 3.4 * mm});
            skCircle(sketch, "E2.26.4.0", {"center": v(540, 100) * mm, "radius": 3.4 * mm});
            skCircle(sketch, "E2.26.5.0", {"center": v(540, 120) * mm, "radius": 3.4 * mm});
            skCircle(sketch, "E2.26.6.0", {"center": v(540, 140) * mm, "radius": 3.4 * mm});
            skCircle(sketch, "E2.26.7.0", {"center": v(540, 160) * mm, "radius": 3.4 * mm});
            skCircle(sketch, "E2.26.8.0", {"center": v(540, 180) * mm, "radius": 3.4 * mm});
            skCircle(sketch, "E2.26.9.0", {"center": v(540, 200) * mm, "radius": 3.4 * mm});
            skCircle(sketch, "E2.26.10.0", {"center": v(540, 220) * mm, "radius": 3.4 * mm});
            skCircle(sketch, "E2.26.11.0", {"center": v(540, 240) * mm, "radius": 3.4 * mm});
            skCircle(sketch, "E2.26.12.0", {"center": v(540, 260) * mm, "radius": 3.4 * mm});
            skCircle(sketch, "E2.26.13.0", {"center": v(540, 280) * mm, "radius": 3.4 * mm});
            skCircle(sketch, "E2.26.14.0", {"center": v(540, 300) * mm, "radius": 3.4 * mm});
            skCircle(sketch, "E2.26.15.0", {"center": v(540, 320) * mm, "radius": 3.4 * mm});
            skCircle(sketch, "E2.26.16.0", {"center": v(540, 340) * mm, "radius": 3.4 * mm});
            skCircle(sketch, "E2.26.17.0", {"center": v(540, 360) * mm, "radius": 3.4 * mm});
            skCircle(sketch, "E2.26.18.0", {"center": v(540, 380) * mm, "radius": 3.4 * mm});
            skCircle(sketch, "E2.26.19.0", {"center": v(540, 400) * mm, "radius": 3.4 * mm});
            skCircle(sketch, "E2.26.20.0", {"center": v(540, 420) * mm, "radius": 3.4 * mm});
            skCircle(sketch, "E2.26.21.0", {"center": v(540, 440) * mm, "radius": 3.4 * mm});
            skCircle(sketch, "E2.26.22.0", {"center": v(540, 460) * mm, "radius": 3.4 * mm});
            skCircle(sketch, "E2.26.23.0", {"center": v(540, 480) * mm, "radius": 3.4 * mm});
            skCircle(sketch, "E2.26.24.0", {"center": v(540, 500) * mm, "radius": 3.4 * mm});
            skCircle(sketch, "E2.26.25.0", {"center": v(540, 520) * mm, "radius": 3.4 * mm});
            skCircle(sketch, "E2.26.26.0", {"center": v(540, 540) * mm, "radius": 3.4 * mm});
            skCircle(sketch, "E2.26.27.0", {"center": v(540, 560) * mm, "radius": 3.4 * mm});
            skCircle(sketch, "E2.26.28.0", {"center": v(540, 580) * mm, "radius": 3.4 * mm});
            skCircle(sketch, "E2.26.29.0", {"center": v(540, 600) * mm, "radius": 3.4 * mm});
            skCircle(sketch, "E2.26.30.0", {"center": v(540, 620) * mm, "radius": 3.4 * mm});
            skCircle(sketch, "E2.26.31.0", {"center": v(540, 640) * mm, "radius": 3.4 * mm});
            skCircle(sketch, "E2.26.32.0", {"center": v(540, 660) * mm, "radius": 3.4 * mm});
            skCircle(sketch, "E2.26.33.0", {"center": v(540, 680) * mm, "radius": 3.4 * mm});
            skCircle(sketch, "E2.26.34.0", {"center": v(540, 700) * mm, "radius": 3.4 * mm});
            skCircle(sketch, "E2.26.35.0", {"center": v(540, 720) * mm, "radius": 3.4 * mm});
            skCircle(sketch, "E2.26.36.0", {"center": v(540, 740) * mm, "radius": 3.4 * mm});
            skCircle(sketch, "E2.26.37.0", {"center": v(540, 760) * mm, "radius": 3.4 * mm});
            skCircle(sketch, "E2.26.38.0", {"center": v(540, 780) * mm, "radius": 3.4 * mm});
            skCircle(sketch, "E2.26.39.0", {"center": v(540, 800) * mm, "radius": 3.4 * mm});
            skCircle(sketch, "E2.26.40.0", {"center": v(540, 820) * mm, "radius": 3.4 * mm});
            skCircle(sketch, "E2.26.41.0", {"center": v(540, 840) * mm, "radius": 3.4 * mm});
            skCircle(sketch, "E2.26.42.0", {"center": v(540, 860) * mm, "radius": 3.4 * mm});
            skCircle(sketch, "E2.26.43.0", {"center": v(540, 880) * mm, "radius": 3.4 * mm});
            skCircle(sketch, "E2.26.44.0", {"center": v(540, 900) * mm, "radius": 3.4 * mm});
            skCircle(sketch, "E2.26.45.0", {"center": v(540, 920) * mm, "radius": 3.4 * mm});
            skCircle(sketch, "E2.26.46.0", {"center": v(540, 940) * mm, "radius": 3.4 * mm});
            skCircle(sketch, "E2.26.47.0", {"center": v(540, 960) * mm, "radius": 3.4 * mm});
            skCircle(sketch, "E2.26.48.0", {"center": v(540, 980) * mm, "radius": 3.4 * mm});
            skCircle(sketch, "E2.27.0.0", {"center": v(560, 20) * mm, "radius": 3.4 * mm});
            skCircle(sketch, "E2.27.1.0", {"center": v(560, 40) * mm, "radius": 3.4 * mm});
            skCircle(sketch, "E2.27.2.0", {"center": v(560, 60) * mm, "radius": 3.4 * mm});
            skCircle(sketch, "E2.27.3.0", {"center": v(560, 80) * mm, "radius": 3.4 * mm});
            skCircle(sketch, "E2.27.4.0", {"center": v(560, 100) * mm, "radius": 3.4 * mm});
            skCircle(sketch, "E2.27.5.0", {"center": v(560, 120) * mm, "radius": 3.4 * mm});
            skCircle(sketch, "E2.27.6.0", {"center": v(560, 140) * mm, "radius": 3.4 * mm});
            skCircle(sketch, "E2.27.7.0", {"center": v(560, 160) * mm, "radius": 3.4 * mm});
            skCircle(sketch, "E2.27.8.0", {"center": v(560, 180) * mm, "radius": 3.4 * mm});
            skCircle(sketch, "E2.27.9.0", {"center": v(560, 200) * mm, "radius": 3.4 * mm});
            skCircle(sketch, "E2.27.10.0", {"center": v(560, 220) * mm, "radius": 3.4 * mm});
            skCircle(sketch, "E2.27.11.0", {"center": v(560, 240) * mm, "radius": 3.4 * mm});
            skCircle(sketch, "E2.27.12.0", {"center": v(560, 260) * mm, "radius": 3.4 * mm});
            skCircle(sketch, "E2.27.13.0", {"center": v(560, 280) * mm, "radius": 3.4 * mm});
            skCircle(sketch, "E2.27.14.0", {"center": v(560, 300) * mm, "radius": 3.4 * mm});
            skCircle(sketch, "E2.27.15.0", {"center": v(560, 320) * mm, "radius": 3.4 * mm});
            skCircle(sketch, "E2.27.16.0", {"center": v(560, 340) * mm, "radius": 3.4 * mm});
            skCircle(sketch, "E2.27.17.0", {"center": v(560, 360) * mm, "radius": 3.4 * mm});
            skCircle(sketch, "E2.27.18.0", {"center": v(560, 380) * mm, "radius": 3.4 * mm});
            skCircle(sketch, "E2.27.19.0", {"center": v(560, 400) * mm, "radius": 3.4 * mm});
            skCircle(sketch, "E2.27.20.0", {"center": v(560, 420) * mm, "radius": 3.4 * mm});
            skCircle(sketch, "E2.27.21.0", {"center": v(560, 440) * mm, "radius": 3.4 * mm});
            skCircle(sketch, "E2.27.22.0", {"center": v(560, 460) * mm, "radius": 3.4 * mm});
            skCircle(sketch, "E2.27.23.0", {"center": v(560, 480) * mm, "radius": 3.4 * mm});
            skCircle(sketch, "E2.27.24.0", {"center": v(560, 500) * mm, "radius": 3.4 * mm});
            skCircle(sketch, "E2.27.25.0", {"center": v(560, 520) * mm, "radius": 3.4 * mm});
            skCircle(sketch, "E2.27.26.0", {"center": v(560, 540) * mm, "radius": 3.4 * mm});
            skCircle(sketch, "E2.27.27.0", {"center": v(560, 560) * mm, "radius": 3.4 * mm});
            skCircle(sketch, "E2.27.28.0", {"center": v(560, 580) * mm, "radius": 3.4 * mm});
            skCircle(sketch, "E2.27.29.0", {"center": v(560, 600) * mm, "radius": 3.4 * mm});
            skCircle(sketch, "E2.27.30.0", {"center": v(560, 620) * mm, "radius": 3.4 * mm});
            skCircle(sketch, "E2.27.31.0", {"center": v(560, 640) * mm, "radius": 3.4 * mm});
            skCircle(sketch, "E2.27.32.0", {"center": v(560, 660) * mm, "radius": 3.4 * mm});
            skCircle(sketch, "E2.27.33.0", {"center": v(560, 680) * mm, "radius": 3.4 * mm});
            skCircle(sketch, "E2.27.34.0", {"center": v(560, 700) * mm, "radius": 3.4 * mm});
            skCircle(sketch, "E2.27.35.0", {"center": v(560, 720) * mm, "radius": 3.4 * mm});
            skCircle(sketch, "E2.27.36.0", {"center": v(560, 740) * mm, "radius": 3.4 * mm});
            skCircle(sketch, "E2.27.37.0", {"center": v(560, 760) * mm, "radius": 3.4 * mm});
            skCircle(sketch, "E2.27.38.0", {"center": v(560, 780) * mm, "radius": 3.4 * mm});
            skCircle(sketch, "E2.27.39.0", {"center": v(560, 800) * mm, "radius": 3.4 * mm});
            skCircle(sketch, "E2.27.40.0", {"center": v(560, 820) * mm, "radius": 3.4 * mm});
            skCircle(sketch, "E2.27.41.0", {"center": v(560, 840) * mm, "radius": 3.4 * mm});
            skCircle(sketch, "E2.27.42.0", {"center": v(560, 860) * mm, "radius": 3.4 * mm});
            skCircle(sketch, "E2.27.43.0", {"center": v(560, 880) * mm, "radius": 3.4 * mm});
            skCircle(sketch, "E2.27.44.0", {"center": v(560, 900) * mm, "radius": 3.4 * mm});
            skCircle(sketch, "E2.27.45.0", {"center": v(560, 920) * mm, "radius": 3.4 * mm});
            skCircle(sketch, "E2.27.46.0", {"center": v(560, 940) * mm, "radius": 3.4 * mm});
            skCircle(sketch, "E2.27.47.0", {"center": v(560, 960) * mm, "radius": 3.4 * mm});
            skCircle(sketch, "E2.27.48.0", {"center": v(560, 980) * mm, "radius": 3.4 * mm});
            skCircle(sketch, "E2.28.0.0", {"center": v(580, 20) * mm, "radius": 3.4 * mm});
            skCircle(sketch, "E2.28.1.0", {"center": v(580, 40) * mm, "radius": 3.4 * mm});
            skCircle(sketch, "E2.28.2.0", {"center": v(580, 60) * mm, "radius": 3.4 * mm});
            skCircle(sketch, "E2.28.3.0", {"center": v(580, 80) * mm, "radius": 3.4 * mm});
            skCircle(sketch, "E2.28.4.0", {"center": v(580, 100) * mm, "radius": 3.4 * mm});
            skCircle(sketch, "E2.28.5.0", {"center": v(580, 120) * mm, "radius": 3.4 * mm});
            skCircle(sketch, "E2.28.6.0", {"center": v(580, 140) * mm, "radius": 3.4 * mm});
            skCircle(sketch, "E2.28.7.0", {"center": v(580, 160) * mm, "radius": 3.4 * mm});
            skCircle(sketch, "E2.28.8.0", {"center": v(580, 180) * mm, "radius": 3.4 * mm});
            skCircle(sketch, "E2.28.9.0", {"center": v(580, 200) * mm, "radius": 3.4 * mm});
            skCircle(sketch, "E2.28.10.0", {"center": v(580, 220) * mm, "radius": 3.4 * mm});
            skCircle(sketch, "E2.28.11.0", {"center": v(580, 240) * mm, "radius": 3.4 * mm});
            skCircle(sketch, "E2.28.12.0", {"center": v(580, 260) * mm, "radius": 3.4 * mm});
            skCircle(sketch, "E2.28.13.0", {"center": v(580, 280) * mm, "radius": 3.4 * mm});
            skCircle(sketch, "E2.28.14.0", {"center": v(580, 300) * mm, "radius": 3.4 * mm});
            skCircle(sketch, "E2.28.15.0", {"center": v(580, 320) * mm, "radius": 3.4 * mm});
            skCircle(sketch, "E2.28.16.0", {"center": v(580, 340) * mm, "radius": 3.4 * mm});
            skCircle(sketch, "E2.28.17.0", {"center": v(580, 360) * mm, "radius": 3.4 * mm});
            skCircle(sketch, "E2.28.18.0", {"center": v(580, 380) * mm, "radius": 3.4 * mm});
            skCircle(sketch, "E2.28.19.0", {"center": v(580, 400) * mm, "radius": 3.4 * mm});
            skCircle(sketch, "E2.28.20.0", {"center": v(580, 420) * mm, "radius": 3.4 * mm});
            skCircle(sketch, "E2.28.21.0", {"center": v(580, 440) * mm, "radius": 3.4 * mm});
            skCircle(sketch, "E2.28.22.0", {"center": v(580, 460) * mm, "radius": 3.4 * mm});
            skCircle(sketch, "E2.28.23.0", {"center": v(580, 480) * mm, "radius": 3.4 * mm});
            skCircle(sketch, "E2.28.24.0", {"center": v(580, 500) * mm, "radius": 3.4 * mm});
            skCircle(sketch, "E2.28.25.0", {"center": v(580, 520) * mm, "radius": 3.4 * mm});
            skCircle(sketch, "E2.28.26.0", {"center": v(580, 540) * mm, "radius": 3.4 * mm});
            skCircle(sketch, "E2.28.27.0", {"center": v(580, 560) * mm, "radius": 3.4 * mm});
            skCircle(sketch, "E2.28.28.0", {"center": v(580, 580) * mm, "radius": 3.4 * mm});
            skCircle(sketch, "E2.28.29.0", {"center": v(580, 600) * mm, "radius": 3.4 * mm});
            skCircle(sketch, "E2.28.30.0", {"center": v(580, 620) * mm, "radius": 3.4 * mm});
            skCircle(sketch, "E2.28.31.0", {"center": v(580, 640) * mm, "radius": 3.4 * mm});
            skCircle(sketch, "E2.28.32.0", {"center": v(580, 660) * mm, "radius": 3.4 * mm});
            skCircle(sketch, "E2.28.33.0", {"center": v(580, 680) * mm, "radius": 3.4 * mm});
            skCircle(sketch, "E2.28.34.0", {"center": v(580, 700) * mm, "radius": 3.4 * mm});
            skCircle(sketch, "E2.28.35.0", {"center": v(580, 720) * mm, "radius": 3.4 * mm});
            skCircle(sketch, "E2.28.36.0", {"center": v(580, 740) * mm, "radius": 3.4 * mm});
            skCircle(sketch, "E2.28.37.0", {"center": v(580, 760) * mm, "radius": 3.4 * mm});
            skCircle(sketch, "E2.28.38.0", {"center": v(580, 780) * mm, "radius": 3.4 * mm});
            skCircle(sketch, "E2.28.39.0", {"center": v(580, 800) * mm, "radius": 3.4 * mm});
            skCircle(sketch, "E2.28.40.0", {"center": v(580, 820) * mm, "radius": 3.4 * mm});
            skCircle(sketch, "E2.28.41.0", {"center": v(580, 840) * mm, "radius": 3.4 * mm});
            skCircle(sketch, "E2.28.42.0", {"center": v(580, 860) * mm, "radius": 3.4 * mm});
            skCircle(sketch, "E2.28.43.0", {"center": v(580, 880) * mm, "radius": 3.4 * mm});
            skCircle(sketch, "E2.28.44.0", {"center": v(580, 900) * mm, "radius": 3.4 * mm});
            skCircle(sketch, "E2.28.45.0", {"center": v(580, 920) * mm, "radius": 3.4 * mm});
            skCircle(sketch, "E2.28.46.0", {"center": v(580, 940) * mm, "radius": 3.4 * mm});
            skCircle(sketch, "E2.28.47.0", {"center": v(580, 960) * mm, "radius": 3.4 * mm});
            skCircle(sketch, "E2.28.48.0", {"center": v(580, 980) * mm, "radius": 3.4 * mm});
            skLineSegment(sketch, "E2.direction1", {"start": v(20, 20) * mm, "end": v(40, 20) * mm, "construction": true});
            skLineSegment(sketch, "E2.direction2", {"start": v(20, 20) * mm, "end": v(20, 40) * mm, "construction": true});
            skCircle(sketch, "E3.0.29.0", {"center": v(600, 20) * mm, "radius": 3.4 * mm});
            skCircle(sketch, "E3.0.29.1", {"center": v(600, 40) * mm, "radius": 3.4 * mm});
            skCircle(sketch, "E3.0.29.2", {"center": v(600, 60) * mm, "radius": 3.4 * mm});
            skCircle(sketch, "E3.0.29.3", {"center": v(600, 80) * mm, "radius": 3.4 * mm});
            skCircle(sketch, "E3.0.29.4", {"center": v(600, 100) * mm, "radius": 3.4 * mm});
            skCircle(sketch, "E3.0.29.5", {"center": v(600, 120) * mm, "radius": 3.4 * mm});
            skCircle(sketch, "E3.0.29.6", {"center": v(600, 140) * mm, "radius": 3.4 * mm});
            skCircle(sketch, "E3.0.29.7", {"center": v(600, 160) * mm, "radius": 3.4 * mm});
            skCircle(sketch, "E3.0.29.8", {"center": v(600, 180) * mm, "radius": 3.4 * mm});
            skCircle(sketch, "E3.0.29.9", {"center": v(600, 200) * mm, "radius": 3.4 * mm});
            skCircle(sketch, "E3.0.29.10", {"center": v(600, 220) * mm, "radius": 3.4 * mm});
            skCircle(sketch, "E3.0.29.11", {"center": v(600, 240) * mm, "radius": 3.4 * mm});
            skCircle(sketch, "E3.0.29.12", {"center": v(600, 260) * mm, "radius": 3.4 * mm});
            skCircle(sketch, "E3.0.29.13", {"center": v(600, 280) * mm, "radius": 3.4 * mm});
            skCircle(sketch, "E3.0.29.14", {"center": v(600, 300) * mm, "radius": 3.4 * mm});
            skCircle(sketch, "E3.0.29.15", {"center": v(600, 320) * mm, "radius": 3.4 * mm});
            skCircle(sketch, "E3.0.29.16", {"center": v(600, 340) * mm, "radius": 3.4 * mm});
            skCircle(sketch, "E3.0.29.17", {"center": v(600, 360) * mm, "radius": 3.4 * mm});
            skCircle(sketch, "E3.0.29.18", {"center": v(600, 380) * mm, "radius": 3.4 * mm});
            skCircle(sketch, "E3.0.29.19", {"center": v(600, 400) * mm, "radius": 3.4 * mm});
            skCircle(sketch, "E3.0.29.20", {"center": v(600, 420) * mm, "radius": 3.4 * mm});
            skCircle(sketch, "E3.0.29.21", {"center": v(600, 440) * mm, "radius": 3.4 * mm});
            skCircle(sketch, "E3.0.29.22", {"center": v(600, 460) * mm, "radius": 3.4 * mm});
            skCircle(sketch, "E3.0.29.23", {"center": v(600, 480) * mm, "radius": 3.4 * mm});
            skCircle(sketch, "E3.0.29.24", {"center": v(600, 500) * mm, "radius": 3.4 * mm});
            skCircle(sketch, "E3.0.29.25", {"center": v(600, 520) * mm, "radius": 3.4 * mm});
            skCircle(sketch, "E3.0.29.26", {"center": v(600, 540) * mm, "radius": 3.4 * mm});
            skCircle(sketch, "E3.0.29.27", {"center": v(600, 560) * mm, "radius": 3.4 * mm});
            skCircle(sketch, "E3.0.29.28", {"center": v(600, 580) * mm, "radius": 3.4 * mm});
            skCircle(sketch, "E3.0.29.29", {"center": v(600, 600) * mm, "radius": 3.4 * mm});
            skCircle(sketch, "E3.0.29.30", {"center": v(600, 620) * mm, "radius": 3.4 * mm});
            skCircle(sketch, "E3.0.29.31", {"center": v(600, 640) * mm, "radius": 3.4 * mm});
            skCircle(sketch, "E3.0.29.32", {"center": v(600, 660) * mm, "radius": 3.4 * mm});
            skCircle(sketch, "E3.0.29.33", {"center": v(600, 680) * mm, "radius": 3.4 * mm});
            skCircle(sketch, "E3.0.29.34", {"center": v(600, 700) * mm, "radius": 3.4 * mm});
            skCircle(sketch, "E3.0.29.35", {"center": v(600, 720) * mm, "radius": 3.4 * mm});
            skCircle(sketch, "E3.0.29.36", {"center": v(600, 740) * mm, "radius": 3.4 * mm});
            skCircle(sketch, "E3.0.29.37", {"center": v(600, 760) * mm, "radius": 3.4 * mm});
            skCircle(sketch, "E3.0.29.38", {"center": v(600, 780) * mm, "radius": 3.4 * mm});
            skCircle(sketch, "E3.0.29.39", {"center": v(600, 800) * mm, "radius": 3.4 * mm});
            skCircle(sketch, "E3.0.29.40", {"center": v(600, 820) * mm, "radius": 3.4 * mm});
            skCircle(sketch, "E3.0.29.41", {"center": v(600, 840) * mm, "radius": 3.4 * mm});
            skCircle(sketch, "E3.0.29.42", {"center": v(600, 860) * mm, "radius": 3.4 * mm});
            skCircle(sketch, "E3.0.29.43", {"center": v(600, 880) * mm, "radius": 3.4 * mm});
            skCircle(sketch, "E3.0.29.44", {"center": v(600, 900) * mm, "radius": 3.4 * mm});
            skCircle(sketch, "E3.0.29.45", {"center": v(600, 920) * mm, "radius": 3.4 * mm});
            skCircle(sketch, "E3.0.29.46", {"center": v(600, 940) * mm, "radius": 3.4 * mm});
            skCircle(sketch, "E3.0.29.47", {"center": v(600, 960) * mm, "radius": 3.4 * mm});
            skCircle(sketch, "E3.0.29.48", {"center": v(600, 980) * mm, "radius": 3.4 * mm});
            skCircle(sketch, "E3.0.30.0", {"center": v(620, 20) * mm, "radius": 3.4 * mm});
            skCircle(sketch, "E3.0.30.1", {"center": v(620, 40) * mm, "radius": 3.4 * mm});
            skCircle(sketch, "E3.0.30.2", {"center": v(620, 60) * mm, "radius": 3.4 * mm});
            skCircle(sketch, "E3.0.30.3", {"center": v(620, 80) * mm, "radius": 3.4 * mm});
            skCircle(sketch, "E3.0.30.4", {"center": v(620, 100) * mm, "radius": 3.4 * mm});
            skCircle(sketch, "E3.0.30.5", {"center": v(620, 120) * mm, "radius": 3.4 * mm});
            skCircle(sketch, "E3.0.30.6", {"center": v(620, 140) * mm, "radius": 3.4 * mm});
            skCircle(sketch, "E3.0.30.7", {"center": v(620, 160) * mm, "radius": 3.4 * mm});
            skCircle(sketch, "E3.0.30.8", {"center": v(620, 180) * mm, "radius": 3.4 * mm});
            skCircle(sketch, "E3.0.30.9", {"center": v(620, 200) * mm, "radius": 3.4 * mm});
            skCircle(sketch, "E3.0.30.10", {"center": v(620, 220) * mm, "radius": 3.4 * mm});
            skCircle(sketch, "E3.0.30.11", {"center": v(620, 240) * mm, "radius": 3.4 * mm});
            skCircle(sketch, "E3.0.30.12", {"center": v(620, 260) * mm, "radius": 3.4 * mm});
            skCircle(sketch, "E3.0.30.13", {"center": v(620, 280) * mm, "radius": 3.4 * mm});
            skCircle(sketch, "E3.0.30.14", {"center": v(620, 300) * mm, "radius": 3.4 * mm});
            skCircle(sketch, "E3.0.30.15", {"center": v(620, 320) * mm, "radius": 3.4 * mm});
            skCircle(sketch, "E3.0.30.16", {"center": v(620, 340) * mm, "radius": 3.4 * mm});
            skCircle(sketch, "E3.0.30.17", {"center": v(620, 360) * mm, "radius": 3.4 * mm});
            skCircle(sketch, "E3.0.30.18", {"center": v(620, 380) * mm, "radius": 3.4 * mm});
            skCircle(sketch, "E3.0.30.19", {"center": v(620, 400) * mm, "radius": 3.4 * mm});
            skCircle(sketch, "E3.0.30.20", {"center": v(620, 420) * mm, "radius": 3.4 * mm});
            skCircle(sketch, "E3.0.30.21", {"center": v(620, 440) * mm, "radius": 3.4 * mm});
            skCircle(sketch, "E3.0.30.22", {"center": v(620, 460) * mm, "radius": 3.4 * mm});
            skCircle(sketch, "E3.0.30.23", {"center": v(620, 480) * mm, "radius": 3.4 * mm});
            skCircle(sketch, "E3.0.30.24", {"center": v(620, 500) * mm, "radius": 3.4 * mm});
            skCircle(sketch, "E3.0.30.25", {"center": v(620, 520) * mm, "radius": 3.4 * mm});
            skCircle(sketch, "E3.0.30.26", {"center": v(620, 540) * mm, "radius": 3.4 * mm});
            skCircle(sketch, "E3.0.30.27", {"center": v(620, 560) * mm, "radius": 3.4 * mm});
            skCircle(sketch, "E3.0.30.28", {"center": v(620, 580) * mm, "radius": 3.4 * mm});
            skCircle(sketch, "E3.0.30.29", {"center": v(620, 600) * mm, "radius": 3.4 * mm});
            skCircle(sketch, "E3.0.30.30", {"center": v(620, 620) * mm, "radius": 3.4 * mm});
            skCircle(sketch, "E3.0.30.31", {"center": v(620, 640) * mm, "radius": 3.4 * mm});
            skCircle(sketch, "E3.0.30.32", {"center": v(620, 660) * mm, "radius": 3.4 * mm});
            skCircle(sketch, "E3.0.30.33", {"center": v(620, 680) * mm, "radius": 3.4 * mm});
            skCircle(sketch, "E3.0.30.34", {"center": v(620, 700) * mm, "radius": 3.4 * mm});
            skCircle(sketch, "E3.0.30.35", {"center": v(620, 720) * mm, "radius": 3.4 * mm});
            skCircle(sketch, "E3.0.30.36", {"center": v(620, 740) * mm, "radius": 3.4 * mm});
            skCircle(sketch, "E3.0.30.37", {"center": v(620, 760) * mm, "radius": 3.4 * mm});
            skCircle(sketch, "E3.0.30.38", {"center": v(620, 780) * mm, "radius": 3.4 * mm});
            skCircle(sketch, "E3.0.30.39", {"center": v(620, 800) * mm, "radius": 3.4 * mm});
            skCircle(sketch, "E3.0.30.40", {"center": v(620, 820) * mm, "radius": 3.4 * mm});
            skCircle(sketch, "E3.0.30.41", {"center": v(620, 840) * mm, "radius": 3.4 * mm});
            skCircle(sketch, "E3.0.30.42", {"center": v(620, 860) * mm, "radius": 3.4 * mm});
            skCircle(sketch, "E3.0.30.43", {"center": v(620, 880) * mm, "radius": 3.4 * mm});
            skCircle(sketch, "E3.0.30.44", {"center": v(620, 900) * mm, "radius": 3.4 * mm});
            skCircle(sketch, "E3.0.30.45", {"center": v(620, 920) * mm, "radius": 3.4 * mm});
            skCircle(sketch, "E3.0.30.46", {"center": v(620, 940) * mm, "radius": 3.4 * mm});
            skCircle(sketch, "E3.0.30.47", {"center": v(620, 960) * mm, "radius": 3.4 * mm});
            skCircle(sketch, "E3.0.30.48", {"center": v(620, 980) * mm, "radius": 3.4 * mm});
            skCircle(sketch, "E3.0.31.0", {"center": v(640, 20) * mm, "radius": 3.4 * mm});
            skCircle(sketch, "E3.0.31.1", {"center": v(640, 40) * mm, "radius": 3.4 * mm});
            skCircle(sketch, "E3.0.31.2", {"center": v(640, 60) * mm, "radius": 3.4 * mm});
            skCircle(sketch, "E3.0.31.3", {"center": v(640, 80) * mm, "radius": 3.4 * mm});
            skCircle(sketch, "E3.0.31.4", {"center": v(640, 100) * mm, "radius": 3.4 * mm});
            skCircle(sketch, "E3.0.31.5", {"center": v(640, 120) * mm, "radius": 3.4 * mm});
            skCircle(sketch, "E3.0.31.6", {"center": v(640, 140) * mm, "radius": 3.4 * mm});
            skCircle(sketch, "E3.0.31.7", {"center": v(640, 160) * mm, "radius": 3.4 * mm});
            skCircle(sketch, "E3.0.31.8", {"center": v(640, 180) * mm, "radius": 3.4 * mm});
            skCircle(sketch, "E3.0.31.9", {"center": v(640, 200) * mm, "radius": 3.4 * mm});
            skCircle(sketch, "E3.0.31.10", {"center": v(640, 220) * mm, "radius": 3.4 * mm});
            skCircle(sketch, "E3.0.31.11", {"center": v(640, 240) * mm, "radius": 3.4 * mm});
            skCircle(sketch, "E3.0.31.12", {"center": v(640, 260) * mm, "radius": 3.4 * mm});
            skCircle(sketch, "E3.0.31.13", {"center": v(640, 280) * mm, "radius": 3.4 * mm});
            skCircle(sketch, "E3.0.31.14", {"center": v(640, 300) * mm, "radius": 3.4 * mm});
            skCircle(sketch, "E3.0.31.15", {"center": v(640, 320) * mm, "radius": 3.4 * mm});
            skCircle(sketch, "E3.0.31.16", {"center": v(640, 340) * mm, "radius": 3.4 * mm});
            skCircle(sketch, "E3.0.31.17", {"center": v(640, 360) * mm, "radius": 3.4 * mm});
            skCircle(sketch, "E3.0.31.18", {"center": v(640, 380) * mm, "radius": 3.4 * mm});
            skCircle(sketch, "E3.0.31.19", {"center": v(640, 400) * mm, "radius": 3.4 * mm});
            skCircle(sketch, "E3.0.31.20", {"center": v(640, 420) * mm, "radius": 3.4 * mm});
            skCircle(sketch, "E3.0.31.21", {"center": v(640, 440) * mm, "radius": 3.4 * mm});
            skCircle(sketch, "E3.0.31.22", {"center": v(640, 460) * mm, "radius": 3.4 * mm});
            skCircle(sketch, "E3.0.31.23", {"center": v(640, 480) * mm, "radius": 3.4 * mm});
            skCircle(sketch, "E3.0.31.24", {"center": v(640, 500) * mm, "radius": 3.4 * mm});
            skCircle(sketch, "E3.0.31.25", {"center": v(640, 520) * mm, "radius": 3.4 * mm});
            skCircle(sketch, "E3.0.31.26", {"center": v(640, 540) * mm, "radius": 3.4 * mm});
            skCircle(sketch, "E3.0.31.27", {"center": v(640, 560) * mm, "radius": 3.4 * mm});
            skCircle(sketch, "E3.0.31.28", {"center": v(640, 580) * mm, "radius": 3.4 * mm});
            skCircle(sketch, "E3.0.31.29", {"center": v(640, 600) * mm, "radius": 3.4 * mm});
            skCircle(sketch, "E3.0.31.30", {"center": v(640, 620) * mm, "radius": 3.4 * mm});
            skCircle(sketch, "E3.0.31.31", {"center": v(640, 640) * mm, "radius": 3.4 * mm});
            skCircle(sketch, "E3.0.31.32", {"center": v(640, 660) * mm, "radius": 3.4 * mm});
            skCircle(sketch, "E3.0.31.33", {"center": v(640, 680) * mm, "radius": 3.4 * mm});
            skCircle(sketch, "E3.0.31.34", {"center": v(640, 700) * mm, "radius": 3.4 * mm});
            skCircle(sketch, "E3.0.31.35", {"center": v(640, 720) * mm, "radius": 3.4 * mm});
            skCircle(sketch, "E3.0.31.36", {"center": v(640, 740) * mm, "radius": 3.4 * mm});
            skCircle(sketch, "E3.0.31.37", {"center": v(640, 760) * mm, "radius": 3.4 * mm});
            skCircle(sketch, "E3.0.31.38", {"center": v(640, 780) * mm, "radius": 3.4 * mm});
            skCircle(sketch, "E3.0.31.39", {"center": v(640, 800) * mm, "radius": 3.4 * mm});
            skCircle(sketch, "E3.0.31.40", {"center": v(640, 820) * mm, "radius": 3.4 * mm});
            skCircle(sketch, "E3.0.31.41", {"center": v(640, 840) * mm, "radius": 3.4 * mm});
            skCircle(sketch, "E3.0.31.42", {"center": v(640, 860) * mm, "radius": 3.4 * mm});
            skCircle(sketch, "E3.0.31.43", {"center": v(640, 880) * mm, "radius": 3.4 * mm});
            skCircle(sketch, "E3.0.31.44", {"center": v(640, 900) * mm, "radius": 3.4 * mm});
            skCircle(sketch, "E3.0.31.45", {"center": v(640, 920) * mm, "radius": 3.4 * mm});
            skCircle(sketch, "E3.0.31.46", {"center": v(640, 940) * mm, "radius": 3.4 * mm});
            skCircle(sketch, "E3.0.31.47", {"center": v(640, 960) * mm, "radius": 3.4 * mm});
            skCircle(sketch, "E3.0.31.48", {"center": v(640, 980) * mm, "radius": 3.4 * mm});
            skCircle(sketch, "E3.0.32.0", {"center": v(660, 20) * mm, "radius": 3.4 * mm});
            skCircle(sketch, "E3.0.32.1", {"center": v(660, 40) * mm, "radius": 3.4 * mm});
            skCircle(sketch, "E3.0.32.2", {"center": v(660, 60) * mm, "radius": 3.4 * mm});
            skCircle(sketch, "E3.0.32.3", {"center": v(660, 80) * mm, "radius": 3.4 * mm});
            skCircle(sketch, "E3.0.32.4", {"center": v(660, 100) * mm, "radius": 3.4 * mm});
            skCircle(sketch, "E3.0.32.5", {"center": v(660, 120) * mm, "radius": 3.4 * mm});
            skCircle(sketch, "E3.0.32.6", {"center": v(660, 140) * mm, "radius": 3.4 * mm});
            skCircle(sketch, "E3.0.32.7", {"center": v(660, 160) * mm, "radius": 3.4 * mm});
            skCircle(sketch, "E3.0.32.8", {"center": v(660, 180) * mm, "radius": 3.4 * mm});
            skCircle(sketch, "E3.0.32.9", {"center": v(660, 200) * mm, "radius": 3.4 * mm});
            skCircle(sketch, "E3.0.32.10", {"center": v(660, 220) * mm, "radius": 3.4 * mm});
            skCircle(sketch, "E3.0.32.11", {"center": v(660, 240) * mm, "radius": 3.4 * mm});
            skCircle(sketch, "E3.0.32.12", {"center": v(660, 260) * mm, "radius": 3.4 * mm});
            skCircle(sketch, "E3.0.32.13", {"center": v(660, 280) * mm, "radius": 3.4 * mm});
            skCircle(sketch, "E3.0.32.14", {"center": v(660, 300) * mm, "radius": 3.4 * mm});
            skCircle(sketch, "E3.0.32.15", {"center": v(660, 320) * mm, "radius": 3.4 * mm});
            skCircle(sketch, "E3.0.32.16", {"center": v(660, 340) * mm, "radius": 3.4 * mm});
            skCircle(sketch, "E3.0.32.17", {"center": v(660, 360) * mm, "radius": 3.4 * mm});
            skCircle(sketch, "E3.0.32.18", {"center": v(660, 380) * mm, "radius": 3.4 * mm});
            skCircle(sketch, "E3.0.32.19", {"center": v(660, 400) * mm, "radius": 3.4 * mm});
            skCircle(sketch, "E3.0.32.20", {"center": v(660, 420) * mm, "radius": 3.4 * mm});
            skCircle(sketch, "E3.0.32.21", {"center": v(660, 440) * mm, "radius": 3.4 * mm});
            skCircle(sketch, "E3.0.32.22", {"center": v(660, 460) * mm, "radius": 3.4 * mm});
            skCircle(sketch, "E3.0.32.23", {"center": v(660, 480) * mm, "radius": 3.4 * mm});
            skCircle(sketch, "E3.0.32.24", {"center": v(660, 500) * mm, "radius": 3.4 * mm});
            skCircle(sketch, "E3.0.32.25", {"center": v(660, 520) * mm, "radius": 3.4 * mm});
            skCircle(sketch, "E3.0.32.26", {"center": v(660, 540) * mm, "radius": 3.4 * mm});
            skCircle(sketch, "E3.0.32.27", {"center": v(660, 560) * mm, "radius": 3.4 * mm});
            skCircle(sketch, "E3.0.32.28", {"center": v(660, 580) * mm, "radius": 3.4 * mm});
            skCircle(sketch, "E3.0.32.29", {"center": v(660, 600) * mm, "radius": 3.4 * mm});
            skCircle(sketch, "E3.0.32.30", {"center": v(660, 620) * mm, "radius": 3.4 * mm});
            skCircle(sketch, "E3.0.32.31", {"center": v(660, 640) * mm, "radius": 3.4 * mm});
            skCircle(sketch, "E3.0.32.32", {"center": v(660, 660) * mm, "radius": 3.4 * mm});
            skCircle(sketch, "E3.0.32.33", {"center": v(660, 680) * mm, "radius": 3.4 * mm});
            skCircle(sketch, "E3.0.32.34", {"center": v(660, 700) * mm, "radius": 3.4 * mm});
            skCircle(sketch, "E3.0.32.35", {"center": v(660, 720) * mm, "radius": 3.4 * mm});
            skCircle(sketch, "E3.0.32.36", {"center": v(660, 740) * mm, "radius": 3.4 * mm});
            skCircle(sketch, "E3.0.32.37", {"center": v(660, 760) * mm, "radius": 3.4 * mm});
            skCircle(sketch, "E3.0.32.38", {"center": v(660, 780) * mm, "radius": 3.4 * mm});
            skCircle(sketch, "E3.0.32.39", {"center": v(660, 800) * mm, "radius": 3.4 * mm});
            skCircle(sketch, "E3.0.32.40", {"center": v(660, 820) * mm, "radius": 3.4 * mm});
            skCircle(sketch, "E3.0.32.41", {"center": v(660, 840) * mm, "radius": 3.4 * mm});
            skCircle(sketch, "E3.0.32.42", {"center": v(660, 860) * mm, "radius": 3.4 * mm});
            skCircle(sketch, "E3.0.32.43", {"center": v(660, 880) * mm, "radius": 3.4 * mm});
            skCircle(sketch, "E3.0.32.44", {"center": v(660, 900) * mm, "radius": 3.4 * mm});
            skCircle(sketch, "E3.0.32.45", {"center": v(660, 920) * mm, "radius": 3.4 * mm});
            skCircle(sketch, "E3.0.32.46", {"center": v(660, 940) * mm, "radius": 3.4 * mm});
            skCircle(sketch, "E3.0.32.47", {"center": v(660, 960) * mm, "radius": 3.4 * mm});
            skCircle(sketch, "E3.0.32.48", {"center": v(660, 980) * mm, "radius": 3.4 * mm});
            skCircle(sketch, "E3.0.33.0", {"center": v(680, 20) * mm, "radius": 3.4 * mm});
            skCircle(sketch, "E3.0.33.1", {"center": v(680, 40) * mm, "radius": 3.4 * mm});
            skCircle(sketch, "E3.0.33.2", {"center": v(680, 60) * mm, "radius": 3.4 * mm});
            skCircle(sketch, "E3.0.33.3", {"center": v(680, 80) * mm, "radius": 3.4 * mm});
            skCircle(sketch, "E3.0.33.4", {"center": v(680, 100) * mm, "radius": 3.4 * mm});
            skCircle(sketch, "E3.0.33.5", {"center": v(680, 120) * mm, "radius": 3.4 * mm});
            skCircle(sketch, "E3.0.33.6", {"center": v(680, 140) * mm, "radius": 3.4 * mm});
            skCircle(sketch, "E3.0.33.7", {"center": v(680, 160) * mm, "radius": 3.4 * mm});
            skCircle(sketch, "E3.0.33.8", {"center": v(680, 180) * mm, "radius": 3.4 * mm});
            skCircle(sketch, "E3.0.33.9", {"center": v(680, 200) * mm, "radius": 3.4 * mm});
            skCircle(sketch, "E3.0.33.10", {"center": v(680, 220) * mm, "radius": 3.4 * mm});
            skCircle(sketch, "E3.0.33.11", {"center": v(680, 240) * mm, "radius": 3.4 * mm});
            skCircle(sketch, "E3.0.33.12", {"center": v(680, 260) * mm, "radius": 3.4 * mm});
            skCircle(sketch, "E3.0.33.13", {"center": v(680, 280) * mm, "radius": 3.4 * mm});
            skCircle(sketch, "E3.0.33.14", {"center": v(680, 300) * mm, "radius": 3.4 * mm});
            skCircle(sketch, "E3.0.33.15", {"center": v(680, 320) * mm, "radius": 3.4 * mm});
            skCircle(sketch, "E3.0.33.16", {"center": v(680, 340) * mm, "radius": 3.4 * mm});
            skCircle(sketch, "E3.0.33.17", {"center": v(680, 360) * mm, "radius": 3.4 * mm});
            skCircle(sketch, "E3.0.33.18", {"center": v(680, 380) * mm, "radius": 3.4 * mm});
            skCircle(sketch, "E3.0.33.19", {"center": v(680, 400) * mm, "radius": 3.4 * mm});
            skCircle(sketch, "E3.0.33.20", {"center": v(680, 420) * mm, "radius": 3.4 * mm});
            skCircle(sketch, "E3.0.33.21", {"center": v(680, 440) * mm, "radius": 3.4 * mm});
            skCircle(sketch, "E3.0.33.22", {"center": v(680, 460) * mm, "radius": 3.4 * mm});
            skCircle(sketch, "E3.0.33.23", {"center": v(680, 480) * mm, "radius": 3.4 * mm});
            skCircle(sketch, "E3.0.33.24", {"center": v(680, 500) * mm, "radius": 3.4 * mm});
            skCircle(sketch, "E3.0.33.25", {"center": v(680, 520) * mm, "radius": 3.4 * mm});
            skCircle(sketch, "E3.0.33.26", {"center": v(680, 540) * mm, "radius": 3.4 * mm});
            skCircle(sketch, "E3.0.33.27", {"center": v(680, 560) * mm, "radius": 3.4 * mm});
            skCircle(sketch, "E3.0.33.28", {"center": v(680, 580) * mm, "radius": 3.4 * mm});
            skCircle(sketch, "E3.0.33.29", {"center": v(680, 600) * mm, "radius": 3.4 * mm});
            skCircle(sketch, "E3.0.33.30", {"center": v(680, 620) * mm, "radius": 3.4 * mm});
            skCircle(sketch, "E3.0.33.31", {"center": v(680, 640) * mm, "radius": 3.4 * mm});
            skCircle(sketch, "E3.0.33.32", {"center": v(680, 660) * mm, "radius": 3.4 * mm});
            skCircle(sketch, "E3.0.33.33", {"center": v(680, 680) * mm, "radius": 3.4 * mm});
            skCircle(sketch, "E3.0.33.34", {"center": v(680, 700) * mm, "radius": 3.4 * mm});
            skCircle(sketch, "E3.0.33.35", {"center": v(680, 720) * mm, "radius": 3.4 * mm});
            skCircle(sketch, "E3.0.33.36", {"center": v(680, 740) * mm, "radius": 3.4 * mm});
            skCircle(sketch, "E3.0.33.37", {"center": v(680, 760) * mm, "radius": 3.4 * mm});
            skCircle(sketch, "E3.0.33.38", {"center": v(680, 780) * mm, "radius": 3.4 * mm});
            skCircle(sketch, "E3.0.33.39", {"center": v(680, 800) * mm, "radius": 3.4 * mm});
            skCircle(sketch, "E3.0.33.40", {"center": v(680, 820) * mm, "radius": 3.4 * mm});
            skCircle(sketch, "E3.0.33.41", {"center": v(680, 840) * mm, "radius": 3.4 * mm});
            skCircle(sketch, "E3.0.33.42", {"center": v(680, 860) * mm, "radius": 3.4 * mm});
            skCircle(sketch, "E3.0.33.43", {"center": v(680, 880) * mm, "radius": 3.4 * mm});
            skCircle(sketch, "E3.0.33.44", {"center": v(680, 900) * mm, "radius": 3.4 * mm});
            skCircle(sketch, "E3.0.33.45", {"center": v(680, 920) * mm, "radius": 3.4 * mm});
            skCircle(sketch, "E3.0.33.46", {"center": v(680, 940) * mm, "radius": 3.4 * mm});
            skCircle(sketch, "E3.0.33.47", {"center": v(680, 960) * mm, "radius": 3.4 * mm});
            skCircle(sketch, "E3.0.33.48", {"center": v(680, 980) * mm, "radius": 3.4 * mm});
            skCircle(sketch, "E3.0.34.0", {"center": v(700, 20) * mm, "radius": 3.4 * mm});
            skCircle(sketch, "E3.0.34.1", {"center": v(700, 40) * mm, "radius": 3.4 * mm});
            skCircle(sketch, "E3.0.34.2", {"center": v(700, 60) * mm, "radius": 3.4 * mm});
            skCircle(sketch, "E3.0.34.3", {"center": v(700, 80) * mm, "radius": 3.4 * mm});
            skCircle(sketch, "E3.0.34.4", {"center": v(700, 100) * mm, "radius": 3.4 * mm});
            skCircle(sketch, "E3.0.34.5", {"center": v(700, 120) * mm, "radius": 3.4 * mm});
            skCircle(sketch, "E3.0.34.6", {"center": v(700, 140) * mm, "radius": 3.4 * mm});
            skCircle(sketch, "E3.0.34.7", {"center": v(700, 160) * mm, "radius": 3.4 * mm});
            skCircle(sketch, "E3.0.34.8", {"center": v(700, 180) * mm, "radius": 3.4 * mm});
            skCircle(sketch, "E3.0.34.9", {"center": v(700, 200) * mm, "radius": 3.4 * mm});
            skCircle(sketch, "E3.0.34.10", {"center": v(700, 220) * mm, "radius": 3.4 * mm});
            skCircle(sketch, "E3.0.34.11", {"center": v(700, 240) * mm, "radius": 3.4 * mm});
            skCircle(sketch, "E3.0.34.12", {"center": v(700, 260) * mm, "radius": 3.4 * mm});
            skCircle(sketch, "E3.0.34.13", {"center": v(700, 280) * mm, "radius": 3.4 * mm});
            skCircle(sketch, "E3.0.34.14", {"center": v(700, 300) * mm, "radius": 3.4 * mm});
            skCircle(sketch, "E3.0.34.15", {"center": v(700, 320) * mm, "radius": 3.4 * mm});
            skCircle(sketch, "E3.0.34.16", {"center": v(700, 340) * mm, "radius": 3.4 * mm});
            skCircle(sketch, "E3.0.34.17", {"center": v(700, 360) * mm, "radius": 3.4 * mm});
            skCircle(sketch, "E3.0.34.18", {"center": v(700, 380) * mm, "radius": 3.4 * mm});
            skCircle(sketch, "E3.0.34.19", {"center": v(700, 400) * mm, "radius": 3.4 * mm});
            skCircle(sketch, "E3.0.34.20", {"center": v(700, 420) * mm, "radius": 3.4 * mm});
            skCircle(sketch, "E3.0.34.21", {"center": v(700, 440) * mm, "radius": 3.4 * mm});
            skCircle(sketch, "E3.0.34.22", {"center": v(700, 460) * mm, "radius": 3.4 * mm});
            skCircle(sketch, "E3.0.34.23", {"center": v(700, 480) * mm, "radius": 3.4 * mm});
            skCircle(sketch, "E3.0.34.24", {"center": v(700, 500) * mm, "radius": 3.4 * mm});
            skCircle(sketch, "E3.0.34.25", {"center": v(700, 520) * mm, "radius": 3.4 * mm});
            skCircle(sketch, "E3.0.34.26", {"center": v(700, 540) * mm, "radius": 3.4 * mm});
            skCircle(sketch, "E3.0.34.27", {"center": v(700, 560) * mm, "radius": 3.4 * mm});
            skCircle(sketch, "E3.0.34.28", {"center": v(700, 580) * mm, "radius": 3.4 * mm});
            skCircle(sketch, "E3.0.34.29", {"center": v(700, 600) * mm, "radius": 3.4 * mm});
            skCircle(sketch, "E3.0.34.30", {"center": v(700, 620) * mm, "radius": 3.4 * mm});
            skCircle(sketch, "E3.0.34.31", {"center": v(700, 640) * mm, "radius": 3.4 * mm});
            skCircle(sketch, "E3.0.34.32", {"center": v(700, 660) * mm, "radius": 3.4 * mm});
            skCircle(sketch, "E3.0.34.33", {"center": v(700, 680) * mm, "radius": 3.4 * mm});
            skCircle(sketch, "E3.0.34.34", {"center": v(700, 700) * mm, "radius": 3.4 * mm});
            skCircle(sketch, "E3.0.34.35", {"center": v(700, 720) * mm, "radius": 3.4 * mm});
            skCircle(sketch, "E3.0.34.36", {"center": v(700, 740) * mm, "radius": 3.4 * mm});
            skCircle(sketch, "E3.0.34.37", {"center": v(700, 760) * mm, "radius": 3.4 * mm});
            skCircle(sketch, "E3.0.34.38", {"center": v(700, 780) * mm, "radius": 3.4 * mm});
            skCircle(sketch, "E3.0.34.39", {"center": v(700, 800) * mm, "radius": 3.4 * mm});
            skCircle(sketch, "E3.0.34.40", {"center": v(700, 820) * mm, "radius": 3.4 * mm});
            skCircle(sketch, "E3.0.34.41", {"center": v(700, 840) * mm, "radius": 3.4 * mm});
            skCircle(sketch, "E3.0.34.42", {"center": v(700, 860) * mm, "radius": 3.4 * mm});
            skCircle(sketch, "E3.0.34.43", {"center": v(700, 880) * mm, "radius": 3.4 * mm});
            skCircle(sketch, "E3.0.34.44", {"center": v(700, 900) * mm, "radius": 3.4 * mm});
            skCircle(sketch, "E3.0.34.45", {"center": v(700, 920) * mm, "radius": 3.4 * mm});
            skCircle(sketch, "E3.0.34.46", {"center": v(700, 940) * mm, "radius": 3.4 * mm});
            skCircle(sketch, "E3.0.34.47", {"center": v(700, 960) * mm, "radius": 3.4 * mm});
            skCircle(sketch, "E3.0.34.48", {"center": v(700, 980) * mm, "radius": 3.4 * mm});
            skCircle(sketch, "E3.0.35.0", {"center": v(720, 20) * mm, "radius": 3.4 * mm});
            skCircle(sketch, "E3.0.35.1", {"center": v(720, 40) * mm, "radius": 3.4 * mm});
            skCircle(sketch, "E3.0.35.2", {"center": v(720, 60) * mm, "radius": 3.4 * mm});
            skCircle(sketch, "E3.0.35.3", {"center": v(720, 80) * mm, "radius": 3.4 * mm});
            skCircle(sketch, "E3.0.35.4", {"center": v(720, 100) * mm, "radius": 3.4 * mm});
            skCircle(sketch, "E3.0.35.5", {"center": v(720, 120) * mm, "radius": 3.4 * mm});
            skCircle(sketch, "E3.0.35.6", {"center": v(720, 140) * mm, "radius": 3.4 * mm});
            skCircle(sketch, "E3.0.35.7", {"center": v(720, 160) * mm, "radius": 3.4 * mm});
            skCircle(sketch, "E3.0.35.8", {"center": v(720, 180) * mm, "radius": 3.4 * mm});
            skCircle(sketch, "E3.0.35.9", {"center": v(720, 200) * mm, "radius": 3.4 * mm});
            skCircle(sketch, "E3.0.35.10", {"center": v(720, 220) * mm, "radius": 3.4 * mm});
            skCircle(sketch, "E3.0.35.11", {"center": v(720, 240) * mm, "radius": 3.4 * mm});
            skCircle(sketch, "E3.0.35.12", {"center": v(720, 260) * mm, "radius": 3.4 * mm});
            skCircle(sketch, "E3.0.35.13", {"center": v(720, 280) * mm, "radius": 3.4 * mm});
            skCircle(sketch, "E3.0.35.14", {"center": v(720, 300) * mm, "radius": 3.4 * mm});
            skCircle(sketch, "E3.0.35.15", {"center": v(720, 320) * mm, "radius": 3.4 * mm});
            skCircle(sketch, "E3.0.35.16", {"center": v(720, 340) * mm, "radius": 3.4 * mm});
            skCircle(sketch, "E3.0.35.17", {"center": v(720, 360) * mm, "radius": 3.4 * mm});
            skCircle(sketch, "E3.0.35.18", {"center": v(720, 380) * mm, "radius": 3.4 * mm});
            skCircle(sketch, "E3.0.35.19", {"center": v(720, 400) * mm, "radius": 3.4 * mm});
            skCircle(sketch, "E3.0.35.20", {"center": v(720, 420) * mm, "radius": 3.4 * mm});
            skCircle(sketch, "E3.0.35.21", {"center": v(720, 440) * mm, "radius": 3.4 * mm});
            skCircle(sketch, "E3.0.35.22", {"center": v(720, 460) * mm, "radius": 3.4 * mm});
            skCircle(sketch, "E3.0.35.23", {"center": v(720, 480) * mm, "radius": 3.4 * mm});
            skCircle(sketch, "E3.0.35.24", {"center": v(720, 500) * mm, "radius": 3.4 * mm});
            skCircle(sketch, "E3.0.35.25", {"center": v(720, 520) * mm, "radius": 3.4 * mm});
            skCircle(sketch, "E3.0.35.26", {"center": v(720, 540) * mm, "radius": 3.4 * mm});
            skCircle(sketch, "E3.0.35.27", {"center": v(720, 560) * mm, "radius": 3.4 * mm});
            skCircle(sketch, "E3.0.35.28", {"center": v(720, 580) * mm, "radius": 3.4 * mm});
            skCircle(sketch, "E3.0.35.29", {"center": v(720, 600) * mm, "radius": 3.4 * mm});
            skCircle(sketch, "E3.0.35.30", {"center": v(720, 620) * mm, "radius": 3.4 * mm});
            skCircle(sketch, "E3.0.35.31", {"center": v(720, 640) * mm, "radius": 3.4 * mm});
            skCircle(sketch, "E3.0.35.32", {"center": v(720, 660) * mm, "radius": 3.4 * mm});
            skCircle(sketch, "E3.0.35.33", {"center": v(720, 680) * mm, "radius": 3.4 * mm});
            skCircle(sketch, "E3.0.35.34", {"center": v(720, 700) * mm, "radius": 3.4 * mm});
            skCircle(sketch, "E3.0.35.35", {"center": v(720, 720) * mm, "radius": 3.4 * mm});
            skCircle(sketch, "E3.0.35.36", {"center": v(720, 740) * mm, "radius": 3.4 * mm});
            skCircle(sketch, "E3.0.35.37", {"center": v(720, 760) * mm, "radius": 3.4 * mm});
            skCircle(sketch, "E3.0.35.38", {"center": v(720, 780) * mm, "radius": 3.4 * mm});
            skCircle(sketch, "E3.0.35.39", {"center": v(720, 800) * mm, "radius": 3.4 * mm});
            skCircle(sketch, "E3.0.35.40", {"center": v(720, 820) * mm, "radius": 3.4 * mm});
            skCircle(sketch, "E3.0.35.41", {"center": v(720, 840) * mm, "radius": 3.4 * mm});
            skCircle(sketch, "E3.0.35.42", {"center": v(720, 860) * mm, "radius": 3.4 * mm});
            skCircle(sketch, "E3.0.35.43", {"center": v(720, 880) * mm, "radius": 3.4 * mm});
            skCircle(sketch, "E3.0.35.44", {"center": v(720, 900) * mm, "radius": 3.4 * mm});
            skCircle(sketch, "E3.0.35.45", {"center": v(720, 920) * mm, "radius": 3.4 * mm});
            skCircle(sketch, "E3.0.35.46", {"center": v(720, 940) * mm, "radius": 3.4 * mm});
            skCircle(sketch, "E3.0.35.47", {"center": v(720, 960) * mm, "radius": 3.4 * mm});
            skCircle(sketch, "E3.0.35.48", {"center": v(720, 980) * mm, "radius": 3.4 * mm});
            skCircle(sketch, "E4.0.36.0", {"center": v(740, 20) * mm, "radius": 3.4 * mm});
            skCircle(sketch, "E4.0.36.1", {"center": v(740, 40) * mm, "radius": 3.4 * mm});
            skCircle(sketch, "E4.0.36.2", {"center": v(740, 60) * mm, "radius": 3.4 * mm});
            skCircle(sketch, "E4.0.36.3", {"center": v(740, 80) * mm, "radius": 3.4 * mm});
            skCircle(sketch, "E4.0.36.4", {"center": v(740, 100) * mm, "radius": 3.4 * mm});
            skCircle(sketch, "E4.0.36.5", {"center": v(740, 120) * mm, "radius": 3.4 * mm});
            skCircle(sketch, "E4.0.36.6", {"center": v(740, 140) * mm, "radius": 3.4 * mm});
            skCircle(sketch, "E4.0.36.7", {"center": v(740, 160) * mm, "radius": 3.4 * mm});
            skCircle(sketch, "E4.0.36.8", {"center": v(740, 180) * mm, "radius": 3.4 * mm});
            skCircle(sketch, "E4.0.36.9", {"center": v(740, 200) * mm, "radius": 3.4 * mm});
            skCircle(sketch, "E4.0.36.10", {"center": v(740, 220) * mm, "radius": 3.4 * mm});
            skCircle(sketch, "E4.0.36.11", {"center": v(740, 240) * mm, "radius": 3.4 * mm});
            skCircle(sketch, "E4.0.36.12", {"center": v(740, 260) * mm, "radius": 3.4 * mm});
            skCircle(sketch, "E4.0.36.13", {"center": v(740, 280) * mm, "radius": 3.4 * mm});
            skCircle(sketch, "E4.0.36.14", {"center": v(740, 300) * mm, "radius": 3.4 * mm});
            skCircle(sketch, "E4.0.36.15", {"center": v(740, 320) * mm, "radius": 3.4 * mm});
            skCircle(sketch, "E4.0.36.16", {"center": v(740, 340) * mm, "radius": 3.4 * mm});
            skCircle(sketch, "E4.0.36.17", {"center": v(740, 360) * mm, "radius": 3.4 * mm});
            skCircle(sketch, "E4.0.36.18", {"center": v(740, 380) * mm, "radius": 3.4 * mm});
            skCircle(sketch, "E4.0.36.19", {"center": v(740, 400) * mm, "radius": 3.4 * mm});
            skCircle(sketch, "E4.0.36.20", {"center": v(740, 420) * mm, "radius": 3.4 * mm});
            skCircle(sketch, "E4.0.36.21", {"center": v(740, 440) * mm, "radius": 3.4 * mm});
            skCircle(sketch, "E4.0.36.22", {"center": v(740, 460) * mm, "radius": 3.4 * mm});
            skCircle(sketch, "E4.0.36.23", {"center": v(740, 480) * mm, "radius": 3.4 * mm});
            skCircle(sketch, "E4.0.36.24", {"center": v(740, 500) * mm, "radius": 3.4 * mm});
            skCircle(sketch, "E4.0.36.25", {"center": v(740, 520) * mm, "radius": 3.4 * mm});
            skCircle(sketch, "E4.0.36.26", {"center": v(740, 540) * mm, "radius": 3.4 * mm});
            skCircle(sketch, "E4.0.36.27", {"center": v(740, 560) * mm, "radius": 3.4 * mm});
            skCircle(sketch, "E4.0.36.28", {"center": v(740, 580) * mm, "radius": 3.4 * mm});
            skCircle(sketch, "E4.0.36.29", {"center": v(740, 600) * mm, "radius": 3.4 * mm});
            skCircle(sketch, "E4.0.36.30", {"center": v(740, 620) * mm, "radius": 3.4 * mm});
            skCircle(sketch, "E4.0.36.31", {"center": v(740, 640) * mm, "radius": 3.4 * mm});
            skCircle(sketch, "E4.0.36.32", {"center": v(740, 660) * mm, "radius": 3.4 * mm});
            skCircle(sketch, "E4.0.36.33", {"center": v(740, 680) * mm, "radius": 3.4 * mm});
            skCircle(sketch, "E4.0.36.34", {"center": v(740, 700) * mm, "radius": 3.4 * mm});
            skCircle(sketch, "E4.0.36.35", {"center": v(740, 720) * mm, "radius": 3.4 * mm});
            skCircle(sketch, "E4.0.36.36", {"center": v(740, 740) * mm, "radius": 3.4 * mm});
            skCircle(sketch, "E4.0.36.37", {"center": v(740, 760) * mm, "radius": 3.4 * mm});
            skCircle(sketch, "E4.0.36.38", {"center": v(740, 780) * mm, "radius": 3.4 * mm});
            skCircle(sketch, "E4.0.36.39", {"center": v(740, 800) * mm, "radius": 3.4 * mm});
            skCircle(sketch, "E4.0.36.40", {"center": v(740, 820) * mm, "radius": 3.4 * mm});
            skCircle(sketch, "E4.0.36.41", {"center": v(740, 840) * mm, "radius": 3.4 * mm});
            skCircle(sketch, "E4.0.36.42", {"center": v(740, 860) * mm, "radius": 3.4 * mm});
            skCircle(sketch, "E4.0.36.43", {"center": v(740, 880) * mm, "radius": 3.4 * mm});
            skCircle(sketch, "E4.0.36.44", {"center": v(740, 900) * mm, "radius": 3.4 * mm});
            skCircle(sketch, "E4.0.36.45", {"center": v(740, 920) * mm, "radius": 3.4 * mm});
            skCircle(sketch, "E4.0.36.46", {"center": v(740, 940) * mm, "radius": 3.4 * mm});
            skCircle(sketch, "E4.0.36.47", {"center": v(740, 960) * mm, "radius": 3.4 * mm});
            skCircle(sketch, "E4.0.36.48", {"center": v(740, 980) * mm, "radius": 3.4 * mm});
            skSolve(sketch);
        }
        {
            var Q0;
            Q0=qSketchRegion(id+"F4",true);
            extrude(context, id + "F5", {"entities" : qUnion([Q0]), "operationType" : NewBodyOperationType.REMOVE, "oppositeDirection" : true, "depth" : 55 * mm});
        }
        {
            var Q0;
            Q0=makeQuery(id+"F1.opExtrude","CAP_FACE",FACE,{"disambiguationData":[OSD([sQuery(id+"F0.wireOp",EDGE,"E0.bottom"),sQuery(id+"F0.wireOp",EDGE,"E0.top"),sQuery(id+"F0.wireOp",EDGE,"E0.left"),sQuery(id+"F0.wireOp",EDGE,"E0.right")])],"isStart":true});
            var sketch = newSketch(context, id + "F6", { "sketchPlane" : qUnion([Q0])});
            skSolve(sketch);
        }
        {
            var Q0;
            Q0=makeQuery(id+"F1.opExtrude","CAP_FACE",FACE,{"disambiguationData":[OSD([sQuery(id+"F0.wireOp",EDGE,"E0.bottom"),sQuery(id+"F0.wireOp",EDGE,"E0.top"),sQuery(id+"F0.wireOp",EDGE,"E0.left"),sQuery(id+"F0.wireOp",EDGE,"E0.right")])],"isStart":false});
            var sketch = newSketch(context, id + "F7", { "sketchPlane" : qUnion([Q0])});
            skCircle(sketch, "E5", {"center": v(100, 100) * mm, "radius": 11 * mm});
            skCircle(sketch, "E6.0.1.0", {"center": v(100, 900) * mm, "radius": 11 * mm});
            skCircle(sketch, "E6.1.0.0", {"center": v(660, 100) * mm, "radius": 11 * mm});
            skCircle(sketch, "E6.1.1.0", {"center": v(660, 900) * mm, "radius": 11 * mm});
            skLineSegment(sketch, "E6.direction1", {"start": v(100, 100) * mm, "end": v(660, 100) * mm, "construction": true});
            skLineSegment(sketch, "E6.direction2", {"start": v(100, 100) * mm, "end": v(100, 900) * mm, "construction": true});
            skSolve(sketch);
        }
        {
            var Q0;
            Q0=makeQuery(id+"F7.imprint","IMPRINT",FACE,{"disambiguationData":[TD([[makeQuery(id+"F7.imprint","IMPRINT",EDGE,{"derivedFrom":sQuery(id+"F7.wireOp",EDGE,"E5")}),1.0]])]});
            var Q1;
            Q1=makeQuery(id+"F7.imprint","IMPRINT",FACE,{"disambiguationData":[TD([[makeQuery(id+"F7.imprint","IMPRINT",EDGE,{"derivedFrom":sQuery(id+"F7.wireOp",EDGE,"E6.1.0.0")}),1.0]])]});
            var Q2;
            Q2=makeQuery(id+"F7.imprint","IMPRINT",FACE,{"disambiguationData":[TD([[makeQuery(id+"F7.imprint","IMPRINT",EDGE,{"derivedFrom":sQuery(id+"F7.wireOp",EDGE,"E6.0.1.0")}),1.0]])]});
            var Q3;
            Q3=makeQuery(id+"F7.imprint","IMPRINT",FACE,{"disambiguationData":[TD([[makeQuery(id+"F7.imprint","IMPRINT",EDGE,{"derivedFrom":sQuery(id+"F7.wireOp",EDGE,"E6.1.1.0")}),1.0]])]});
            var Q4;
            Q4=sQuery(id+"F7.wireOp",EDGE,"E5");
            var Q5;
            Q5=sQuery(id+"F7.wireOp",EDGE,"E6.1.0.0");
            var Q6;
            Q6=sQuery(id+"F7.wireOp",EDGE,"E6.0.1.0");
            var Q7;
            Q7=sQuery(id+"F7.wireOp",EDGE,"E6.1.1.0");
            extrude(context, id + "F8", {"entities" : qUnion([Q0, Q1, Q2, Q3]), "operationType" : NewBodyOperationType.REMOVE, "surfaceEntities" : qUnion([Q4, Q5, Q6, Q7]), "oppositeDirection" : true, "depth" : 14 * mm});
        }
        {
            var Q0;
            Q0=makeQuery(id+"F1.opExtrude","CAP_FACE",FACE,{"disambiguationData":[OSD([sQuery(id+"F0.wireOp",EDGE,"E0.bottom"),sQuery(id+"F0.wireOp",EDGE,"E0.top"),sQuery(id+"F0.wireOp",EDGE,"E0.left"),sQuery(id+"F0.wireOp",EDGE,"E0.right")])],"isStart":false});
            var sketch = newSketch(context, id + "F9", { "sketchPlane" : qUnion([Q0])});
            skCircle(sketch, "E7", {"center": v(100, 100) * mm, "radius": 5 * mm});
            skCircle(sketch, "E8.0.1.0", {"center": v(100, 900) * mm, "radius": 5 * mm});
            skCircle(sketch, "E8.1.0.0", {"center": v(660, 100) * mm, "radius": 5 * mm});
            skCircle(sketch, "E8.1.1.0", {"center": v(660, 900) * mm, "radius": 5 * mm});
            skLineSegment(sketch, "E8.direction1", {"start": v(100, 100) * mm, "end": v(660, 100) * mm, "construction": true});
            skLineSegment(sketch, "E8.direction2", {"start": v(100, 100) * mm, "end": v(100, 900) * mm, "construction": true});
            skSolve(sketch);
        }
        {
            var Q0;
            Q0=makeQuery(id+"F9.imprint","IMPRINT",FACE,{"disambiguationData":[TD([[makeQuery(id+"F9.imprint","IMPRINT",EDGE,{"derivedFrom":sQuery(id+"F9.wireOp",EDGE,"E7")}),1.0]])]});
            var Q1;
            Q1=makeQuery(id+"F9.imprint","IMPRINT",FACE,{"disambiguationData":[TD([[makeQuery(id+"F9.imprint","IMPRINT",EDGE,{"derivedFrom":sQuery(id+"F9.wireOp",EDGE,"E8.1.0.0")}),1.0]])]});
            var Q2;
            Q2=makeQuery(id+"F9.imprint","IMPRINT",FACE,{"disambiguationData":[TD([[makeQuery(id+"F9.imprint","IMPRINT",EDGE,{"derivedFrom":sQuery(id+"F9.wireOp",EDGE,"E8.0.1.0")}),1.0]])]});
            var Q3;
            Q3=makeQuery(id+"F9.imprint","IMPRINT",FACE,{"disambiguationData":[TD([[makeQuery(id+"F9.imprint","IMPRINT",EDGE,{"derivedFrom":sQuery(id+"F9.wireOp",EDGE,"E8.1.1.0")}),1.0]])]});
            extrude(context, id + "F10", {"entities" : qUnion([Q0, Q1, Q2, Q3]), "operationType" : NewBodyOperationType.REMOVE, "oppositeDirection" : true, "depth" : 25 * mm});
        }
        {
            var Q0;
            {var subQ3=sQuery(id+"F0.wireOp",EDGE,"E0.bottom");Q0=makeQuery(id+"F6.imprint","IMPRINT",FACE,{"disambiguationData":[TD([[makeQuery(id+"F6.imprint","IMPRINT",EDGE,{"derivedFrom":makeQuery(id+"F1.opExtrude","CAP_EDGE",EDGE,{"disambiguationData":[OSD([subQ3])],"isStart":true})}),-1.0]])]});}
            var sketch = newSketch(context, id + "F11", { "sketchPlane" : qUnion([Q0])});
            skLineSegment(sketch, "E9.bottom", {"start": v(720, -30) * mm, "end": v(680, -30) * mm});
            skLineSegment(sketch, "E9.top", {"start": v(720, -90) * mm, "end": v(680, -90) * mm});
            skLineSegment(sketch, "E9.left", {"start": v(730, -40) * mm, "end": v(730, -80) * mm});
            skLineSegment(sketch, "E9.right", {"start": v(670, -40) * mm, "end": v(670, -80) * mm});
            skPoint(sketch, "E10.visualSharp", {"position": v(730, -90) * mm});
            skArc(sketch, "E10.filletArc", {"start": v(720, -90) * mm, "mid": v(727.07, -87.07) * mm, "end": v(730, -80) * mm});
            skPoint(sketch, "E11.visualSharp", {"position": v(670, -90) * mm});
            skArc(sketch, "E11.filletArc", {"start": v(670, -80) * mm, "mid": v(672.93, -87.07) * mm, "end": v(680, -90) * mm});
            skPoint(sketch, "E12.visualSharp", {"position": v(670, -30) * mm});
            skArc(sketch, "E12.filletArc", {"start": v(680, -30) * mm, "mid": v(672.93, -32.93) * mm, "end": v(670, -40) * mm});
            skPoint(sketch, "E13.visualSharp", {"position": v(730, -30) * mm});
            skArc(sketch, "E13.filletArc", {"start": v(730, -40) * mm, "mid": v(727.07, -32.93) * mm, "end": v(720, -30) * mm});
            skArc(sketch, "E14.MirrorCS", {"start": v(30, -40) * mm, "mid": v(32.93, -32.93) * mm, "end": v(40, -30) * mm});
            skArc(sketch, "E15.MirrorCS", {"start": v(40, -90) * mm, "mid": v(32.93, -87.07) * mm, "end": v(30, -80) * mm});
            skArc(sketch, "E16.MirrorCS", {"start": v(80, -30) * mm, "mid": v(87.07, -32.93) * mm, "end": v(90, -40) * mm});
            skArc(sketch, "E17.MirrorCS", {"start": v(90, -80) * mm, "mid": v(87.07, -87.07) * mm, "end": v(80, -90) * mm});
            skPoint(sketch, "E18.MirrorP", {"position": v(30, -30) * mm});
            skPoint(sketch, "E19.MirrorP", {"position": v(90, -30) * mm});
            skPoint(sketch, "E20.MirrorP", {"position": v(30, -90) * mm});
            skPoint(sketch, "E21.MirrorP", {"position": v(90, -90) * mm});
            skLineSegment(sketch, "E22.MirrorCS", {"start": v(40, -90) * mm, "end": v(80, -90) * mm});
            skLineSegment(sketch, "E23.MirrorCS", {"start": v(30, -40) * mm, "end": v(30, -80) * mm});
            skLineSegment(sketch, "E24.MirrorCS", {"start": v(40, -30) * mm, "end": v(80, -30) * mm});
            skLineSegment(sketch, "E25.MirrorCS", {"start": v(90, -40) * mm, "end": v(90, -80) * mm});
            skArc(sketch, "E26.MirrorCS", {"start": v(720, -910) * mm, "mid": v(727.07, -912.93) * mm, "end": v(730, -920) * mm});
            skArc(sketch, "E27.MirrorCS", {"start": v(670, -920) * mm, "mid": v(672.93, -912.93) * mm, "end": v(680, -910) * mm});
            skArc(sketch, "E28.MirrorCS", {"start": v(680, -970) * mm, "mid": v(672.93, -967.07) * mm, "end": v(670, -960) * mm});
            skArc(sketch, "E29.MirrorCS", {"start": v(730, -960) * mm, "mid": v(727.07, -967.07) * mm, "end": v(720, -970) * mm});
            skArc(sketch, "E30.MirrorCS", {"start": v(30, -960) * mm, "mid": v(32.93, -967.07) * mm, "end": v(40, -970) * mm});
            skArc(sketch, "E31.MirrorCS", {"start": v(40, -910) * mm, "mid": v(32.93, -912.93) * mm, "end": v(30, -920) * mm});
            skArc(sketch, "E32.MirrorCS", {"start": v(90, -920) * mm, "mid": v(87.07, -912.93) * mm, "end": v(80, -910) * mm});
            skArc(sketch, "E33.MirrorCS", {"start": v(80, -970) * mm, "mid": v(87.07, -967.07) * mm, "end": v(90, -960) * mm});
            skPoint(sketch, "E34.MirrorP", {"position": v(90, -970) * mm});
            skPoint(sketch, "E35.MirrorP", {"position": v(30, -910) * mm});
            skPoint(sketch, "E36.MirrorP", {"position": v(90, -910) * mm});
            skPoint(sketch, "E37.MirrorP", {"position": v(730, -910) * mm});
            skPoint(sketch, "E38.MirrorP", {"position": v(670, -910) * mm});
            skPoint(sketch, "E39.MirrorP", {"position": v(670, -970) * mm});
            skPoint(sketch, "E40.MirrorP", {"position": v(730, -970) * mm});
            skLineSegment(sketch, "E41.MirrorCS", {"start": v(40, -970) * mm, "end": v(80, -970) * mm});
            skLineSegment(sketch, "E42.MirrorCS", {"start": v(90, -960) * mm, "end": v(90, -920) * mm});
            skLineSegment(sketch, "E43.MirrorCS", {"start": v(720, -970) * mm, "end": v(680, -970) * mm});
            skLineSegment(sketch, "E44.MirrorCS", {"start": v(720, -910) * mm, "end": v(680, -910) * mm});
            skLineSegment(sketch, "E45.MirrorCS", {"start": v(730, -960) * mm, "end": v(730, -920) * mm});
            skLineSegment(sketch, "E46.MirrorCS", {"start": v(670, -960) * mm, "end": v(670, -920) * mm});
            skLineSegment(sketch, "E47.MirrorCS", {"start": v(30, -960) * mm, "end": v(30, -920) * mm});
            skLineSegment(sketch, "E48.MirrorCS", {"start": v(40, -910) * mm, "end": v(80, -910) * mm});
            skPoint(sketch, "E49.MirrorP", {"position": v(30, -970) * mm});
            skLineSegment(sketch, "E50.bottom", {"start": v(120, -970) * mm, "end": v(360, -970) * mm});
            skLineSegment(sketch, "E50.top", {"start": v(120, -910) * mm, "end": v(360, -910) * mm});
            skLineSegment(sketch, "E50.left", {"start": v(110, -960) * mm, "end": v(110, -920) * mm});
            skLineSegment(sketch, "E50.right", {"start": v(370, -960) * mm, "end": v(370, -920) * mm});
            skPoint(sketch, "E51.visualSharp", {"position": v(110, -910) * mm});
            skArc(sketch, "E51.filletArc", {"start": v(120, -910) * mm, "mid": v(112.93, -912.93) * mm, "end": v(110, -920) * mm});
            skPoint(sketch, "E52.visualSharp", {"position": v(370, -910) * mm});
            skArc(sketch, "E52.filletArc", {"start": v(370, -920) * mm, "mid": v(367.07, -912.93) * mm, "end": v(360, -910) * mm});
            skPoint(sketch, "E53.visualSharp", {"position": v(370, -970) * mm});
            skArc(sketch, "E53.filletArc", {"start": v(360, -970) * mm, "mid": v(367.07, -967.07) * mm, "end": v(370, -960) * mm});
            skPoint(sketch, "E54.visualSharp", {"position": v(110, -970) * mm});
            skArc(sketch, "E54.filletArc", {"start": v(110, -960) * mm, "mid": v(112.93, -967.07) * mm, "end": v(120, -970) * mm});
            skLineSegment(sketch, "E55.bottom", {"start": v(80, -890) * mm, "end": v(40, -890) * mm});
            skLineSegment(sketch, "E55.top", {"start": v(80, -510) * mm, "end": v(40, -510) * mm});
            skLineSegment(sketch, "E55.left", {"start": v(90, -880) * mm, "end": v(90, -520) * mm});
            skLineSegment(sketch, "E55.right", {"start": v(30, -880) * mm, "end": v(30, -520) * mm});
            skPoint(sketch, "E56.visualSharp", {"position": v(30, -890) * mm});
            skArc(sketch, "E56.filletArc", {"start": v(30, -880) * mm, "mid": v(32.93, -887.07) * mm, "end": v(40, -890) * mm});
            skPoint(sketch, "E57.visualSharp", {"position": v(90, -890) * mm});
            skArc(sketch, "E57.filletArc", {"start": v(80, -890) * mm, "mid": v(87.07, -887.07) * mm, "end": v(90, -880) * mm});
            skPoint(sketch, "E58.visualSharp", {"position": v(30, -510) * mm});
            skArc(sketch, "E58.filletArc", {"start": v(40, -510) * mm, "mid": v(32.93, -512.93) * mm, "end": v(30, -520) * mm});
            skPoint(sketch, "E59.visualSharp", {"position": v(90, -510) * mm});
            skArc(sketch, "E59.filletArc", {"start": v(90, -520) * mm, "mid": v(87.07, -512.93) * mm, "end": v(80, -510) * mm});
            skArc(sketch, "E60.MirrorCS", {"start": v(650, -960) * mm, "mid": v(647.07, -967.07) * mm, "end": v(640, -970) * mm});
            skArc(sketch, "E61.MirrorCS", {"start": v(390, -920) * mm, "mid": v(392.93, -912.93) * mm, "end": v(400, -910) * mm});
            skArc(sketch, "E62.MirrorCS", {"start": v(640, -910) * mm, "mid": v(647.07, -912.93) * mm, "end": v(650, -920) * mm});
            skArc(sketch, "E63.MirrorCS", {"start": v(400, -970) * mm, "mid": v(392.93, -967.07) * mm, "end": v(390, -960) * mm});
            skPoint(sketch, "E64.MirrorP", {"position": v(650, -970) * mm});
            skPoint(sketch, "E65.MirrorP", {"position": v(390, -970) * mm});
            skLineSegment(sketch, "E66.MirrorCS", {"start": v(390, -960) * mm, "end": v(390, -920) * mm});
            skPoint(sketch, "E67.MirrorP", {"position": v(390, -910) * mm});
            skLineSegment(sketch, "E68.MirrorCS", {"start": v(650, -960) * mm, "end": v(650, -920) * mm});
            skLineSegment(sketch, "E69.MirrorCS", {"start": v(640, -970) * mm, "end": v(400, -970) * mm});
            skLineSegment(sketch, "E70.MirrorCS", {"start": v(640, -910) * mm, "end": v(400, -910) * mm});
            skPoint(sketch, "E71.MirrorP", {"position": v(650, -910) * mm});
            skLineSegment(sketch, "E72.bottom", {"start": v(120, -890) * mm, "end": v(220, -890) * mm});
            skLineSegment(sketch, "E72.top", {"start": v(120, -510) * mm, "end": v(220, -510) * mm});
            skLineSegment(sketch, "E72.left", {"start": v(110, -880) * mm, "end": v(110, -520) * mm});
            skLineSegment(sketch, "E72.right", {"start": v(230, -880) * mm, "end": v(230, -520) * mm});
            skPoint(sketch, "E73.visualSharp", {"position": v(110, -510) * mm});
            skArc(sketch, "E73.filletArc", {"start": v(120, -510) * mm, "mid": v(112.93, -512.93) * mm, "end": v(110, -520) * mm});
            skPoint(sketch, "E74.visualSharp", {"position": v(230, -510) * mm});
            skArc(sketch, "E74.filletArc", {"start": v(230, -520) * mm, "mid": v(227.07, -512.93) * mm, "end": v(220, -510) * mm});
            skPoint(sketch, "E75.visualSharp", {"position": v(230, -890) * mm});
            skArc(sketch, "E75.filletArc", {"start": v(220, -890) * mm, "mid": v(227.07, -887.07) * mm, "end": v(230, -880) * mm});
            skPoint(sketch, "E76.visualSharp", {"position": v(110, -890) * mm});
            skArc(sketch, "E76.filletArc", {"start": v(110, -880) * mm, "mid": v(112.93, -887.07) * mm, "end": v(120, -890) * mm});
            skPoint(sketch, "E77.1.0.0", {"position": v(250, -890) * mm});
            skPoint(sketch, "E77.1.0.1", {"position": v(250, -510) * mm});
            skLineSegment(sketch, "E77.1.0.2", {"start": v(260, -890) * mm, "end": v(360, -890) * mm});
            skLineSegment(sketch, "E77.1.0.3", {"start": v(260, -510) * mm, "end": v(360, -510) * mm});
            skPoint(sketch, "E77.1.0.4", {"position": v(370, -510) * mm});
            skLineSegment(sketch, "E77.1.0.5", {"start": v(250, -880) * mm, "end": v(250, -520) * mm});
            skLineSegment(sketch, "E77.1.0.6", {"start": v(370, -880) * mm, "end": v(370, -520) * mm});
            skPoint(sketch, "E77.1.0.7", {"position": v(370, -890) * mm});
            skArc(sketch, "E77.1.0.8", {"start": v(370, -520) * mm, "mid": v(367.07, -512.93) * mm, "end": v(360, -510) * mm});
            skArc(sketch, "E77.1.0.9", {"start": v(360, -890) * mm, "mid": v(367.07, -887.07) * mm, "end": v(370, -880) * mm});
            skArc(sketch, "E77.1.0.10", {"start": v(260, -510) * mm, "mid": v(252.93, -512.93) * mm, "end": v(250, -520) * mm});
            skArc(sketch, "E77.1.0.11", {"start": v(250, -880) * mm, "mid": v(252.93, -887.07) * mm, "end": v(260, -890) * mm});
            skLineSegment(sketch, "E77.direction1", {"start": v(110, -890) * mm, "end": v(250, -890) * mm, "construction": true});
            skArc(sketch, "E78.MirrorCS", {"start": v(510, -880) * mm, "mid": v(507.07, -887.07) * mm, "end": v(500, -890) * mm});
            skArc(sketch, "E79.MirrorCS", {"start": v(720, -510) * mm, "mid": v(727.07, -512.93) * mm, "end": v(730, -520) * mm});
            skArc(sketch, "E80.MirrorCS", {"start": v(650, -880) * mm, "mid": v(647.07, -887.07) * mm, "end": v(640, -890) * mm});
            skArc(sketch, "E81.MirrorCS", {"start": v(390, -520) * mm, "mid": v(392.93, -512.93) * mm, "end": v(400, -510) * mm});
            skArc(sketch, "E82.MirrorCS", {"start": v(680, -890) * mm, "mid": v(672.93, -887.07) * mm, "end": v(670, -880) * mm});
            skArc(sketch, "E83.MirrorCS", {"start": v(530, -520) * mm, "mid": v(532.93, -512.93) * mm, "end": v(540, -510) * mm});
            skArc(sketch, "E84.MirrorCS", {"start": v(400, -890) * mm, "mid": v(392.93, -887.07) * mm, "end": v(390, -880) * mm});
            skArc(sketch, "E85.MirrorCS", {"start": v(500, -510) * mm, "mid": v(507.07, -512.93) * mm, "end": v(510, -520) * mm});
            skLineSegment(sketch, "E86.MirrorCS", {"start": v(640, -890) * mm, "end": v(540, -890) * mm});
            skArc(sketch, "E87.MirrorCS", {"start": v(540, -890) * mm, "mid": v(532.93, -887.07) * mm, "end": v(530, -880) * mm});
            skArc(sketch, "E88.MirrorCS", {"start": v(640, -510) * mm, "mid": v(647.07, -512.93) * mm, "end": v(650, -520) * mm});
            skArc(sketch, "E89.MirrorCS", {"start": v(730, -880) * mm, "mid": v(727.07, -887.07) * mm, "end": v(720, -890) * mm});
            skArc(sketch, "E90.MirrorCS", {"start": v(670, -520) * mm, "mid": v(672.93, -512.93) * mm, "end": v(680, -510) * mm});
            skLineSegment(sketch, "E91.MirrorCS", {"start": v(500, -510) * mm, "end": v(400, -510) * mm});
            skPoint(sketch, "E92.MirrorP", {"position": v(510, -510) * mm});
            skPoint(sketch, "E93.MirrorP", {"position": v(390, -510) * mm});
            skPoint(sketch, "E94.MirrorP", {"position": v(390, -890) * mm});
            skLineSegment(sketch, "E95.MirrorCS", {"start": v(650, -890) * mm, "end": v(510, -890) * mm, "construction": true});
            skLineSegment(sketch, "E96.MirrorCS", {"start": v(680, -890) * mm, "end": v(720, -890) * mm});
            skLineSegment(sketch, "E97.MirrorCS", {"start": v(640, -510) * mm, "end": v(540, -510) * mm});
            skLineSegment(sketch, "E98.MirrorCS", {"start": v(680, -510) * mm, "end": v(720, -510) * mm});
            skPoint(sketch, "E99.MirrorP", {"position": v(530, -890) * mm});
            skPoint(sketch, "E100.MirrorP", {"position": v(730, -890) * mm});
            skPoint(sketch, "E101.MirrorP", {"position": v(730, -510) * mm});
            skLineSegment(sketch, "E102.MirrorCS", {"start": v(670, -880) * mm, "end": v(670, -520) * mm});
            skLineSegment(sketch, "E103.MirrorCS", {"start": v(650, -880) * mm, "end": v(650, -520) * mm});
            skLineSegment(sketch, "E104.MirrorCS", {"start": v(530, -880) * mm, "end": v(530, -520) * mm});
            skPoint(sketch, "E105.MirrorP", {"position": v(670, -890) * mm});
            skPoint(sketch, "E106.MirrorP", {"position": v(510, -890) * mm});
            skLineSegment(sketch, "E107.MirrorCS", {"start": v(390, -880) * mm, "end": v(390, -520) * mm});
            skPoint(sketch, "E108.MirrorP", {"position": v(650, -510) * mm});
            skLineSegment(sketch, "E109.MirrorCS", {"start": v(730, -880) * mm, "end": v(730, -520) * mm});
            skPoint(sketch, "E110.MirrorP", {"position": v(530, -510) * mm});
            skPoint(sketch, "E111.MirrorP", {"position": v(670, -510) * mm});
            skPoint(sketch, "E112.MirrorP", {"position": v(650, -890) * mm});
            skLineSegment(sketch, "E113.MirrorCS", {"start": v(500, -890) * mm, "end": v(400, -890) * mm});
            skLineSegment(sketch, "E114.MirrorCS", {"start": v(510, -880) * mm, "end": v(510, -520) * mm});
            skArc(sketch, "E115.MirrorCS", {"start": v(30, -120) * mm, "mid": v(32.93, -112.93) * mm, "end": v(40, -110) * mm});
            skArc(sketch, "E116.MirrorCS", {"start": v(120, -490) * mm, "mid": v(112.93, -487.07) * mm, "end": v(110, -480) * mm});
            skArc(sketch, "E117.MirrorCS", {"start": v(390, -480) * mm, "mid": v(392.93, -487.07) * mm, "end": v(400, -490) * mm});
            skArc(sketch, "E118.MirrorCS", {"start": v(650, -120) * mm, "mid": v(647.07, -112.93) * mm, "end": v(640, -110) * mm});
            skArc(sketch, "E119.MirrorCS", {"start": v(720, -490) * mm, "mid": v(727.07, -487.07) * mm, "end": v(730, -480) * mm});
            skArc(sketch, "E120.MirrorCS", {"start": v(510, -120) * mm, "mid": v(507.07, -112.93) * mm, "end": v(500, -110) * mm});
            skArc(sketch, "E121.MirrorCS", {"start": v(250, -120) * mm, "mid": v(252.93, -112.93) * mm, "end": v(260, -110) * mm});
            skArc(sketch, "E122.MirrorCS", {"start": v(260, -490) * mm, "mid": v(252.93, -487.07) * mm, "end": v(250, -480) * mm});
            skArc(sketch, "E123.MirrorCS", {"start": v(370, -480) * mm, "mid": v(367.07, -487.07) * mm, "end": v(360, -490) * mm});
            skArc(sketch, "E124.MirrorCS", {"start": v(640, -490) * mm, "mid": v(647.07, -487.07) * mm, "end": v(650, -480) * mm});
            skArc(sketch, "E125.MirrorCS", {"start": v(500, -490) * mm, "mid": v(507.07, -487.07) * mm, "end": v(510, -480) * mm});
            skArc(sketch, "E126.MirrorCS", {"start": v(90, -480) * mm, "mid": v(87.07, -487.07) * mm, "end": v(80, -490) * mm});
            skArc(sketch, "E127.MirrorCS", {"start": v(110, -120) * mm, "mid": v(112.93, -112.93) * mm, "end": v(120, -110) * mm});
            skArc(sketch, "E128.MirrorCS", {"start": v(220, -110) * mm, "mid": v(227.07, -112.93) * mm, "end": v(230, -120) * mm});
            skArc(sketch, "E129.MirrorCS", {"start": v(40, -490) * mm, "mid": v(32.93, -487.07) * mm, "end": v(30, -480) * mm});
            skArc(sketch, "E130.MirrorCS", {"start": v(680, -110) * mm, "mid": v(672.93, -112.93) * mm, "end": v(670, -120) * mm});
            skArc(sketch, "E131.MirrorCS", {"start": v(540, -110) * mm, "mid": v(532.93, -112.93) * mm, "end": v(530, -120) * mm});
            skArc(sketch, "E132.MirrorCS", {"start": v(400, -110) * mm, "mid": v(392.93, -112.93) * mm, "end": v(390, -120) * mm});
            skArc(sketch, "E133.MirrorCS", {"start": v(530, -480) * mm, "mid": v(532.93, -487.07) * mm, "end": v(540, -490) * mm});
            skArc(sketch, "E134.MirrorCS", {"start": v(670, -480) * mm, "mid": v(672.93, -487.07) * mm, "end": v(680, -490) * mm});
            skArc(sketch, "E135.MirrorCS", {"start": v(230, -480) * mm, "mid": v(227.07, -487.07) * mm, "end": v(220, -490) * mm});
            skLineSegment(sketch, "E136.MirrorCS", {"start": v(120, -110) * mm, "end": v(220, -110) * mm});
            skArc(sketch, "E137.MirrorCS", {"start": v(360, -110) * mm, "mid": v(367.07, -112.93) * mm, "end": v(370, -120) * mm});
            skArc(sketch, "E138.MirrorCS", {"start": v(730, -120) * mm, "mid": v(727.07, -112.93) * mm, "end": v(720, -110) * mm});
            skLineSegment(sketch, "E139.MirrorCS", {"start": v(640, -110) * mm, "end": v(540, -110) * mm});
            skArc(sketch, "E140.MirrorCS", {"start": v(80, -110) * mm, "mid": v(87.07, -112.93) * mm, "end": v(90, -120) * mm});
            skLineSegment(sketch, "E141.MirrorCS", {"start": v(650, -120) * mm, "end": v(650, -480) * mm});
            skPoint(sketch, "E142.MirrorP", {"position": v(730, -110) * mm});
            skPoint(sketch, "E143.MirrorP", {"position": v(30, -110) * mm});
            skPoint(sketch, "E144.MirrorP", {"position": v(110, -490) * mm});
            skLineSegment(sketch, "E145.MirrorCS", {"start": v(670, -120) * mm, "end": v(670, -480) * mm});
            skLineSegment(sketch, "E146.MirrorCS", {"start": v(30, -120) * mm, "end": v(30, -480) * mm});
            skLineSegment(sketch, "E147.MirrorCS", {"start": v(230, -120) * mm, "end": v(230, -480) * mm});
            skPoint(sketch, "E148.MirrorP", {"position": v(530, -110) * mm});
            skLineSegment(sketch, "E149.MirrorCS", {"start": v(90, -120) * mm, "end": v(90, -480) * mm});
            skLineSegment(sketch, "E150.MirrorCS", {"start": v(110, -120) * mm, "end": v(110, -480) * mm});
            skLineSegment(sketch, "E151.MirrorCS", {"start": v(640, -490) * mm, "end": v(540, -490) * mm});
            skLineSegment(sketch, "E152.MirrorCS", {"start": v(80, -490) * mm, "end": v(40, -490) * mm});
            skLineSegment(sketch, "E153.MirrorCS", {"start": v(120, -490) * mm, "end": v(220, -490) * mm});
            skPoint(sketch, "E154.MirrorP", {"position": v(390, -490) * mm});
            skLineSegment(sketch, "E155.MirrorCS", {"start": v(680, -110) * mm, "end": v(720, -110) * mm});
            skLineSegment(sketch, "E156.MirrorCS", {"start": v(80, -110) * mm, "end": v(40, -110) * mm});
            skLineSegment(sketch, "E157.MirrorCS", {"start": v(110, -110) * mm, "end": v(250, -110) * mm, "construction": true});
            skPoint(sketch, "E158.MirrorP", {"position": v(510, -490) * mm});
            skLineSegment(sketch, "E159.MirrorCS", {"start": v(650, -110) * mm, "end": v(510, -110) * mm, "construction": true});
            skPoint(sketch, "E160.MirrorP", {"position": v(370, -110) * mm});
            skLineSegment(sketch, "E161.MirrorCS", {"start": v(500, -490) * mm, "end": v(400, -490) * mm});
            skPoint(sketch, "E162.MirrorP", {"position": v(370, -490) * mm});
            skPoint(sketch, "E163.MirrorP", {"position": v(250, -110) * mm});
            skLineSegment(sketch, "E164.MirrorCS", {"start": v(370, -120) * mm, "end": v(370, -480) * mm});
            skPoint(sketch, "E165.MirrorP", {"position": v(670, -490) * mm});
            skPoint(sketch, "E166.MirrorP", {"position": v(90, -490) * mm});
            skPoint(sketch, "E167.MirrorP", {"position": v(110, -110) * mm});
            skLineSegment(sketch, "E168.MirrorCS", {"start": v(250, -120) * mm, "end": v(250, -480) * mm});
            skPoint(sketch, "E169.MirrorP", {"position": v(530, -490) * mm});
            skLineSegment(sketch, "E170.MirrorCS", {"start": v(260, -490) * mm, "end": v(360, -490) * mm});
            skLineSegment(sketch, "E171.MirrorCS", {"start": v(510, -120) * mm, "end": v(510, -480) * mm});
            skPoint(sketch, "E172.MirrorP", {"position": v(30, -490) * mm});
            skPoint(sketch, "E173.MirrorP", {"position": v(230, -110) * mm});
            skLineSegment(sketch, "E174.MirrorCS", {"start": v(500, -110) * mm, "end": v(400, -110) * mm});
            skLineSegment(sketch, "E175.MirrorCS", {"start": v(260, -110) * mm, "end": v(360, -110) * mm});
            skPoint(sketch, "E176.MirrorP", {"position": v(650, -490) * mm});
            skLineSegment(sketch, "E177.MirrorCS", {"start": v(730, -120) * mm, "end": v(730, -480) * mm});
            skLineSegment(sketch, "E178.MirrorCS", {"start": v(390, -120) * mm, "end": v(390, -480) * mm});
            skPoint(sketch, "E179.MirrorP", {"position": v(670, -110) * mm});
            skPoint(sketch, "E180.MirrorP", {"position": v(90, -110) * mm});
            skPoint(sketch, "E181.MirrorP", {"position": v(230, -490) * mm});
            skLineSegment(sketch, "E182.MirrorCS", {"start": v(530, -120) * mm, "end": v(530, -480) * mm});
            skLineSegment(sketch, "E183.MirrorCS", {"start": v(680, -490) * mm, "end": v(720, -490) * mm});
            skPoint(sketch, "E184.MirrorP", {"position": v(390, -110) * mm});
            skPoint(sketch, "E185.MirrorP", {"position": v(510, -110) * mm});
            skPoint(sketch, "E186.MirrorP", {"position": v(250, -490) * mm});
            skPoint(sketch, "E187.MirrorP", {"position": v(650, -110) * mm});
            skPoint(sketch, "E188.MirrorP", {"position": v(730, -490) * mm});
            skArc(sketch, "E189.MirrorCS", {"start": v(400, -30) * mm, "mid": v(392.93, -32.93) * mm, "end": v(390, -40) * mm});
            skArc(sketch, "E190.MirrorCS", {"start": v(120, -90) * mm, "mid": v(112.93, -87.07) * mm, "end": v(110, -80) * mm});
            skArc(sketch, "E191.MirrorCS", {"start": v(370, -80) * mm, "mid": v(367.07, -87.07) * mm, "end": v(360, -90) * mm});
            skArc(sketch, "E192.MirrorCS", {"start": v(360, -30) * mm, "mid": v(367.07, -32.93) * mm, "end": v(370, -40) * mm});
            skArc(sketch, "E193.MirrorCS", {"start": v(110, -40) * mm, "mid": v(112.93, -32.93) * mm, "end": v(120, -30) * mm});
            skArc(sketch, "E194.MirrorCS", {"start": v(650, -40) * mm, "mid": v(647.07, -32.93) * mm, "end": v(640, -30) * mm});
            skArc(sketch, "E195.MirrorCS", {"start": v(390, -80) * mm, "mid": v(392.93, -87.07) * mm, "end": v(400, -90) * mm});
            skArc(sketch, "E196.MirrorCS", {"start": v(640, -90) * mm, "mid": v(647.07, -87.07) * mm, "end": v(650, -80) * mm});
            skPoint(sketch, "E197.MirrorP", {"position": v(650, -90) * mm});
            skLineSegment(sketch, "E198.MirrorCS", {"start": v(370, -40) * mm, "end": v(370, -80) * mm});
            skLineSegment(sketch, "E199.MirrorCS", {"start": v(390, -40) * mm, "end": v(390, -80) * mm});
            skLineSegment(sketch, "E200.MirrorCS", {"start": v(650, -40) * mm, "end": v(650, -80) * mm});
            skLineSegment(sketch, "E201.MirrorCS", {"start": v(640, -30) * mm, "end": v(400, -30) * mm});
            skPoint(sketch, "E202.MirrorP", {"position": v(110, -30) * mm});
            skPoint(sketch, "E203.MirrorP", {"position": v(110, -90) * mm});
            skPoint(sketch, "E204.MirrorP", {"position": v(370, -90) * mm});
            skPoint(sketch, "E205.MirrorP", {"position": v(390, -30) * mm});
            skLineSegment(sketch, "E206.MirrorCS", {"start": v(120, -30) * mm, "end": v(360, -30) * mm});
            skPoint(sketch, "E207.MirrorP", {"position": v(370, -30) * mm});
            skPoint(sketch, "E208.MirrorP", {"position": v(650, -30) * mm});
            skPoint(sketch, "E209.MirrorP", {"position": v(390, -90) * mm});
            skLineSegment(sketch, "E210.MirrorCS", {"start": v(640, -90) * mm, "end": v(400, -90) * mm});
            skLineSegment(sketch, "E211.MirrorCS", {"start": v(120, -90) * mm, "end": v(360, -90) * mm});
            skLineSegment(sketch, "E212.MirrorCS", {"start": v(110, -40) * mm, "end": v(110, -80) * mm});
            skSolve(sketch);
        }
        {
            var Q0;
            Q0=makeQuery(id+"F11.imprint","IMPRINT",FACE,{"disambiguationData":[TD([[makeQuery(id+"F11.imprint","IMPRINT",EDGE,{"derivedFrom":sQuery(id+"F11.wireOp",EDGE,"E9.bottom")}),1.0]])]});
            var Q1;
            Q1=makeQuery(id+"F11.imprint","IMPRINT",FACE,{"disambiguationData":[TD([[makeQuery(id+"F11.imprint","IMPRINT",EDGE,{"derivedFrom":sQuery(id+"F11.wireOp",EDGE,"E14.MirrorCS")}),-1.0]])]});
            var Q2;
            Q2=makeQuery(id+"F11.imprint","IMPRINT",FACE,{"disambiguationData":[TD([[makeQuery(id+"F11.imprint","IMPRINT",EDGE,{"derivedFrom":sQuery(id+"F11.wireOp",EDGE,"E26.MirrorCS")}),-1.0]])]});
            var Q3;
            Q3=makeQuery(id+"F11.imprint","IMPRINT",FACE,{"disambiguationData":[TD([[makeQuery(id+"F11.imprint","IMPRINT",EDGE,{"derivedFrom":sQuery(id+"F11.wireOp",EDGE,"E30.MirrorCS")}),1.0]])]});
            var Q4;
            Q4=makeQuery(id+"F11.imprint","IMPRINT",FACE,{"disambiguationData":[TD([[makeQuery(id+"F11.imprint","IMPRINT",EDGE,{"derivedFrom":sQuery(id+"F11.wireOp",EDGE,"E190.MirrorCS")}),-1.0]])]});
            var Q5;
            Q5=makeQuery(id+"F11.imprint","IMPRINT",FACE,{"disambiguationData":[TD([[makeQuery(id+"F11.imprint","IMPRINT",EDGE,{"derivedFrom":sQuery(id+"F11.wireOp",EDGE,"E189.MirrorCS")}),1.0]])]});
            var Q6;
            Q6=makeQuery(id+"F11.imprint","IMPRINT",FACE,{"disambiguationData":[TD([[makeQuery(id+"F11.imprint","IMPRINT",EDGE,{"derivedFrom":sQuery(id+"F11.wireOp",EDGE,"E115.MirrorCS")}),-1.0]])]});
            var Q7;
            Q7=makeQuery(id+"F11.imprint","IMPRINT",FACE,{"disambiguationData":[TD([[makeQuery(id+"F11.imprint","IMPRINT",EDGE,{"derivedFrom":sQuery(id+"F11.wireOp",EDGE,"E116.MirrorCS")}),-1.0]])]});
            var Q8;
            Q8=makeQuery(id+"F11.imprint","IMPRINT",FACE,{"disambiguationData":[TD([[makeQuery(id+"F11.imprint","IMPRINT",EDGE,{"derivedFrom":sQuery(id+"F11.wireOp",EDGE,"E121.MirrorCS")}),-1.0]])]});
            var Q9;
            Q9=makeQuery(id+"F11.imprint","IMPRINT",FACE,{"disambiguationData":[TD([[makeQuery(id+"F11.imprint","IMPRINT",EDGE,{"derivedFrom":sQuery(id+"F11.wireOp",EDGE,"E117.MirrorCS")}),1.0]])]});
            var Q10;
            Q10=makeQuery(id+"F11.imprint","IMPRINT",FACE,{"disambiguationData":[TD([[makeQuery(id+"F11.imprint","IMPRINT",EDGE,{"derivedFrom":sQuery(id+"F11.wireOp",EDGE,"E118.MirrorCS")}),1.0]])]});
            var Q11;
            Q11=makeQuery(id+"F11.imprint","IMPRINT",FACE,{"disambiguationData":[TD([[makeQuery(id+"F11.imprint","IMPRINT",EDGE,{"derivedFrom":sQuery(id+"F11.wireOp",EDGE,"E119.MirrorCS")}),1.0]])]});
            var Q12;
            Q12=makeQuery(id+"F11.imprint","IMPRINT",FACE,{"disambiguationData":[TD([[makeQuery(id+"F11.imprint","IMPRINT",EDGE,{"derivedFrom":sQuery(id+"F11.wireOp",EDGE,"E79.MirrorCS")}),-1.0]])]});
            var Q13;
            Q13=makeQuery(id+"F11.imprint","IMPRINT",FACE,{"disambiguationData":[TD([[makeQuery(id+"F11.imprint","IMPRINT",EDGE,{"derivedFrom":sQuery(id+"F11.wireOp",EDGE,"E55.bottom")}),-1.0]])]});
            var Q14;
            Q14=makeQuery(id+"F11.imprint","IMPRINT",FACE,{"disambiguationData":[TD([[makeQuery(id+"F11.imprint","IMPRINT",EDGE,{"derivedFrom":sQuery(id+"F11.wireOp",EDGE,"E72.bottom")}),1.0]])]});
            var Q15;
            Q15=makeQuery(id+"F11.imprint","IMPRINT",FACE,{"disambiguationData":[TD([[makeQuery(id+"F11.imprint","IMPRINT",EDGE,{"derivedFrom":sQuery(id+"F11.wireOp",EDGE,"E77.1.0.2")}),1.0]])]});
            var Q16;
            Q16=makeQuery(id+"F11.imprint","IMPRINT",FACE,{"disambiguationData":[TD([[makeQuery(id+"F11.imprint","IMPRINT",EDGE,{"derivedFrom":sQuery(id+"F11.wireOp",EDGE,"E78.MirrorCS")}),-1.0]])]});
            var Q17;
            Q17=makeQuery(id+"F11.imprint","IMPRINT",FACE,{"disambiguationData":[TD([[makeQuery(id+"F11.imprint","IMPRINT",EDGE,{"derivedFrom":sQuery(id+"F11.wireOp",EDGE,"E80.MirrorCS")}),-1.0]])]});
            var Q18;
            Q18=makeQuery(id+"F11.imprint","IMPRINT",FACE,{"disambiguationData":[TD([[makeQuery(id+"F11.imprint","IMPRINT",EDGE,{"derivedFrom":sQuery(id+"F11.wireOp",EDGE,"E60.MirrorCS")}),-1.0]])]});
            var Q19;
            Q19=makeQuery(id+"F11.imprint","IMPRINT",FACE,{"disambiguationData":[TD([[makeQuery(id+"F11.imprint","IMPRINT",EDGE,{"derivedFrom":sQuery(id+"F11.wireOp",EDGE,"E50.bottom")}),1.0]])]});
            var Q20;
            Q20=sQuery(id+"F11.wireOp",EDGE,"E9.left");
            var Q21;
            Q21=sQuery(id+"F11.wireOp",EDGE,"E10.filletArc");
            var Q22;
            Q22=sQuery(id+"F11.wireOp",EDGE,"E9.top");
            var Q23;
            Q23=sQuery(id+"F11.wireOp",EDGE,"E11.filletArc");
            var Q24;
            Q24=sQuery(id+"F11.wireOp",EDGE,"E9.right");
            var Q25;
            Q25=sQuery(id+"F11.wireOp",EDGE,"E12.filletArc");
            var Q26;
            Q26=sQuery(id+"F11.wireOp",EDGE,"E9.bottom");
            var Q27;
            Q27=sQuery(id+"F11.wireOp",EDGE,"E13.filletArc");
            extrude(context, id + "F12", {"entities" : qUnion([Q0, Q1, Q2, Q3, Q4, Q5, Q6, Q7, Q8, Q9, Q10, Q11, Q12, Q13, Q14, Q15, Q16, Q17, Q18, Q19]), "operationType" : NewBodyOperationType.REMOVE, "surfaceEntities" : qUnion([Q20, Q21, Q22, Q23, Q24, Q25, Q26, Q27]), "oppositeDirection" : true, "depth" : 5 * mm});
        }
    });
